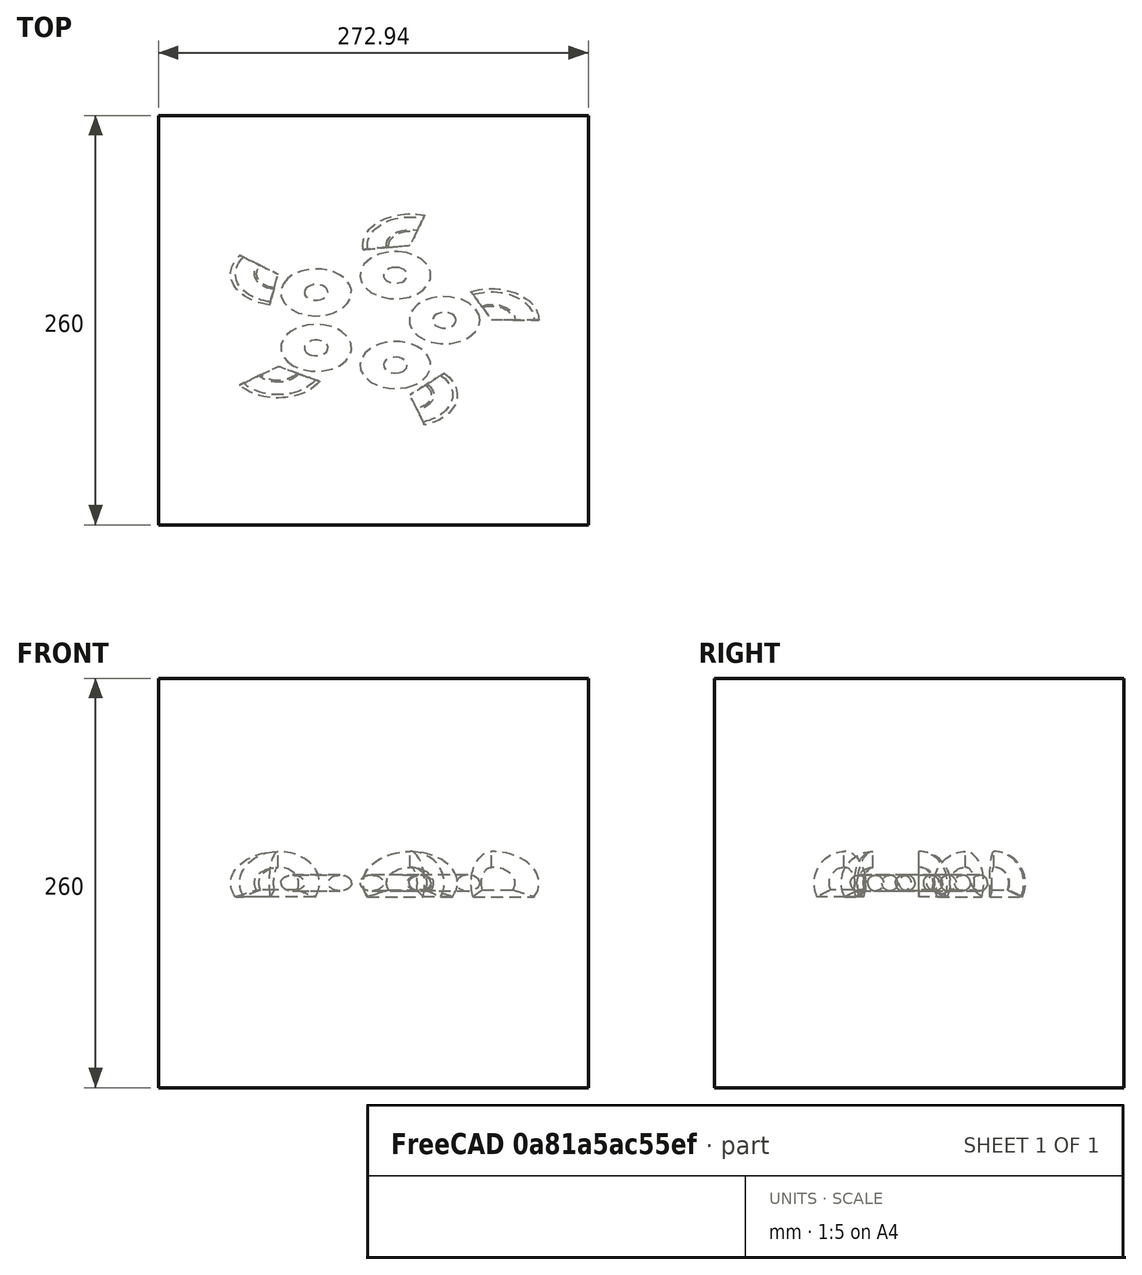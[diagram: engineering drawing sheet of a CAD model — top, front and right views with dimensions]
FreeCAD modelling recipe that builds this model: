
FCSTD DOCUMENT  (FreeCAD 1.0R39109 (Git))
Label: arrayTest-7_scaled
License: All rights reserved
LicenseURL: http://en.wikipedia.org/wiki/All_rights_reserved
objects: App::DocumentObjectGroupPython×1248, Part::FeaturePython×5, App::Part×2, Part::MultiFuse×1
note: 6 computed .brp shape members not serialized (recipe doc carries the construction recipe); baked Part::Feature solids carry a one-line shape summary decoded from their .brp

FEATURE [App::DocumentObjectGroupPython] HALFPI  # scripted group (container) (typed FeaturePython)
  name = HALFPI
  value = pi/2.
FEATURE [App::DocumentObjectGroupPython] PI  # scripted group (container) (typed FeaturePython)
  name = PI
  value = 1.*pi
FEATURE [App::DocumentObjectGroupPython] TWOPI  # scripted group (container) (typed FeaturePython)
  name = TWOPI
  value = 2.*pi
FEATURE [App::DocumentObjectGroupPython] Constants  # scripted group (container) (typed FeaturePython)
  Group = -> [HALFPI,PI,TWOPI]
FEATURE [App::DocumentObjectGroupPython] Variables  # scripted group (container) (typed FeaturePython)
FEATURE [App::DocumentObjectGroupPython] Quantities  # scripted group (container) (typed FeaturePython)
FEATURE [App::DocumentObjectGroupPython] Isotopes  # scripted group (container) (typed FeaturePython)
FEATURE [App::DocumentObjectGroupPython] Elements  # scripted group (container) (typed FeaturePython)
FEATURE [App::DocumentObjectGroupPython] G4Isotopes  # scripted group (container) (typed FeaturePython)
FEATURE [App::DocumentObjectGroupPython] H_element  # scripted group (container) (typed FeaturePython)
  Z = 1
  atom_value = 1.008
  formula = H
  name = H_element
FEATURE [App::DocumentObjectGroupPython] He_element  # scripted group (container) (typed FeaturePython)
  Z = 2
  atom_value = 4.0026
  formula = He
  name = He_element
FEATURE [App::DocumentObjectGroupPython] Li_element  # scripted group (container) (typed FeaturePython)
  Z = 3
  atom_value = 6.94
  formula = Li
  name = Li_element
FEATURE [App::DocumentObjectGroupPython] Be_element  # scripted group (container) (typed FeaturePython)
  Z = 4
  atom_value = 9.01218
  formula = Be
  name = Be_element
FEATURE [App::DocumentObjectGroupPython] B_element  # scripted group (container) (typed FeaturePython)
  Z = 5
  atom_value = 10.81
  formula = B
  name = B_element
FEATURE [App::DocumentObjectGroupPython] C_element  # scripted group (container) (typed FeaturePython)
  Z = 6
  atom_value = 12.011
  formula = C
  name = C_element
FEATURE [App::DocumentObjectGroupPython] N_element  # scripted group (container) (typed FeaturePython)
  Z = 7
  atom_value = 14.007
  formula = N
  name = N_element
FEATURE [App::DocumentObjectGroupPython] O_element  # scripted group (container) (typed FeaturePython)
  Z = 8
  atom_value = 15.999
  formula = O
  name = O_element
FEATURE [App::DocumentObjectGroupPython] F_element  # scripted group (container) (typed FeaturePython)
  Z = 9
  atom_value = 18.9984
  formula = F
  name = F_element
FEATURE [App::DocumentObjectGroupPython] Ne_element  # scripted group (container) (typed FeaturePython)
  Z = 10
  atom_value = 20.1797
  formula = Ne
  name = Ne_element
FEATURE [App::DocumentObjectGroupPython] Na_element  # scripted group (container) (typed FeaturePython)
  Z = 11
  atom_value = 22.9898
  formula = Na
  name = Na_element
FEATURE [App::DocumentObjectGroupPython] Mg_element  # scripted group (container) (typed FeaturePython)
  Z = 12
  atom_value = 24.305
  formula = Mg
  name = Mg_element
FEATURE [App::DocumentObjectGroupPython] Al_element  # scripted group (container) (typed FeaturePython)
  Z = 13
  atom_value = 26.9815
  formula = Al
  name = Al_element
FEATURE [App::DocumentObjectGroupPython] Si_element  # scripted group (container) (typed FeaturePython)
  Z = 14
  atom_value = 28.085
  formula = Si
  name = Si_element
FEATURE [App::DocumentObjectGroupPython] P_element  # scripted group (container) (typed FeaturePython)
  Z = 15
  atom_value = 30.9738
  formula = P
  name = P_element
FEATURE [App::DocumentObjectGroupPython] S_element  # scripted group (container) (typed FeaturePython)
  Z = 16
  atom_value = 32.06
  formula = S
  name = S_element
FEATURE [App::DocumentObjectGroupPython] Cl_element  # scripted group (container) (typed FeaturePython)
  Z = 17
  atom_value = 35.45
  formula = Cl
  name = Cl_element
FEATURE [App::DocumentObjectGroupPython] Ar_element  # scripted group (container) (typed FeaturePython)
  Z = 18
  atom_value = 39.95
  formula = Ar
  name = Ar_element
FEATURE [App::DocumentObjectGroupPython] K_element  # scripted group (container) (typed FeaturePython)
  Z = 19
  atom_value = 39.0983
  formula = K
  name = K_element
FEATURE [App::DocumentObjectGroupPython] Ca_element  # scripted group (container) (typed FeaturePython)
  Z = 20
  atom_value = 40.078
  formula = Ca
  name = Ca_element
FEATURE [App::DocumentObjectGroupPython] Sc_element  # scripted group (container) (typed FeaturePython)
  Z = 21
  atom_value = 44.9559
  formula = Sc
  name = Sc_element
FEATURE [App::DocumentObjectGroupPython] Ti_element  # scripted group (container) (typed FeaturePython)
  Z = 22
  atom_value = 47.867
  formula = Ti
  name = Ti_element
FEATURE [App::DocumentObjectGroupPython] V_element  # scripted group (container) (typed FeaturePython)
  Z = 23
  atom_value = 50.9415
  formula = V
  name = V_element
FEATURE [App::DocumentObjectGroupPython] Cr_element  # scripted group (container) (typed FeaturePython)
  Z = 24
  atom_value = 51.9961
  formula = Cr
  name = Cr_element
FEATURE [App::DocumentObjectGroupPython] Mn_element  # scripted group (container) (typed FeaturePython)
  Z = 25
  atom_value = 54.938
  formula = Mn
  name = Mn_element
FEATURE [App::DocumentObjectGroupPython] Fe_element  # scripted group (container) (typed FeaturePython)
  Z = 26
  atom_value = 55.845
  formula = Fe
  name = Fe_element
FEATURE [App::DocumentObjectGroupPython] Co_element  # scripted group (container) (typed FeaturePython)
  Z = 27
  atom_value = 58.9332
  formula = Co
  name = Co_element
FEATURE [App::DocumentObjectGroupPython] Ni_element  # scripted group (container) (typed FeaturePython)
  Z = 28
  atom_value = 58.6934
  formula = Ni
  name = Ni_element
FEATURE [App::DocumentObjectGroupPython] Cu_element  # scripted group (container) (typed FeaturePython)
  Z = 29
  atom_value = 63.546
  formula = Cu
  name = Cu_element
FEATURE [App::DocumentObjectGroupPython] Zn_element  # scripted group (container) (typed FeaturePython)
  Z = 30
  atom_value = 65.38
  formula = Zn
  name = Zn_element
FEATURE [App::DocumentObjectGroupPython] Ga_element  # scripted group (container) (typed FeaturePython)
  Z = 31
  atom_value = 69.723
  formula = Ga
  name = Ga_element
FEATURE [App::DocumentObjectGroupPython] Ge_element  # scripted group (container) (typed FeaturePython)
  Z = 32
  atom_value = 72.63
  formula = Ge
  name = Ge_element
FEATURE [App::DocumentObjectGroupPython] As_element  # scripted group (container) (typed FeaturePython)
  Z = 33
  atom_value = 74.9216
  formula = As
  name = As_element
FEATURE [App::DocumentObjectGroupPython] Se_element  # scripted group (container) (typed FeaturePython)
  Z = 34
  atom_value = 78.971
  formula = Se
  name = Se_element
FEATURE [App::DocumentObjectGroupPython] Br_element  # scripted group (container) (typed FeaturePython)
  Z = 35
  atom_value = 79.904
  formula = Br
  name = Br_element
FEATURE [App::DocumentObjectGroupPython] Kr_element  # scripted group (container) (typed FeaturePython)
  Z = 36
  atom_value = 83.798
  formula = Kr
  name = Kr_element
FEATURE [App::DocumentObjectGroupPython] Rb_element  # scripted group (container) (typed FeaturePython)
  Z = 37
  atom_value = 85.4678
  formula = Rb
  name = Rb_element
FEATURE [App::DocumentObjectGroupPython] Sr_element  # scripted group (container) (typed FeaturePython)
  Z = 38
  atom_value = 87.62
  formula = Sr
  name = Sr_element
FEATURE [App::DocumentObjectGroupPython] Y_element  # scripted group (container) (typed FeaturePython)
  Z = 39
  atom_value = 88.9058
  formula = Y
  name = Y_element
FEATURE [App::DocumentObjectGroupPython] Zr_element  # scripted group (container) (typed FeaturePython)
  Z = 40
  atom_value = 91.224
  formula = Zr
  name = Zr_element
FEATURE [App::DocumentObjectGroupPython] Nb_element  # scripted group (container) (typed FeaturePython)
  Z = 41
  atom_value = 92.9064
  formula = Nb
  name = Nb_element
FEATURE [App::DocumentObjectGroupPython] Mo_element  # scripted group (container) (typed FeaturePython)
  Z = 42
  atom_value = 95.95
  formula = Mo
  name = Mo_element
FEATURE [App::DocumentObjectGroupPython] Tc_element  # scripted group (container) (typed FeaturePython)
  Z = 43
  atom_value = 97
  formula = Tc
  name = Tc_element
FEATURE [App::DocumentObjectGroupPython] Ru_element  # scripted group (container) (typed FeaturePython)
  Z = 44
  atom_value = 101.07
  formula = Ru
  name = Ru_element
FEATURE [App::DocumentObjectGroupPython] Rh_element  # scripted group (container) (typed FeaturePython)
  Z = 45
  atom_value = 102.905
  formula = Rh
  name = Rh_element
FEATURE [App::DocumentObjectGroupPython] Pd_element  # scripted group (container) (typed FeaturePython)
  Z = 46
  atom_value = 106.42
  formula = Pd
  name = Pd_element
FEATURE [App::DocumentObjectGroupPython] Ag_element  # scripted group (container) (typed FeaturePython)
  Z = 47
  atom_value = 107.868
  formula = Ag
  name = Ag_element
FEATURE [App::DocumentObjectGroupPython] Cd_element  # scripted group (container) (typed FeaturePython)
  Z = 48
  atom_value = 112.414
  formula = Cd
  name = Cd_element
FEATURE [App::DocumentObjectGroupPython] In_element  # scripted group (container) (typed FeaturePython)
  Z = 49
  atom_value = 114.818
  formula = In
  name = In_element
FEATURE [App::DocumentObjectGroupPython] Sn_element  # scripted group (container) (typed FeaturePython)
  Z = 50
  atom_value = 118.71
  formula = Sn
  name = Sn_element
FEATURE [App::DocumentObjectGroupPython] Sb_element  # scripted group (container) (typed FeaturePython)
  Z = 51
  atom_value = 121.76
  formula = Sb
  name = Sb_element
FEATURE [App::DocumentObjectGroupPython] Te_element  # scripted group (container) (typed FeaturePython)
  Z = 52
  atom_value = 127.6
  formula = Te
  name = Te_element
FEATURE [App::DocumentObjectGroupPython] I_element  # scripted group (container) (typed FeaturePython)
  Z = 53
  atom_value = 126.904
  formula = I
  name = I_element
FEATURE [App::DocumentObjectGroupPython] Xe_element  # scripted group (container) (typed FeaturePython)
  Z = 54
  atom_value = 131.293
  formula = Xe
  name = Xe_element
FEATURE [App::DocumentObjectGroupPython] Cs_element  # scripted group (container) (typed FeaturePython)
  Z = 55
  atom_value = 132.905
  formula = Cs
  name = Cs_element
FEATURE [App::DocumentObjectGroupPython] Ba_element  # scripted group (container) (typed FeaturePython)
  Z = 56
  atom_value = 137.327
  formula = Ba
  name = Ba_element
FEATURE [App::DocumentObjectGroupPython] La_element  # scripted group (container) (typed FeaturePython)
  Z = 57
  atom_value = 138.905
  formula = La
  name = La_element
FEATURE [App::DocumentObjectGroupPython] Ce_element  # scripted group (container) (typed FeaturePython)
  Z = 58
  atom_value = 140.116
  formula = Ce
  name = Ce_element
FEATURE [App::DocumentObjectGroupPython] Pr_element  # scripted group (container) (typed FeaturePython)
  Z = 59
  atom_value = 140.908
  formula = Pr
  name = Pr_element
FEATURE [App::DocumentObjectGroupPython] Nd_element  # scripted group (container) (typed FeaturePython)
  Z = 60
  atom_value = 144.242
  formula = Nd
  name = Nd_element
FEATURE [App::DocumentObjectGroupPython] Pm_element  # scripted group (container) (typed FeaturePython)
  Z = 61
  atom_value = 145
  formula = Pm
  name = Pm_element
FEATURE [App::DocumentObjectGroupPython] Sm_element  # scripted group (container) (typed FeaturePython)
  Z = 62
  atom_value = 150.36
  formula = Sm
  name = Sm_element
FEATURE [App::DocumentObjectGroupPython] Eu_element  # scripted group (container) (typed FeaturePython)
  Z = 63
  atom_value = 151.964
  formula = Eu
  name = Eu_element
FEATURE [App::DocumentObjectGroupPython] Gd_element  # scripted group (container) (typed FeaturePython)
  Z = 64
  atom_value = 157.25
  formula = Gd
  name = Gd_element
FEATURE [App::DocumentObjectGroupPython] Tb_element  # scripted group (container) (typed FeaturePython)
  Z = 65
  atom_value = 158.925
  formula = Tb
  name = Tb_element
FEATURE [App::DocumentObjectGroupPython] Dy_element  # scripted group (container) (typed FeaturePython)
  Z = 66
  atom_value = 162.5
  formula = Dy
  name = Dy_element
FEATURE [App::DocumentObjectGroupPython] Ho_element  # scripted group (container) (typed FeaturePython)
  Z = 67
  atom_value = 164.93
  formula = Ho
  name = Ho_element
FEATURE [App::DocumentObjectGroupPython] Er_element  # scripted group (container) (typed FeaturePython)
  Z = 68
  atom_value = 167.259
  formula = Er
  name = Er_element
FEATURE [App::DocumentObjectGroupPython] Tm_element  # scripted group (container) (typed FeaturePython)
  Z = 69
  atom_value = 168.934
  formula = Tm
  name = Tm_element
FEATURE [App::DocumentObjectGroupPython] Yb_element  # scripted group (container) (typed FeaturePython)
  Z = 70
  atom_value = 173.045
  formula = Yb
  name = Yb_element
FEATURE [App::DocumentObjectGroupPython] Lu_element  # scripted group (container) (typed FeaturePython)
  Z = 71
  atom_value = 174.967
  formula = Lu
  name = Lu_element
FEATURE [App::DocumentObjectGroupPython] Hf_element  # scripted group (container) (typed FeaturePython)
  Z = 72
  atom_value = 178.49
  formula = Hf
  name = Hf_element
FEATURE [App::DocumentObjectGroupPython] Ta_element  # scripted group (container) (typed FeaturePython)
  Z = 73
  atom_value = 180.948
  formula = Ta
  name = Ta_element
FEATURE [App::DocumentObjectGroupPython] W_element  # scripted group (container) (typed FeaturePython)
  Z = 74
  atom_value = 183.84
  formula = W
  name = W_element
FEATURE [App::DocumentObjectGroupPython] Re_element  # scripted group (container) (typed FeaturePython)
  Z = 75
  atom_value = 186.207
  formula = Re
  name = Re_element
FEATURE [App::DocumentObjectGroupPython] Os_element  # scripted group (container) (typed FeaturePython)
  Z = 76
  atom_value = 190.23
  formula = Os
  name = Os_element
FEATURE [App::DocumentObjectGroupPython] Ir_element  # scripted group (container) (typed FeaturePython)
  Z = 77
  atom_value = 192.217
  formula = Ir
  name = Ir_element
FEATURE [App::DocumentObjectGroupPython] Pt_element  # scripted group (container) (typed FeaturePython)
  Z = 78
  atom_value = 195.084
  formula = Pt
  name = Pt_element
FEATURE [App::DocumentObjectGroupPython] Au_element  # scripted group (container) (typed FeaturePython)
  Z = 79
  atom_value = 196.967
  formula = Au
  name = Au_element
FEATURE [App::DocumentObjectGroupPython] Hg_element  # scripted group (container) (typed FeaturePython)
  Z = 80
  atom_value = 200.592
  formula = Hg
  name = Hg_element
FEATURE [App::DocumentObjectGroupPython] Tl_element  # scripted group (container) (typed FeaturePython)
  Z = 81
  atom_value = 204.38
  formula = Tl
  name = Tl_element
FEATURE [App::DocumentObjectGroupPython] Pb_element  # scripted group (container) (typed FeaturePython)
  Z = 82
  atom_value = 207.2
  formula = Pb
  name = Pb_element
FEATURE [App::DocumentObjectGroupPython] Bi_element  # scripted group (container) (typed FeaturePython)
  Z = 83
  atom_value = 208.98
  formula = Bi
  name = Bi_element
FEATURE [App::DocumentObjectGroupPython] Po_element  # scripted group (container) (typed FeaturePython)
  Z = 84
  atom_value = 209
  formula = Po
  name = Po_element
FEATURE [App::DocumentObjectGroupPython] At_element  # scripted group (container) (typed FeaturePython)
  Z = 85
  atom_value = 210
  formula = At
  name = At_element
FEATURE [App::DocumentObjectGroupPython] Rn_element  # scripted group (container) (typed FeaturePython)
  Z = 86
  atom_value = 222
  formula = Rn
  name = Rn_element
FEATURE [App::DocumentObjectGroupPython] Fr_element  # scripted group (container) (typed FeaturePython)
  Z = 87
  atom_value = 223
  formula = Fr
  name = Fr_element
FEATURE [App::DocumentObjectGroupPython] Ra_element  # scripted group (container) (typed FeaturePython)
  Z = 88
  atom_value = 226
  formula = Ra
  name = Ra_element
FEATURE [App::DocumentObjectGroupPython] Ac_element  # scripted group (container) (typed FeaturePython)
  Z = 89
  atom_value = 227
  formula = Ac
  name = Ac_element
FEATURE [App::DocumentObjectGroupPython] Th_element  # scripted group (container) (typed FeaturePython)
  Z = 90
  atom_value = 232.038
  formula = Th
  name = Th_element
FEATURE [App::DocumentObjectGroupPython] Pa_element  # scripted group (container) (typed FeaturePython)
  Z = 91
  atom_value = 231.036
  formula = Pa
  name = Pa_element
FEATURE [App::DocumentObjectGroupPython] U_element  # scripted group (container) (typed FeaturePython)
  Z = 92
  atom_value = 238.029
  formula = U
  name = U_element
FEATURE [App::DocumentObjectGroupPython] Np_element  # scripted group (container) (typed FeaturePython)
  Z = 93
  atom_value = 237
  formula = Np
  name = Np_element
FEATURE [App::DocumentObjectGroupPython] Pu_element  # scripted group (container) (typed FeaturePython)
  Z = 94
  atom_value = 244
  formula = Pu
  name = Pu_element
FEATURE [App::DocumentObjectGroupPython] Am_element  # scripted group (container) (typed FeaturePython)
  Z = 95
  atom_value = 243
  formula = Am
  name = Am_element
FEATURE [App::DocumentObjectGroupPython] Cm_element  # scripted group (container) (typed FeaturePython)
  Z = 96
  atom_value = 247
  formula = Cm
  name = Cm_element
FEATURE [App::DocumentObjectGroupPython] Bk_element  # scripted group (container) (typed FeaturePython)
  Z = 97
  atom_value = 247
  formula = Bk
  name = Bk_element
FEATURE [App::DocumentObjectGroupPython] Cf_element  # scripted group (container) (typed FeaturePython)
  Z = 98
  atom_value = 251
  formula = Cf
  name = Cf_element
FEATURE [App::DocumentObjectGroupPython] G4Elements  # scripted group (container) (typed FeaturePython)
  Group = -> [H_element,He_element,Li_element,Be_element,B_element,C_element,N_element,O_element,F_element,Ne_element,Na_element,Mg_element,Al_element,Si_element,P_element,S_element,Cl_element,Ar_element,K_element,Ca_element,Sc_element,Ti_element,V_element,Cr_element,Mn_element,Fe_element,Co_element,Ni_element,Cu_element,Zn_element,Ga_element,Ge_element,As_element,Se_element,Br_element,Kr_element,Rb_element,+61 more]
FEATURE [App::DocumentObjectGroupPython] H_element001  label="H_element : 0.101"  # scripted group (container) (typed FeaturePython)
  n = 0.101327
FEATURE [App::DocumentObjectGroupPython] C_element001  label="C_element : 0.775"  # scripted group (container) (typed FeaturePython)
  n = 0.7755
FEATURE [App::DocumentObjectGroupPython] N_element001  label="N_element : 0.035"  # scripted group (container) (typed FeaturePython)
  n = 0.035057
FEATURE [App::DocumentObjectGroupPython] O_element001  label="O_element : 0.052"  # scripted group (container) (typed FeaturePython)
  n = 0.0523159
FEATURE [App::DocumentObjectGroupPython] F_element001  label="F_element : 0.017"  # scripted group (container) (typed FeaturePython)
  n = 0.017422
FEATURE [App::DocumentObjectGroupPython] Ca_element001  label="Ca_element : 0.018"  # scripted group (container) (typed FeaturePython)
  n = 0.018378
FEATURE [App::DocumentObjectGroupPython] G4_A_150_TISSUE  label="G4_A-150_TISSUE"  # scripted group (container) (typed FeaturePython)
  Dunit = g/cm3
  Dvalue = 1.127
  Group = -> [H_element001,C_element001,N_element001,O_element001,F_element001,Ca_element001]
  conduct = 2
  density = 1
  expand = 3
  formula = G4_A-150_TISSUE
  name = G4_A-150_TISSUE
  specific = 4
FEATURE [App::DocumentObjectGroupPython] C_element002  label="C_element : 3"  # scripted group (container) (typed FeaturePython)
  n = 3
  ref = C_element
FEATURE [App::DocumentObjectGroupPython] H_element002  label="H_element : 6"  # scripted group (container) (typed FeaturePython)
  n = 6
  ref = H_element
FEATURE [App::DocumentObjectGroupPython] O_element002  label="O_element : 1"  # scripted group (container) (typed FeaturePython)
  n = 1
  ref = O_element
FEATURE [App::DocumentObjectGroupPython] G4_ACETONE  # scripted group (container) (typed FeaturePython)
  Dunit = g/cm3
  Dvalue = 0.7899
  Group = -> [C_element002,H_element002,O_element002]
  conduct = 2
  density = 1
  expand = 3
  formula = G4_ACETONE
  name = G4_ACETONE
  specific = 4
FEATURE [App::DocumentObjectGroupPython] C_element003  label="C_element : 2"  # scripted group (container) (typed FeaturePython)
  n = 2
  ref = C_element
FEATURE [App::DocumentObjectGroupPython] H_element003  label="H_element : 2"  # scripted group (container) (typed FeaturePython)
  n = 2
  ref = H_element
FEATURE [App::DocumentObjectGroupPython] G4_ACETYLENE  # scripted group (container) (typed FeaturePython)
  Dunit = g/cm3
  Dvalue = 0.0010967
  Group = -> [C_element003,H_element003]
  conduct = 2
  density = 1
  expand = 3
  formula = G4_ACETYLENE
  name = G4_ACETYLENE
  specific = 4
FEATURE [App::DocumentObjectGroupPython] C_element004  label="C_element : 5"  # scripted group (container) (typed FeaturePython)
  n = 5
  ref = C_element
FEATURE [App::DocumentObjectGroupPython] H_element004  label="H_element : 5"  # scripted group (container) (typed FeaturePython)
  n = 5
  ref = H_element
FEATURE [App::DocumentObjectGroupPython] N_element002  label="N_element : 5"  # scripted group (container) (typed FeaturePython)
  n = 5
  ref = N_element
FEATURE [App::DocumentObjectGroupPython] G4_ADENINE  # scripted group (container) (typed FeaturePython)
  Dunit = g/cm3
  Dvalue = 1.6
  Group = -> [C_element004,H_element004,N_element002]
  conduct = 2
  density = 1
  expand = 3
  formula = G4_ADENINE
  name = G4_ADENINE
  specific = 4
FEATURE [App::DocumentObjectGroupPython] H_element005  label="H_element : 0.114"  # scripted group (container) (typed FeaturePython)
  n = 0.114
FEATURE [App::DocumentObjectGroupPython] C_element005  label="C_element : 0.598"  # scripted group (container) (typed FeaturePython)
  n = 0.598
FEATURE [App::DocumentObjectGroupPython] N_element003  label="N_element : 0.007"  # scripted group (container) (typed FeaturePython)
  n = 0.007
FEATURE [App::DocumentObjectGroupPython] O_element003  label="O_element : 0.278"  # scripted group (container) (typed FeaturePython)
  n = 0.278
FEATURE [App::DocumentObjectGroupPython] Na_element001  label="Na_element : 0.001"  # scripted group (container) (typed FeaturePython)
  n = 0.001
FEATURE [App::DocumentObjectGroupPython] S_element001  label="S_element : 0.001"  # scripted group (container) (typed FeaturePython)
  n = 0.001
FEATURE [App::DocumentObjectGroupPython] Cl_element001  label="Cl_element : 0.001"  # scripted group (container) (typed FeaturePython)
  n = 0.001
FEATURE [App::DocumentObjectGroupPython] G4_ADIPOSE_TISSUE_ICRP  # scripted group (container) (typed FeaturePython)
  Dunit = g/cm3
  Dvalue = 0.95
  Group = -> [H_element005,C_element005,N_element003,O_element003,Na_element001,S_element001,Cl_element001]
  conduct = 2
  density = 1
  expand = 3
  formula = G4_ADIPOSE_TISSUE_ICRP
  name = G4_ADIPOSE_TISSUE_ICRP
  specific = 4
FEATURE [App::DocumentObjectGroupPython] C_element006  label="C_element : 0.000"  # scripted group (container) (typed FeaturePython)
  n = 0.000124
FEATURE [App::DocumentObjectGroupPython] N_element004  label="N_element : 0.755"  # scripted group (container) (typed FeaturePython)
  n = 0.755268
FEATURE [App::DocumentObjectGroupPython] O_element004  label="O_element : 0.232"  # scripted group (container) (typed FeaturePython)
  n = 0.231781
FEATURE [App::DocumentObjectGroupPython] Ar_element001  label="Ar_element : 0.013"  # scripted group (container) (typed FeaturePython)
  n = 0.012827
FEATURE [App::DocumentObjectGroupPython] G4_AIR  # scripted group (container) (typed FeaturePython)
  Dunit = g/cm3
  Dvalue = 0.00120479
  Group = -> [C_element006,N_element004,O_element004,Ar_element001]
  conduct = 2
  density = 1
  expand = 3
  formula = G4_AIR
  name = G4_AIR
  specific = 4
FEATURE [App::DocumentObjectGroupPython] C_element007  label="C_element : 006"  # scripted group (container) (typed FeaturePython)
  n = 3
  ref = C_element
FEATURE [App::DocumentObjectGroupPython] H_element006  label="H_element : 7"  # scripted group (container) (typed FeaturePython)
  n = 7
  ref = H_element
FEATURE [App::DocumentObjectGroupPython] N_element005  label="N_element : 1"  # scripted group (container) (typed FeaturePython)
  n = 1
  ref = N_element
FEATURE [App::DocumentObjectGroupPython] O_element005  label="O_element : 2"  # scripted group (container) (typed FeaturePython)
  n = 2
  ref = O_element
FEATURE [App::DocumentObjectGroupPython] G4_ALANINE  # scripted group (container) (typed FeaturePython)
  Dunit = g/cm3
  Dvalue = 1.42
  Group = -> [C_element007,H_element006,N_element005,O_element005]
  conduct = 2
  density = 1
  expand = 3
  formula = G4_ALANINE
  name = G4_ALANINE
  specific = 4
FEATURE [App::DocumentObjectGroupPython] Al_element001  label="Al_element : 2"  # scripted group (container) (typed FeaturePython)
  n = 2
  ref = Al_element
FEATURE [App::DocumentObjectGroupPython] O_element006  label="O_element : 3"  # scripted group (container) (typed FeaturePython)
  n = 3
  ref = O_element
FEATURE [App::DocumentObjectGroupPython] G4_ALUMINUM_OXIDE  # scripted group (container) (typed FeaturePython)
  Dunit = g/cm3
  Dvalue = 3.97
  Group = -> [Al_element001,O_element006]
  conduct = 2
  density = 1
  expand = 3
  formula = G4_ALUMINUM_OXIDE
  name = G4_ALUMINUM_OXIDE
  specific = 4
FEATURE [App::DocumentObjectGroupPython] H_element007  label="H_element : 0.106"  # scripted group (container) (typed FeaturePython)
  n = 0.10593
FEATURE [App::DocumentObjectGroupPython] C_element008  label="C_element : 0.789"  # scripted group (container) (typed FeaturePython)
  n = 0.788974
FEATURE [App::DocumentObjectGroupPython] O_element007  label="O_element : 0.105"  # scripted group (container) (typed FeaturePython)
  n = 0.105096
FEATURE [App::DocumentObjectGroupPython] G4_AMBER  # scripted group (container) (typed FeaturePython)
  Dunit = g/cm3
  Dvalue = 1.1
  Group = -> [H_element007,C_element008,O_element007]
  conduct = 2
  density = 1
  expand = 3
  formula = G4_AMBER
  name = G4_AMBER
  specific = 4
FEATURE [App::DocumentObjectGroupPython] N_element006  label="N_element : 006"  # scripted group (container) (typed FeaturePython)
  n = 1
  ref = N_element
FEATURE [App::DocumentObjectGroupPython] H_element008  label="H_element : 3"  # scripted group (container) (typed FeaturePython)
  n = 3
  ref = H_element
FEATURE [App::DocumentObjectGroupPython] G4_AMMONIA  # scripted group (container) (typed FeaturePython)
  Dunit = g/cm3
  Dvalue = 0.000826019
  Group = -> [N_element006,H_element008]
  conduct = 2
  density = 1
  expand = 3
  formula = G4_AMMONIA
  name = G4_AMMONIA
  specific = 4
FEATURE [App::DocumentObjectGroupPython] C_element009  label="C_element : 6"  # scripted group (container) (typed FeaturePython)
  n = 6
  ref = C_element
FEATURE [App::DocumentObjectGroupPython] H_element009  label="H_element : 008"  # scripted group (container) (typed FeaturePython)
  n = 7
  ref = H_element
FEATURE [App::DocumentObjectGroupPython] N_element007  label="N_element : 007"  # scripted group (container) (typed FeaturePython)
  n = 1
  ref = N_element
FEATURE [App::DocumentObjectGroupPython] G4_ANILINE  # scripted group (container) (typed FeaturePython)
  Dunit = g/cm3
  Dvalue = 1.0235
  Group = -> [C_element009,H_element009,N_element007]
  conduct = 2
  density = 1
  expand = 3
  formula = G4_ANILINE
  name = G4_ANILINE
  specific = 4
FEATURE [App::DocumentObjectGroupPython] C_element010  label="C_element : 14"  # scripted group (container) (typed FeaturePython)
  n = 14
  ref = C_element
FEATURE [App::DocumentObjectGroupPython] H_element010  label="H_element : 10"  # scripted group (container) (typed FeaturePython)
  n = 10
  ref = H_element
FEATURE [App::DocumentObjectGroupPython] G4_ANTHRACENE  # scripted group (container) (typed FeaturePython)
  Dunit = g/cm3
  Dvalue = 1.283
  Group = -> [C_element010,H_element010]
  conduct = 2
  density = 1
  expand = 3
  formula = G4_ANTHRACENE
  name = G4_ANTHRACENE
  specific = 4
FEATURE [App::DocumentObjectGroupPython] H_element011  label="H_element : 0.065"  # scripted group (container) (typed FeaturePython)
  n = 0.0654709
FEATURE [App::DocumentObjectGroupPython] C_element011  label="C_element : 0.537"  # scripted group (container) (typed FeaturePython)
  n = 0.536944
FEATURE [App::DocumentObjectGroupPython] N_element008  label="N_element : 0.021"  # scripted group (container) (typed FeaturePython)
  n = 0.0215
FEATURE [App::DocumentObjectGroupPython] O_element008  label="O_element : 0.032"  # scripted group (container) (typed FeaturePython)
  n = 0.032085
FEATURE [App::DocumentObjectGroupPython] F_element002  label="F_element : 0.167"  # scripted group (container) (typed FeaturePython)
  n = 0.167411
FEATURE [App::DocumentObjectGroupPython] Ca_element002  label="Ca_element : 0.177"  # scripted group (container) (typed FeaturePython)
  n = 0.176589
FEATURE [App::DocumentObjectGroupPython] G4_B_100_BONE  label="G4_B-100_BONE"  # scripted group (container) (typed FeaturePython)
  Dunit = g/cm3
  Dvalue = 1.45
  Group = -> [H_element011,C_element011,N_element008,O_element008,F_element002,Ca_element002]
  conduct = 2
  density = 1
  expand = 3
  formula = G4_B-100_BONE
  name = G4_B-100_BONE
  specific = 4
FEATURE [App::DocumentObjectGroupPython] H_element012  label="H_element : 0.057"  # scripted group (container) (typed FeaturePython)
  n = 0.057441
FEATURE [App::DocumentObjectGroupPython] C_element012  label="C_element : 0.790"  # scripted group (container) (typed FeaturePython)
  n = 0.774591
FEATURE [App::DocumentObjectGroupPython] O_element009  label="O_element : 0.168"  # scripted group (container) (typed FeaturePython)
  n = 0.167968
FEATURE [App::DocumentObjectGroupPython] G4_BAKELITE  # scripted group (container) (typed FeaturePython)
  Dunit = g/cm3
  Dvalue = 1.25
  Group = -> [H_element012,C_element012,O_element009]
  conduct = 2
  density = 1
  expand = 3
  formula = G4_BAKELITE
  name = G4_BAKELITE
  specific = 4
FEATURE [App::DocumentObjectGroupPython] Ba_element001  label="Ba_element : 1"  # scripted group (container) (typed FeaturePython)
  n = 1
  ref = Ba_element
FEATURE [App::DocumentObjectGroupPython] F_element003  label="F_element : 2"  # scripted group (container) (typed FeaturePython)
  n = 2
  ref = F_element
FEATURE [App::DocumentObjectGroupPython] G4_BARIUM_FLUORIDE  # scripted group (container) (typed FeaturePython)
  Dunit = g/cm3
  Dvalue = 4.89
  Group = -> [Ba_element001,F_element003]
  conduct = 2
  density = 1
  expand = 3
  formula = G4_BARIUM_FLUORIDE
  name = G4_BARIUM_FLUORIDE
  specific = 4
FEATURE [App::DocumentObjectGroupPython] Ba_element002  label="Ba_element : 002"  # scripted group (container) (typed FeaturePython)
  n = 1
  ref = Ba_element
FEATURE [App::DocumentObjectGroupPython] S_element002  label="S_element : 1"  # scripted group (container) (typed FeaturePython)
  n = 1
  ref = S_element
FEATURE [App::DocumentObjectGroupPython] O_element010  label="O_element : 4"  # scripted group (container) (typed FeaturePython)
  n = 4
  ref = O_element
FEATURE [App::DocumentObjectGroupPython] G4_BARIUM_SULFATE  # scripted group (container) (typed FeaturePython)
  Dunit = g/cm3
  Dvalue = 4.5
  Group = -> [Ba_element002,S_element002,O_element010]
  conduct = 2
  density = 1
  expand = 3
  formula = G4_BARIUM_SULFATE
  name = G4_BARIUM_SULFATE
  specific = 4
FEATURE [App::DocumentObjectGroupPython] C_element013  label="C_element : 007"  # scripted group (container) (typed FeaturePython)
  n = 6
  ref = C_element
FEATURE [App::DocumentObjectGroupPython] H_element013  label="H_element : 009"  # scripted group (container) (typed FeaturePython)
  n = 6
  ref = H_element
FEATURE [App::DocumentObjectGroupPython] G4_BENZENE  # scripted group (container) (typed FeaturePython)
  Dunit = g/cm3
  Dvalue = 0.87865
  Group = -> [C_element013,H_element013]
  conduct = 2
  density = 1
  expand = 3
  formula = G4_BENZENE
  name = G4_BENZENE
  specific = 4
FEATURE [App::DocumentObjectGroupPython] Be_element001  label="Be_element : 1"  # scripted group (container) (typed FeaturePython)
  n = 1
  ref = Be_element
FEATURE [App::DocumentObjectGroupPython] O_element011  label="O_element : 005"  # scripted group (container) (typed FeaturePython)
  n = 1
  ref = O_element
FEATURE [App::DocumentObjectGroupPython] G4_BERYLLIUM_OXIDE  # scripted group (container) (typed FeaturePython)
  Dunit = g/cm3
  Dvalue = 3.01
  Group = -> [Be_element001,O_element011]
  conduct = 2
  density = 1
  expand = 3
  formula = G4_BERYLLIUM_OXIDE
  name = G4_BERYLLIUM_OXIDE
  specific = 4
FEATURE [App::DocumentObjectGroupPython] Bi_element001  label="Bi_element : 4"  # scripted group (container) (typed FeaturePython)
  n = 4
  ref = Bi_element
FEATURE [App::DocumentObjectGroupPython] Ge_element001  label="Ge_element : 3"  # scripted group (container) (typed FeaturePython)
  n = 3
  ref = Ge_element
FEATURE [App::DocumentObjectGroupPython] O_element012  label="O_element : 12"  # scripted group (container) (typed FeaturePython)
  n = 12
  ref = O_element
FEATURE [App::DocumentObjectGroupPython] G4_BGO  # scripted group (container) (typed FeaturePython)
  Dunit = g/cm3
  Dvalue = 7.13
  Group = -> [Bi_element001,Ge_element001,O_element012]
  conduct = 2
  density = 1
  expand = 3
  formula = G4_BGO
  name = G4_BGO
  specific = 4
FEATURE [App::DocumentObjectGroupPython] H_element014  label="H_element : 0.102"  # scripted group (container) (typed FeaturePython)
  n = 0.102
FEATURE [App::DocumentObjectGroupPython] C_element014  label="C_element : 0.110"  # scripted group (container) (typed FeaturePython)
  n = 0.11
FEATURE [App::DocumentObjectGroupPython] N_element009  label="N_element : 0.033"  # scripted group (container) (typed FeaturePython)
  n = 0.033
FEATURE [App::DocumentObjectGroupPython] O_element013  label="O_element : 0.745"  # scripted group (container) (typed FeaturePython)
  n = 0.745
FEATURE [App::DocumentObjectGroupPython] Na_element002  label="Na_element : 0.002"  # scripted group (container) (typed FeaturePython)
  n = 0.001
FEATURE [App::DocumentObjectGroupPython] P_element001  label="P_element : 0.001"  # scripted group (container) (typed FeaturePython)
  n = 0.001
FEATURE [App::DocumentObjectGroupPython] S_element003  label="S_element : 0.002"  # scripted group (container) (typed FeaturePython)
  n = 0.002
FEATURE [App::DocumentObjectGroupPython] Cl_element002  label="Cl_element : 0.003"  # scripted group (container) (typed FeaturePython)
  n = 0.003
FEATURE [App::DocumentObjectGroupPython] K_element001  label="K_element : 0.002"  # scripted group (container) (typed FeaturePython)
  n = 0.002
FEATURE [App::DocumentObjectGroupPython] Fe_element001  label="Fe_element : 0.001"  # scripted group (container) (typed FeaturePython)
  n = 0.001
FEATURE [App::DocumentObjectGroupPython] G4_BLOOD_ICRP  # scripted group (container) (typed FeaturePython)
  Dunit = g/cm3
  Dvalue = 1.06
  Group = -> [H_element014,C_element014,N_element009,O_element013,Na_element002,P_element001,S_element003,Cl_element002,K_element001,Fe_element001]
  conduct = 2
  density = 1
  expand = 3
  formula = G4_BLOOD_ICRP
  name = G4_BLOOD_ICRP
  specific = 4
FEATURE [App::DocumentObjectGroupPython] H_element015  label="H_element : 0.064"  # scripted group (container) (typed FeaturePython)
  n = 0.064
FEATURE [App::DocumentObjectGroupPython] C_element015  label="C_element : 0.278"  # scripted group (container) (typed FeaturePython)
  n = 0.278
FEATURE [App::DocumentObjectGroupPython] N_element010  label="N_element : 0.027"  # scripted group (container) (typed FeaturePython)
  n = 0.027
FEATURE [App::DocumentObjectGroupPython] O_element014  label="O_element : 0.410"  # scripted group (container) (typed FeaturePython)
  n = 0.41
FEATURE [App::DocumentObjectGroupPython] Mg_element001  label="Mg_element : 0.002"  # scripted group (container) (typed FeaturePython)
  n = 0.002
FEATURE [App::DocumentObjectGroupPython] P_element002  label="P_element : 0.070"  # scripted group (container) (typed FeaturePython)
  n = 0.07
FEATURE [App::DocumentObjectGroupPython] S_element004  label="S_element : 0.003"  # scripted group (container) (typed FeaturePython)
  n = 0.002
FEATURE [App::DocumentObjectGroupPython] Ca_element003  label="Ca_element : 0.147"  # scripted group (container) (typed FeaturePython)
  n = 0.147
FEATURE [App::DocumentObjectGroupPython] G4_BONE_COMPACT_ICRU  # scripted group (container) (typed FeaturePython)
  Dunit = g/cm3
  Dvalue = 1.85
  Group = -> [H_element015,C_element015,N_element010,O_element014,Mg_element001,P_element002,S_element004,Ca_element003]
  conduct = 2
  density = 1
  expand = 3
  formula = G4_BONE_COMPACT_ICRU
  name = G4_BONE_COMPACT_ICRU
  specific = 4
FEATURE [App::DocumentObjectGroupPython] H_element016  label="H_element : 0.034"  # scripted group (container) (typed FeaturePython)
  n = 0.034
FEATURE [App::DocumentObjectGroupPython] C_element016  label="C_element : 0.155"  # scripted group (container) (typed FeaturePython)
  n = 0.155
FEATURE [App::DocumentObjectGroupPython] N_element011  label="N_element : 0.042"  # scripted group (container) (typed FeaturePython)
  n = 0.042
FEATURE [App::DocumentObjectGroupPython] O_element015  label="O_element : 0.435"  # scripted group (container) (typed FeaturePython)
  n = 0.435
FEATURE [App::DocumentObjectGroupPython] Na_element003  label="Na_element : 0.003"  # scripted group (container) (typed FeaturePython)
  n = 0.001
FEATURE [App::DocumentObjectGroupPython] Mg_element002  label="Mg_element : 0.003"  # scripted group (container) (typed FeaturePython)
  n = 0.002
FEATURE [App::DocumentObjectGroupPython] P_element003  label="P_element : 0.103"  # scripted group (container) (typed FeaturePython)
  n = 0.103
FEATURE [App::DocumentObjectGroupPython] S_element005  label="S_element : 0.004"  # scripted group (container) (typed FeaturePython)
  n = 0.003
FEATURE [App::DocumentObjectGroupPython] Ca_element004  label="Ca_element : 0.225"  # scripted group (container) (typed FeaturePython)
  n = 0.225
FEATURE [App::DocumentObjectGroupPython] G4_BONE_CORTICAL_ICRP  # scripted group (container) (typed FeaturePython)
  Dunit = g/cm3
  Dvalue = 1.92
  Group = -> [H_element016,C_element016,N_element011,O_element015,Na_element003,Mg_element002,P_element003,S_element005,Ca_element004]
  conduct = 2
  density = 1
  expand = 3
  formula = G4_BONE_CORTICAL_ICRP
  name = G4_BONE_CORTICAL_ICRP
  specific = 4
FEATURE [App::DocumentObjectGroupPython] B_element001  label="B_element : 4"  # scripted group (container) (typed FeaturePython)
  n = 4
  ref = B_element
FEATURE [App::DocumentObjectGroupPython] C_element017  label="C_element : 1"  # scripted group (container) (typed FeaturePython)
  n = 1
  ref = C_element
FEATURE [App::DocumentObjectGroupPython] G4_BORON_CARBIDE  # scripted group (container) (typed FeaturePython)
  Dunit = g/cm3
  Dvalue = 2.52
  Group = -> [B_element001,C_element017]
  conduct = 2
  density = 1
  expand = 3
  formula = G4_BORON_CARBIDE
  name = G4_BORON_CARBIDE
  specific = 4
FEATURE [App::DocumentObjectGroupPython] B_element002  label="B_element : 2"  # scripted group (container) (typed FeaturePython)
  n = 2
  ref = B_element
FEATURE [App::DocumentObjectGroupPython] O_element016  label="O_element : 006"  # scripted group (container) (typed FeaturePython)
  n = 3
  ref = O_element
FEATURE [App::DocumentObjectGroupPython] G4_BORON_OXIDE  # scripted group (container) (typed FeaturePython)
  Dunit = g/cm3
  Dvalue = 1.812
  Group = -> [B_element002,O_element016]
  conduct = 2
  density = 1
  expand = 3
  formula = G4_BORON_OXIDE
  name = G4_BORON_OXIDE
  specific = 4
FEATURE [App::DocumentObjectGroupPython] H_element017  label="H_element : 0.107"  # scripted group (container) (typed FeaturePython)
  n = 0.107
FEATURE [App::DocumentObjectGroupPython] C_element018  label="C_element : 0.145"  # scripted group (container) (typed FeaturePython)
  n = 0.145
FEATURE [App::DocumentObjectGroupPython] N_element012  label="N_element : 0.022"  # scripted group (container) (typed FeaturePython)
  n = 0.022
FEATURE [App::DocumentObjectGroupPython] O_element017  label="O_element : 0.712"  # scripted group (container) (typed FeaturePython)
  n = 0.712
FEATURE [App::DocumentObjectGroupPython] Na_element004  label="Na_element : 0.004"  # scripted group (container) (typed FeaturePython)
  n = 0.002
FEATURE [App::DocumentObjectGroupPython] P_element004  label="P_element : 0.004"  # scripted group (container) (typed FeaturePython)
  n = 0.004
FEATURE [App::DocumentObjectGroupPython] S_element006  label="S_element : 0.005"  # scripted group (container) (typed FeaturePython)
  n = 0.002
FEATURE [App::DocumentObjectGroupPython] Cl_element003  label="Cl_element : 0.004"  # scripted group (container) (typed FeaturePython)
  n = 0.003
FEATURE [App::DocumentObjectGroupPython] K_element002  label="K_element : 0.003"  # scripted group (container) (typed FeaturePython)
  n = 0.003
FEATURE [App::DocumentObjectGroupPython] G4_BRAIN_ICRP  # scripted group (container) (typed FeaturePython)
  Dunit = g/cm3
  Dvalue = 1.04
  Group = -> [H_element017,C_element018,N_element012,O_element017,Na_element004,P_element004,S_element006,Cl_element003,K_element002]
  conduct = 2
  density = 1
  expand = 3
  formula = G4_BRAIN_ICRP
  name = G4_BRAIN_ICRP
  specific = 4
FEATURE [App::DocumentObjectGroupPython] C_element019  label="C_element : 4"  # scripted group (container) (typed FeaturePython)
  n = 4
  ref = C_element
FEATURE [App::DocumentObjectGroupPython] H_element018  label="H_element : 010"  # scripted group (container) (typed FeaturePython)
  n = 10
  ref = H_element
FEATURE [App::DocumentObjectGroupPython] G4_BUTANE  # scripted group (container) (typed FeaturePython)
  Dunit = g/cm3
  Dvalue = 0.00249343
  Group = -> [C_element019,H_element018]
  conduct = 2
  density = 1
  expand = 3
  formula = G4_BUTANE
  name = G4_BUTANE
  specific = 4
FEATURE [App::DocumentObjectGroupPython] C_element020  label="C_element : 008"  # scripted group (container) (typed FeaturePython)
  n = 4
  ref = C_element
FEATURE [App::DocumentObjectGroupPython] H_element019  label="H_element : 011"  # scripted group (container) (typed FeaturePython)
  n = 10
  ref = H_element
FEATURE [App::DocumentObjectGroupPython] O_element018  label="O_element : 007"  # scripted group (container) (typed FeaturePython)
  n = 1
  ref = O_element
FEATURE [App::DocumentObjectGroupPython] G4_N_BUTYL_ALCOHOL  label="G4_N-BUTYL_ALCOHOL"  # scripted group (container) (typed FeaturePython)
  Dunit = g/cm3
  Dvalue = 0.8098
  Group = -> [C_element020,H_element019,O_element018]
  conduct = 2
  density = 1
  expand = 3
  formula = G4_N-BUTYL_ALCOHOL
  name = G4_N-BUTYL_ALCOHOL
  specific = 4
FEATURE [App::DocumentObjectGroupPython] H_element020  label="H_element : 0.025"  # scripted group (container) (typed FeaturePython)
  n = 0.02468
FEATURE [App::DocumentObjectGroupPython] C_element021  label="C_element : 0.502"  # scripted group (container) (typed FeaturePython)
  n = 0.501611
FEATURE [App::DocumentObjectGroupPython] O_element019  label="O_element : 0.005"  # scripted group (container) (typed FeaturePython)
  n = 0.004527
FEATURE [App::DocumentObjectGroupPython] F_element004  label="F_element : 0.465"  # scripted group (container) (typed FeaturePython)
  n = 0.465209
FEATURE [App::DocumentObjectGroupPython] Si_element001  label="Si_element : 0.004"  # scripted group (container) (typed FeaturePython)
  n = 0.003973
FEATURE [App::DocumentObjectGroupPython] G4_C_552  label="G4_C-552"  # scripted group (container) (typed FeaturePython)
  Dunit = g/cm3
  Dvalue = 1.76
  Group = -> [H_element020,C_element021,O_element019,F_element004,Si_element001]
  conduct = 2
  density = 1
  expand = 3
  formula = G4_C-552
  name = G4_C-552
  specific = 4
FEATURE [App::DocumentObjectGroupPython] Cd_element001  label="Cd_element : 1"  # scripted group (container) (typed FeaturePython)
  n = 1
  ref = Cd_element
FEATURE [App::DocumentObjectGroupPython] Te_element001  label="Te_element : 1"  # scripted group (container) (typed FeaturePython)
  n = 1
  ref = Te_element
FEATURE [App::DocumentObjectGroupPython] G4_CADMIUM_TELLURIDE  # scripted group (container) (typed FeaturePython)
  Dunit = g/cm3
  Dvalue = 6.2
  Group = -> [Cd_element001,Te_element001]
  conduct = 2
  density = 1
  expand = 3
  formula = G4_CADMIUM_TELLURIDE
  name = G4_CADMIUM_TELLURIDE
  specific = 4
FEATURE [App::DocumentObjectGroupPython] Cd_element002  label="Cd_element : 002"  # scripted group (container) (typed FeaturePython)
  n = 1
  ref = Cd_element
FEATURE [App::DocumentObjectGroupPython] W_element001  label="W_element : 1"  # scripted group (container) (typed FeaturePython)
  n = 1
  ref = W_element
FEATURE [App::DocumentObjectGroupPython] O_element020  label="O_element : 008"  # scripted group (container) (typed FeaturePython)
  n = 4
  ref = O_element
FEATURE [App::DocumentObjectGroupPython] G4_CADMIUM_TUNGSTATE  # scripted group (container) (typed FeaturePython)
  Dunit = g/cm3
  Dvalue = 7.9
  Group = -> [Cd_element002,W_element001,O_element020]
  conduct = 2
  density = 1
  expand = 3
  formula = G4_CADMIUM_TUNGSTATE
  name = G4_CADMIUM_TUNGSTATE
  specific = 4
FEATURE [App::DocumentObjectGroupPython] Ca_element005  label="Ca_element : 1"  # scripted group (container) (typed FeaturePython)
  n = 1
  ref = Ca_element
FEATURE [App::DocumentObjectGroupPython] C_element022  label="C_element : 009"  # scripted group (container) (typed FeaturePython)
  n = 1
  ref = C_element
FEATURE [App::DocumentObjectGroupPython] O_element021  label="O_element : 009"  # scripted group (container) (typed FeaturePython)
  n = 3
  ref = O_element
FEATURE [App::DocumentObjectGroupPython] G4_CALCIUM_CARBONATE  # scripted group (container) (typed FeaturePython)
  Dunit = g/cm3
  Dvalue = 2.8
  Group = -> [Ca_element005,C_element022,O_element021]
  conduct = 2
  density = 1
  expand = 3
  formula = G4_CALCIUM_CARBONATE
  name = G4_CALCIUM_CARBONATE
  specific = 4
FEATURE [App::DocumentObjectGroupPython] Ca_element006  label="Ca_element : 002"  # scripted group (container) (typed FeaturePython)
  n = 1
  ref = Ca_element
FEATURE [App::DocumentObjectGroupPython] F_element005  label="F_element : 003"  # scripted group (container) (typed FeaturePython)
  n = 2
  ref = F_element
FEATURE [App::DocumentObjectGroupPython] G4_CALCIUM_FLUORIDE  # scripted group (container) (typed FeaturePython)
  Dunit = g/cm3
  Dvalue = 3.18
  Group = -> [Ca_element006,F_element005]
  conduct = 2
  density = 1
  expand = 3
  formula = G4_CALCIUM_FLUORIDE
  name = G4_CALCIUM_FLUORIDE
  specific = 4
FEATURE [App::DocumentObjectGroupPython] Ca_element007  label="Ca_element : 003"  # scripted group (container) (typed FeaturePython)
  n = 1
  ref = Ca_element
FEATURE [App::DocumentObjectGroupPython] O_element022  label="O_element : 010"  # scripted group (container) (typed FeaturePython)
  n = 1
  ref = O_element
FEATURE [App::DocumentObjectGroupPython] G4_CALCIUM_OXIDE  # scripted group (container) (typed FeaturePython)
  Dunit = g/cm3
  Dvalue = 3.3
  Group = -> [Ca_element007,O_element022]
  conduct = 2
  density = 1
  expand = 3
  formula = G4_CALCIUM_OXIDE
  name = G4_CALCIUM_OXIDE
  specific = 4
FEATURE [App::DocumentObjectGroupPython] Ca_element008  label="Ca_element : 004"  # scripted group (container) (typed FeaturePython)
  n = 1
  ref = Ca_element
FEATURE [App::DocumentObjectGroupPython] S_element007  label="S_element : 002"  # scripted group (container) (typed FeaturePython)
  n = 1
  ref = S_element
FEATURE [App::DocumentObjectGroupPython] O_element023  label="O_element : 011"  # scripted group (container) (typed FeaturePython)
  n = 4
  ref = O_element
FEATURE [App::DocumentObjectGroupPython] G4_CALCIUM_SULFATE  # scripted group (container) (typed FeaturePython)
  Dunit = g/cm3
  Dvalue = 2.96
  Group = -> [Ca_element008,S_element007,O_element023]
  conduct = 2
  density = 1
  expand = 3
  formula = G4_CALCIUM_SULFATE
  name = G4_CALCIUM_SULFATE
  specific = 4
FEATURE [App::DocumentObjectGroupPython] Ca_element009  label="Ca_element : 005"  # scripted group (container) (typed FeaturePython)
  n = 1
  ref = Ca_element
FEATURE [App::DocumentObjectGroupPython] W_element002  label="W_element : 002"  # scripted group (container) (typed FeaturePython)
  n = 1
  ref = W_element
FEATURE [App::DocumentObjectGroupPython] O_element024  label="O_element : 012"  # scripted group (container) (typed FeaturePython)
  n = 4
  ref = O_element
FEATURE [App::DocumentObjectGroupPython] G4_CALCIUM_TUNGSTATE  # scripted group (container) (typed FeaturePython)
  Dunit = g/cm3
  Dvalue = 6.062
  Group = -> [Ca_element009,W_element002,O_element024]
  conduct = 2
  density = 1
  expand = 3
  formula = G4_CALCIUM_TUNGSTATE
  name = G4_CALCIUM_TUNGSTATE
  specific = 4
FEATURE [App::DocumentObjectGroupPython] C_element023  label="C_element : 010"  # scripted group (container) (typed FeaturePython)
  n = 1
  ref = C_element
FEATURE [App::DocumentObjectGroupPython] O_element025  label="O_element : 013"  # scripted group (container) (typed FeaturePython)
  n = 2
  ref = O_element
FEATURE [App::DocumentObjectGroupPython] G4_CARBON_DIOXIDE  # scripted group (container) (typed FeaturePython)
  Dunit = g/cm3
  Dvalue = 0.00184212
  Group = -> [C_element023,O_element025]
  conduct = 2
  density = 1
  expand = 3
  formula = G4_CARBON_DIOXIDE
  name = G4_CARBON_DIOXIDE
  specific = 4
FEATURE [App::DocumentObjectGroupPython] C_element024  label="C_element : 011"  # scripted group (container) (typed FeaturePython)
  n = 1
  ref = C_element
FEATURE [App::DocumentObjectGroupPython] Cl_element004  label="Cl_element : 4"  # scripted group (container) (typed FeaturePython)
  n = 4
  ref = Cl_element
FEATURE [App::DocumentObjectGroupPython] G4_CARBON_TETRACHLORIDE  # scripted group (container) (typed FeaturePython)
  Dunit = g/cm3
  Dvalue = 1.594
  Group = -> [C_element024,Cl_element004]
  conduct = 2
  density = 1
  expand = 3
  formula = G4_CARBON_TETRACHLORIDE
  name = G4_CARBON_TETRACHLORIDE
  specific = 4
FEATURE [App::DocumentObjectGroupPython] C_element025  label="C_element : 012"  # scripted group (container) (typed FeaturePython)
  n = 6
  ref = C_element
FEATURE [App::DocumentObjectGroupPython] H_element021  label="H_element : 012"  # scripted group (container) (typed FeaturePython)
  n = 10
  ref = H_element
FEATURE [App::DocumentObjectGroupPython] O_element026  label="O_element : 5"  # scripted group (container) (typed FeaturePython)
  n = 5
  ref = O_element
FEATURE [App::DocumentObjectGroupPython] G4_CELLULOSE_CELLOPHANE  # scripted group (container) (typed FeaturePython)
  Dunit = g/cm3
  Dvalue = 1.42
  Group = -> [C_element025,H_element021,O_element026]
  conduct = 2
  density = 1
  expand = 3
  formula = G4_CELLULOSE_CELLOPHANE
  name = G4_CELLULOSE_CELLOPHANE
  specific = 4
FEATURE [App::DocumentObjectGroupPython] H_element022  label="H_element : 0.067"  # scripted group (container) (typed FeaturePython)
  n = 0.067125
FEATURE [App::DocumentObjectGroupPython] C_element026  label="C_element : 0.545"  # scripted group (container) (typed FeaturePython)
  n = 0.545403
FEATURE [App::DocumentObjectGroupPython] O_element027  label="O_element : 0.387"  # scripted group (container) (typed FeaturePython)
  n = 0.387472
FEATURE [App::DocumentObjectGroupPython] G4_CELLULOSE_BUTYRATE  # scripted group (container) (typed FeaturePython)
  Dunit = g/cm3
  Dvalue = 1.2
  Group = -> [H_element022,C_element026,O_element027]
  conduct = 2
  density = 1
  expand = 3
  formula = G4_CELLULOSE_BUTYRATE
  name = G4_CELLULOSE_BUTYRATE
  specific = 4
FEATURE [App::DocumentObjectGroupPython] H_element023  label="H_element : 0.029"  # scripted group (container) (typed FeaturePython)
  n = 0.029216
FEATURE [App::DocumentObjectGroupPython] C_element027  label="C_element : 0.271"  # scripted group (container) (typed FeaturePython)
  n = 0.271296
FEATURE [App::DocumentObjectGroupPython] N_element013  label="N_element : 0.121"  # scripted group (container) (typed FeaturePython)
  n = 0.121276
FEATURE [App::DocumentObjectGroupPython] O_element028  label="O_element : 0.578"  # scripted group (container) (typed FeaturePython)
  n = 0.578212
FEATURE [App::DocumentObjectGroupPython] G4_CELLULOSE_NITRATE  # scripted group (container) (typed FeaturePython)
  Dunit = g/cm3
  Dvalue = 1.49
  Group = -> [H_element023,C_element027,N_element013,O_element028]
  conduct = 2
  density = 1
  expand = 3
  formula = G4_CELLULOSE_NITRATE
  name = G4_CELLULOSE_NITRATE
  specific = 4
FEATURE [App::DocumentObjectGroupPython] H_element024  label="H_element : 0.108"  # scripted group (container) (typed FeaturePython)
  n = 0.107596
FEATURE [App::DocumentObjectGroupPython] N_element014  label="N_element : 0.001"  # scripted group (container) (typed FeaturePython)
  n = 0.0008
FEATURE [App::DocumentObjectGroupPython] O_element029  label="O_element : 0.875"  # scripted group (container) (typed FeaturePython)
  n = 0.874976
FEATURE [App::DocumentObjectGroupPython] S_element008  label="S_element : 0.015"  # scripted group (container) (typed FeaturePython)
  n = 0.014627
FEATURE [App::DocumentObjectGroupPython] Ce_element001  label="Ce_element : 0.002"  # scripted group (container) (typed FeaturePython)
  n = 0.002001
FEATURE [App::DocumentObjectGroupPython] G4_CERIC_SULFATE  # scripted group (container) (typed FeaturePython)
  Dunit = g/cm3
  Dvalue = 1.03
  Group = -> [H_element024,N_element014,O_element029,S_element008,Ce_element001]
  conduct = 2
  density = 1
  expand = 3
  formula = G4_CERIC_SULFATE
  name = G4_CERIC_SULFATE
  specific = 4
FEATURE [App::DocumentObjectGroupPython] Cs_element001  label="Cs_element : 1"  # scripted group (container) (typed FeaturePython)
  n = 1
  ref = Cs_element
FEATURE [App::DocumentObjectGroupPython] F_element006  label="F_element : 1"  # scripted group (container) (typed FeaturePython)
  n = 1
  ref = F_element
FEATURE [App::DocumentObjectGroupPython] G4_CESIUM_FLUORIDE  # scripted group (container) (typed FeaturePython)
  Dunit = g/cm3
  Dvalue = 4.115
  Group = -> [Cs_element001,F_element006]
  conduct = 2
  density = 1
  expand = 3
  formula = G4_CESIUM_FLUORIDE
  name = G4_CESIUM_FLUORIDE
  specific = 4
FEATURE [App::DocumentObjectGroupPython] Cs_element002  label="Cs_element : 002"  # scripted group (container) (typed FeaturePython)
  n = 1
  ref = Cs_element
FEATURE [App::DocumentObjectGroupPython] I_element001  label="I_element : 1"  # scripted group (container) (typed FeaturePython)
  n = 1
  ref = I_element
FEATURE [App::DocumentObjectGroupPython] G4_CESIUM_IODIDE  # scripted group (container) (typed FeaturePython)
  Dunit = g/cm3
  Dvalue = 4.51
  Group = -> [Cs_element002,I_element001]
  conduct = 2
  density = 1
  expand = 3
  formula = G4_CESIUM_IODIDE
  name = G4_CESIUM_IODIDE
  specific = 4
FEATURE [App::DocumentObjectGroupPython] C_element028  label="C_element : 013"  # scripted group (container) (typed FeaturePython)
  n = 6
  ref = C_element
FEATURE [App::DocumentObjectGroupPython] H_element025  label="H_element : 013"  # scripted group (container) (typed FeaturePython)
  n = 5
  ref = H_element
FEATURE [App::DocumentObjectGroupPython] Cl_element005  label="Cl_element : 1"  # scripted group (container) (typed FeaturePython)
  n = 1
  ref = Cl_element
FEATURE [App::DocumentObjectGroupPython] G4_CHLOROBENZENE  # scripted group (container) (typed FeaturePython)
  Dunit = g/cm3
  Dvalue = 1.1058
  Group = -> [C_element028,H_element025,Cl_element005]
  conduct = 2
  density = 1
  expand = 3
  formula = G4_CHLOROBENZENE
  name = G4_CHLOROBENZENE
  specific = 4
FEATURE [App::DocumentObjectGroupPython] C_element029  label="C_element : 014"  # scripted group (container) (typed FeaturePython)
  n = 1
  ref = C_element
FEATURE [App::DocumentObjectGroupPython] H_element026  label="H_element : 1"  # scripted group (container) (typed FeaturePython)
  n = 1
  ref = H_element
FEATURE [App::DocumentObjectGroupPython] Cl_element006  label="Cl_element : 3"  # scripted group (container) (typed FeaturePython)
  n = 3
  ref = Cl_element
FEATURE [App::DocumentObjectGroupPython] G4_CHLOROFORM  # scripted group (container) (typed FeaturePython)
  Dunit = g/cm3
  Dvalue = 1.4832
  Group = -> [C_element029,H_element026,Cl_element006]
  conduct = 2
  density = 1
  expand = 3
  formula = G4_CHLOROFORM
  name = G4_CHLOROFORM
  specific = 4
FEATURE [App::DocumentObjectGroupPython] H_element027  label="H_element : 0.010"  # scripted group (container) (typed FeaturePython)
  n = 0.01
FEATURE [App::DocumentObjectGroupPython] C_element030  label="C_element : 0.001"  # scripted group (container) (typed FeaturePython)
  n = 0.001
FEATURE [App::DocumentObjectGroupPython] O_element030  label="O_element : 0.529"  # scripted group (container) (typed FeaturePython)
  n = 0.529107
FEATURE [App::DocumentObjectGroupPython] Na_element005  label="Na_element : 0.016"  # scripted group (container) (typed FeaturePython)
  n = 0.016
FEATURE [App::DocumentObjectGroupPython] Mg_element003  label="Mg_element : 0.004"  # scripted group (container) (typed FeaturePython)
  n = 0.002
FEATURE [App::DocumentObjectGroupPython] Al_element002  label="Al_element : 0.034"  # scripted group (container) (typed FeaturePython)
  n = 0.033872
FEATURE [App::DocumentObjectGroupPython] Si_element002  label="Si_element : 0.337"  # scripted group (container) (typed FeaturePython)
  n = 0.337021
FEATURE [App::DocumentObjectGroupPython] K_element003  label="K_element : 0.013"  # scripted group (container) (typed FeaturePython)
  n = 0.013
FEATURE [App::DocumentObjectGroupPython] Ca_element010  label="Ca_element : 0.044"  # scripted group (container) (typed FeaturePython)
  n = 0.044
FEATURE [App::DocumentObjectGroupPython] Fe_element002  label="Fe_element : 0.014"  # scripted group (container) (typed FeaturePython)
  n = 0.014
FEATURE [App::DocumentObjectGroupPython] G4_CONCRETE  # scripted group (container) (typed FeaturePython)
  Dunit = g/cm3
  Dvalue = 2.3
  Group = -> [H_element027,C_element030,O_element030,Na_element005,Mg_element003,Al_element002,Si_element002,K_element003,Ca_element010,Fe_element002]
  conduct = 2
  density = 1
  expand = 3
  formula = G4_CONCRETE
  name = G4_CONCRETE
  specific = 4
FEATURE [App::DocumentObjectGroupPython] C_element031  label="C_element : 015"  # scripted group (container) (typed FeaturePython)
  n = 6
  ref = C_element
FEATURE [App::DocumentObjectGroupPython] H_element028  label="H_element : 12"  # scripted group (container) (typed FeaturePython)
  n = 12
  ref = H_element
FEATURE [App::DocumentObjectGroupPython] G4_CYCLOHEXANE  # scripted group (container) (typed FeaturePython)
  Dunit = g/cm3
  Dvalue = 0.779
  Group = -> [C_element031,H_element028]
  conduct = 2
  density = 1
  expand = 3
  formula = G4_CYCLOHEXANE
  name = G4_CYCLOHEXANE
  specific = 4
FEATURE [App::DocumentObjectGroupPython] C_element032  label="C_element : 016"  # scripted group (container) (typed FeaturePython)
  n = 6
  ref = C_element
FEATURE [App::DocumentObjectGroupPython] H_element029  label="H_element : 4"  # scripted group (container) (typed FeaturePython)
  n = 4
  ref = H_element
FEATURE [App::DocumentObjectGroupPython] Cl_element007  label="Cl_element : 2"  # scripted group (container) (typed FeaturePython)
  n = 2
  ref = Cl_element
FEATURE [App::DocumentObjectGroupPython] G4_1_2_DICHLOROBENZENE  label="G4_1.2-DICHLOROBENZENE"  # scripted group (container) (typed FeaturePython)
  Dunit = g/cm3
  Dvalue = 1.3048
  Group = -> [C_element032,H_element029,Cl_element007]
  conduct = 2
  density = 1
  expand = 3
  formula = G4_1.2-DICHLOROBENZENE
  name = G4_1.2-DICHLOROBENZENE
  specific = 4
FEATURE [App::DocumentObjectGroupPython] C_element033  label="C_element : 017"  # scripted group (container) (typed FeaturePython)
  n = 4
  ref = C_element
FEATURE [App::DocumentObjectGroupPython] H_element030  label="H_element : 8"  # scripted group (container) (typed FeaturePython)
  n = 8
  ref = H_element
FEATURE [App::DocumentObjectGroupPython] O_element031  label="O_element : 014"  # scripted group (container) (typed FeaturePython)
  n = 1
  ref = O_element
FEATURE [App::DocumentObjectGroupPython] Cl_element008  label="Cl_element : 005"  # scripted group (container) (typed FeaturePython)
  n = 2
  ref = Cl_element
FEATURE [App::DocumentObjectGroupPython] G4_DICHLORODIETHYL_ETHER  # scripted group (container) (typed FeaturePython)
  Dunit = g/cm3
  Dvalue = 1.2199
  Group = -> [C_element033,H_element030,O_element031,Cl_element008]
  conduct = 2
  density = 1
  expand = 3
  formula = G4_DICHLORODIETHYL_ETHER
  name = G4_DICHLORODIETHYL_ETHER
  specific = 4
FEATURE [App::DocumentObjectGroupPython] C_element034  label="C_element : 018"  # scripted group (container) (typed FeaturePython)
  n = 2
  ref = C_element
FEATURE [App::DocumentObjectGroupPython] H_element031  label="H_element : 014"  # scripted group (container) (typed FeaturePython)
  n = 4
  ref = H_element
FEATURE [App::DocumentObjectGroupPython] Cl_element009  label="Cl_element : 006"  # scripted group (container) (typed FeaturePython)
  n = 2
  ref = Cl_element
FEATURE [App::DocumentObjectGroupPython] G4_1_2_DICHLOROETHANE  label="G4_1.2-DICHLOROETHANE"  # scripted group (container) (typed FeaturePython)
  Dunit = g/cm3
  Dvalue = 1.2351
  Group = -> [C_element034,H_element031,Cl_element009]
  conduct = 2
  density = 1
  expand = 3
  formula = G4_1.2-DICHLOROETHANE
  name = G4_1.2-DICHLOROETHANE
  specific = 4
FEATURE [App::DocumentObjectGroupPython] C_element035  label="C_element : 019"  # scripted group (container) (typed FeaturePython)
  n = 4
  ref = C_element
FEATURE [App::DocumentObjectGroupPython] H_element032  label="H_element : 015"  # scripted group (container) (typed FeaturePython)
  n = 10
  ref = H_element
FEATURE [App::DocumentObjectGroupPython] O_element032  label="O_element : 015"  # scripted group (container) (typed FeaturePython)
  n = 1
  ref = O_element
FEATURE [App::DocumentObjectGroupPython] G4_DIETHYL_ETHER  # scripted group (container) (typed FeaturePython)
  Dunit = g/cm3
  Dvalue = 0.71378
  Group = -> [C_element035,H_element032,O_element032]
  conduct = 2
  density = 1
  expand = 3
  formula = G4_DIETHYL_ETHER
  name = G4_DIETHYL_ETHER
  specific = 4
FEATURE [App::DocumentObjectGroupPython] C_element036  label="C_element : 020"  # scripted group (container) (typed FeaturePython)
  n = 3
  ref = C_element
FEATURE [App::DocumentObjectGroupPython] H_element033  label="H_element : 016"  # scripted group (container) (typed FeaturePython)
  n = 7
  ref = H_element
FEATURE [App::DocumentObjectGroupPython] N_element015  label="N_element : 008"  # scripted group (container) (typed FeaturePython)
  n = 1
  ref = N_element
FEATURE [App::DocumentObjectGroupPython] O_element033  label="O_element : 016"  # scripted group (container) (typed FeaturePython)
  n = 1
  ref = O_element
FEATURE [App::DocumentObjectGroupPython] G4_N_N_DIMETHYL_FORMAMIDE  label="G4_N.N-DIMETHYL_FORMAMIDE"  # scripted group (container) (typed FeaturePython)
  Dunit = g/cm3
  Dvalue = 0.9487
  Group = -> [C_element036,H_element033,N_element015,O_element033]
  conduct = 2
  density = 1
  expand = 3
  formula = G4_N.N-DIMETHYL_FORMAMIDE
  name = G4_N.N-DIMETHYL_FORMAMIDE
  specific = 4
FEATURE [App::DocumentObjectGroupPython] C_element037  label="C_element : 021"  # scripted group (container) (typed FeaturePython)
  n = 2
  ref = C_element
FEATURE [App::DocumentObjectGroupPython] H_element034  label="H_element : 017"  # scripted group (container) (typed FeaturePython)
  n = 6
  ref = H_element
FEATURE [App::DocumentObjectGroupPython] O_element034  label="O_element : 017"  # scripted group (container) (typed FeaturePython)
  n = 1
  ref = O_element
FEATURE [App::DocumentObjectGroupPython] S_element009  label="S_element : 003"  # scripted group (container) (typed FeaturePython)
  n = 1
  ref = S_element
FEATURE [App::DocumentObjectGroupPython] G4_DIMETHYL_SULFOXIDE  # scripted group (container) (typed FeaturePython)
  Dunit = g/cm3
  Dvalue = 1.1014
  Group = -> [C_element037,H_element034,O_element034,S_element009]
  conduct = 2
  density = 1
  expand = 3
  formula = G4_DIMETHYL_SULFOXIDE
  name = G4_DIMETHYL_SULFOXIDE
  specific = 4
FEATURE [App::DocumentObjectGroupPython] C_element038  label="C_element : 022"  # scripted group (container) (typed FeaturePython)
  n = 2
  ref = C_element
FEATURE [App::DocumentObjectGroupPython] H_element035  label="H_element : 018"  # scripted group (container) (typed FeaturePython)
  n = 6
  ref = H_element
FEATURE [App::DocumentObjectGroupPython] G4_ETHANE  # scripted group (container) (typed FeaturePython)
  Dunit = g/cm3
  Dvalue = 0.00125324
  Group = -> [C_element038,H_element035]
  conduct = 2
  density = 1
  expand = 3
  formula = G4_ETHANE
  name = G4_ETHANE
  specific = 4
FEATURE [App::DocumentObjectGroupPython] C_element039  label="C_element : 023"  # scripted group (container) (typed FeaturePython)
  n = 2
  ref = C_element
FEATURE [App::DocumentObjectGroupPython] H_element036  label="H_element : 019"  # scripted group (container) (typed FeaturePython)
  n = 6
  ref = H_element
FEATURE [App::DocumentObjectGroupPython] O_element035  label="O_element : 018"  # scripted group (container) (typed FeaturePython)
  n = 1
  ref = O_element
FEATURE [App::DocumentObjectGroupPython] G4_ETHYL_ALCOHOL  # scripted group (container) (typed FeaturePython)
  Dunit = g/cm3
  Dvalue = 0.7893
  Group = -> [C_element039,H_element036,O_element035]
  conduct = 2
  density = 1
  expand = 3
  formula = G4_ETHYL_ALCOHOL
  name = G4_ETHYL_ALCOHOL
  specific = 4
FEATURE [App::DocumentObjectGroupPython] H_element037  label="H_element : 0.090"  # scripted group (container) (typed FeaturePython)
  n = 0.090027
FEATURE [App::DocumentObjectGroupPython] C_element040  label="C_element : 0.585"  # scripted group (container) (typed FeaturePython)
  n = 0.585182
FEATURE [App::DocumentObjectGroupPython] O_element036  label="O_element : 0.325"  # scripted group (container) (typed FeaturePython)
  n = 0.324791
FEATURE [App::DocumentObjectGroupPython] G4_ETHYL_CELLULOSE  # scripted group (container) (typed FeaturePython)
  Dunit = g/cm3
  Dvalue = 1.13
  Group = -> [H_element037,C_element040,O_element036]
  conduct = 2
  density = 1
  expand = 3
  formula = G4_ETHYL_CELLULOSE
  name = G4_ETHYL_CELLULOSE
  specific = 4
FEATURE [App::DocumentObjectGroupPython] C_element041  label="C_element : 024"  # scripted group (container) (typed FeaturePython)
  n = 2
  ref = C_element
FEATURE [App::DocumentObjectGroupPython] H_element038  label="H_element : 020"  # scripted group (container) (typed FeaturePython)
  n = 4
  ref = H_element
FEATURE [App::DocumentObjectGroupPython] G4_ETHYLENE  # scripted group (container) (typed FeaturePython)
  Dunit = g/cm3
  Dvalue = 0.00117497
  Group = -> [C_element041,H_element038]
  conduct = 2
  density = 1
  expand = 3
  formula = G4_ETHYLENE
  name = G4_ETHYLENE
  specific = 4
FEATURE [App::DocumentObjectGroupPython] H_element039  label="H_element : 0.096"  # scripted group (container) (typed FeaturePython)
  n = 0.096
FEATURE [App::DocumentObjectGroupPython] C_element042  label="C_element : 0.195"  # scripted group (container) (typed FeaturePython)
  n = 0.195
FEATURE [App::DocumentObjectGroupPython] N_element016  label="N_element : 0.057"  # scripted group (container) (typed FeaturePython)
  n = 0.057
FEATURE [App::DocumentObjectGroupPython] O_element037  label="O_element : 0.646"  # scripted group (container) (typed FeaturePython)
  n = 0.646
FEATURE [App::DocumentObjectGroupPython] Na_element006  label="Na_element : 0.017"  # scripted group (container) (typed FeaturePython)
  n = 0.001
FEATURE [App::DocumentObjectGroupPython] P_element005  label="P_element : 0.104"  # scripted group (container) (typed FeaturePython)
  n = 0.001
FEATURE [App::DocumentObjectGroupPython] S_element010  label="S_element : 0.016"  # scripted group (container) (typed FeaturePython)
  n = 0.003
FEATURE [App::DocumentObjectGroupPython] Cl_element010  label="Cl_element : 0.005"  # scripted group (container) (typed FeaturePython)
  n = 0.001
FEATURE [App::DocumentObjectGroupPython] G4_EYE_LENS_ICRP  # scripted group (container) (typed FeaturePython)
  Dunit = g/cm3
  Dvalue = 1.07
  Group = -> [H_element039,C_element042,N_element016,O_element037,Na_element006,P_element005,S_element010,Cl_element010]
  conduct = 2
  density = 1
  expand = 3
  formula = G4_EYE_LENS_ICRP
  name = G4_EYE_LENS_ICRP
  specific = 4
FEATURE [App::DocumentObjectGroupPython] Fe_element003  label="Fe_element : 2"  # scripted group (container) (typed FeaturePython)
  n = 2
  ref = Fe_element
FEATURE [App::DocumentObjectGroupPython] O_element038  label="O_element : 019"  # scripted group (container) (typed FeaturePython)
  n = 3
  ref = O_element
FEATURE [App::DocumentObjectGroupPython] G4_FERRIC_OXIDE  # scripted group (container) (typed FeaturePython)
  Dunit = g/cm3
  Dvalue = 5.2
  Group = -> [Fe_element003,O_element038]
  conduct = 2
  density = 1
  expand = 3
  formula = G4_FERRIC_OXIDE
  name = G4_FERRIC_OXIDE
  specific = 4
FEATURE [App::DocumentObjectGroupPython] Fe_element004  label="Fe_element : 1"  # scripted group (container) (typed FeaturePython)
  n = 1
  ref = Fe_element
FEATURE [App::DocumentObjectGroupPython] B_element003  label="B_element : 1"  # scripted group (container) (typed FeaturePython)
  n = 1
  ref = B_element
FEATURE [App::DocumentObjectGroupPython] G4_FERROBORIDE  # scripted group (container) (typed FeaturePython)
  Dunit = g/cm3
  Dvalue = 7.15
  Group = -> [Fe_element004,B_element003]
  conduct = 2
  density = 1
  expand = 3
  formula = G4_FERROBORIDE
  name = G4_FERROBORIDE
  specific = 4
FEATURE [App::DocumentObjectGroupPython] Fe_element005  label="Fe_element : 003"  # scripted group (container) (typed FeaturePython)
  n = 1
  ref = Fe_element
FEATURE [App::DocumentObjectGroupPython] O_element039  label="O_element : 020"  # scripted group (container) (typed FeaturePython)
  n = 1
  ref = O_element
FEATURE [App::DocumentObjectGroupPython] G4_FERROUS_OXIDE  # scripted group (container) (typed FeaturePython)
  Dunit = g/cm3
  Dvalue = 5.7
  Group = -> [Fe_element005,O_element039]
  conduct = 2
  density = 1
  expand = 3
  formula = G4_FERROUS_OXIDE
  name = G4_FERROUS_OXIDE
  specific = 4
FEATURE [App::DocumentObjectGroupPython] H_element040  label="H_element : 0.115"  # scripted group (container) (typed FeaturePython)
  n = 0.108259
FEATURE [App::DocumentObjectGroupPython] N_element017  label="N_element : 0.000"  # scripted group (container) (typed FeaturePython)
  n = 2.7e-05
FEATURE [App::DocumentObjectGroupPython] O_element040  label="O_element : 0.879"  # scripted group (container) (typed FeaturePython)
  n = 0.878636
FEATURE [App::DocumentObjectGroupPython] Na_element007  label="Na_element : 0.000"  # scripted group (container) (typed FeaturePython)
  n = 2.2e-05
FEATURE [App::DocumentObjectGroupPython] S_element011  label="S_element : 0.013"  # scripted group (container) (typed FeaturePython)
  n = 0.012968
FEATURE [App::DocumentObjectGroupPython] Cl_element011  label="Cl_element : 0.000"  # scripted group (container) (typed FeaturePython)
  n = 3.4e-05
FEATURE [App::DocumentObjectGroupPython] Fe_element006  label="Fe_element : 0.000"  # scripted group (container) (typed FeaturePython)
  n = 5.4e-05
FEATURE [App::DocumentObjectGroupPython] G4_FERROUS_SULFATE  # scripted group (container) (typed FeaturePython)
  Dunit = g/cm3
  Dvalue = 1.024
  Group = -> [H_element040,N_element017,O_element040,Na_element007,S_element011,Cl_element011,Fe_element006]
  conduct = 2
  density = 1
  expand = 3
  formula = G4_FERROUS_SULFATE
  name = G4_FERROUS_SULFATE
  specific = 4
FEATURE [App::DocumentObjectGroupPython] C_element043  label="C_element : 0.099"  # scripted group (container) (typed FeaturePython)
  n = 0.099335
FEATURE [App::DocumentObjectGroupPython] F_element007  label="F_element : 0.314"  # scripted group (container) (typed FeaturePython)
  n = 0.314247
FEATURE [App::DocumentObjectGroupPython] Cl_element012  label="Cl_element : 0.586"  # scripted group (container) (typed FeaturePython)
  n = 0.586418
FEATURE [App::DocumentObjectGroupPython] G4_FREON_12  label="G4_FREON-12"  # scripted group (container) (typed FeaturePython)
  Dunit = g/cm3
  Dvalue = 1.12
  Group = -> [C_element043,F_element007,Cl_element012]
  conduct = 2
  density = 1
  expand = 3
  formula = G4_FREON-12
  name = G4_FREON-12
  specific = 4
FEATURE [App::DocumentObjectGroupPython] C_element044  label="C_element : 0.057"  # scripted group (container) (typed FeaturePython)
  n = 0.057245
FEATURE [App::DocumentObjectGroupPython] F_element008  label="F_element : 0.181"  # scripted group (container) (typed FeaturePython)
  n = 0.181096
FEATURE [App::DocumentObjectGroupPython] Br_element001  label="Br_element : 0.762"  # scripted group (container) (typed FeaturePython)
  n = 0.761659
FEATURE [App::DocumentObjectGroupPython] G4_FREON_12B2  label="G4_FREON-12B2"  # scripted group (container) (typed FeaturePython)
  Dunit = g/cm3
  Dvalue = 1.8
  Group = -> [C_element044,F_element008,Br_element001]
  conduct = 2
  density = 1
  expand = 3
  formula = G4_FREON-12B2
  name = G4_FREON-12B2
  specific = 4
FEATURE [App::DocumentObjectGroupPython] C_element045  label="C_element : 0.115"  # scripted group (container) (typed FeaturePython)
  n = 0.114983
FEATURE [App::DocumentObjectGroupPython] F_element009  label="F_element : 0.546"  # scripted group (container) (typed FeaturePython)
  n = 0.545621
FEATURE [App::DocumentObjectGroupPython] Cl_element013  label="Cl_element : 0.339"  # scripted group (container) (typed FeaturePython)
  n = 0.339396
FEATURE [App::DocumentObjectGroupPython] G4_FREON_13  label="G4_FREON-13"  # scripted group (container) (typed FeaturePython)
  Dunit = g/cm3
  Dvalue = 0.95
  Group = -> [C_element045,F_element009,Cl_element013]
  conduct = 2
  density = 1
  expand = 3
  formula = G4_FREON-13
  name = G4_FREON-13
  specific = 4
FEATURE [App::DocumentObjectGroupPython] C_element046  label="C_element : 025"  # scripted group (container) (typed FeaturePython)
  n = 1
  ref = C_element
FEATURE [App::DocumentObjectGroupPython] F_element010  label="F_element : 3"  # scripted group (container) (typed FeaturePython)
  n = 3
  ref = F_element
FEATURE [App::DocumentObjectGroupPython] Br_element002  label="Br_element : 1"  # scripted group (container) (typed FeaturePython)
  n = 1
  ref = Br_element
FEATURE [App::DocumentObjectGroupPython] G4_FREON_13B1  label="G4_FREON-13B1"  # scripted group (container) (typed FeaturePython)
  Dunit = g/cm3
  Dvalue = 1.5
  Group = -> [C_element046,F_element010,Br_element002]
  conduct = 2
  density = 1
  expand = 3
  formula = G4_FREON-13B1
  name = G4_FREON-13B1
  specific = 4
FEATURE [App::DocumentObjectGroupPython] C_element047  label="C_element : 0.061"  # scripted group (container) (typed FeaturePython)
  n = 0.061309
FEATURE [App::DocumentObjectGroupPython] F_element011  label="F_element : 0.291"  # scripted group (container) (typed FeaturePython)
  n = 0.290924
FEATURE [App::DocumentObjectGroupPython] I_element002  label="I_element : 0.648"  # scripted group (container) (typed FeaturePython)
  n = 0.647767
FEATURE [App::DocumentObjectGroupPython] G4_FREON_13I1  label="G4_FREON-13I1"  # scripted group (container) (typed FeaturePython)
  Dunit = g/cm3
  Dvalue = 1.8
  Group = -> [C_element047,F_element011,I_element002]
  conduct = 2
  density = 1
  expand = 3
  formula = G4_FREON-13I1
  name = G4_FREON-13I1
  specific = 4
FEATURE [App::DocumentObjectGroupPython] Gd_element001  label="Gd_element : 2"  # scripted group (container) (typed FeaturePython)
  n = 2
  ref = Gd_element
FEATURE [App::DocumentObjectGroupPython] O_element041  label="O_element : 021"  # scripted group (container) (typed FeaturePython)
  n = 2
  ref = O_element
FEATURE [App::DocumentObjectGroupPython] S_element012  label="S_element : 004"  # scripted group (container) (typed FeaturePython)
  n = 1
  ref = S_element
FEATURE [App::DocumentObjectGroupPython] G4_GADOLINIUM_OXYSULFIDE  # scripted group (container) (typed FeaturePython)
  Dunit = g/cm3
  Dvalue = 7.44
  Group = -> [Gd_element001,O_element041,S_element012]
  conduct = 2
  density = 1
  expand = 3
  formula = G4_GADOLINIUM_OXYSULFIDE
  name = G4_GADOLINIUM_OXYSULFIDE
  specific = 4
FEATURE [App::DocumentObjectGroupPython] Ga_element001  label="Ga_element : 1"  # scripted group (container) (typed FeaturePython)
  n = 1
  ref = Ga_element
FEATURE [App::DocumentObjectGroupPython] As_element001  label="As_element : 1"  # scripted group (container) (typed FeaturePython)
  n = 1
  ref = As_element
FEATURE [App::DocumentObjectGroupPython] G4_GALLIUM_ARSENIDE  # scripted group (container) (typed FeaturePython)
  Dunit = g/cm3
  Dvalue = 5.31
  Group = -> [Ga_element001,As_element001]
  conduct = 2
  density = 1
  expand = 3
  formula = G4_GALLIUM_ARSENIDE
  name = G4_GALLIUM_ARSENIDE
  specific = 4
FEATURE [App::DocumentObjectGroupPython] H_element041  label="H_element : 0.081"  # scripted group (container) (typed FeaturePython)
  n = 0.08118
FEATURE [App::DocumentObjectGroupPython] C_element048  label="C_element : 0.416"  # scripted group (container) (typed FeaturePython)
  n = 0.41606
FEATURE [App::DocumentObjectGroupPython] N_element018  label="N_element : 0.111"  # scripted group (container) (typed FeaturePython)
  n = 0.11124
FEATURE [App::DocumentObjectGroupPython] O_element042  label="O_element : 0.381"  # scripted group (container) (typed FeaturePython)
  n = 0.38064
FEATURE [App::DocumentObjectGroupPython] S_element013  label="S_element : 0.011"  # scripted group (container) (typed FeaturePython)
  n = 0.01088
FEATURE [App::DocumentObjectGroupPython] G4_GEL_PHOTO_EMULSION  # scripted group (container) (typed FeaturePython)
  Dunit = g/cm3
  Dvalue = 1.2914
  Group = -> [H_element041,C_element048,N_element018,O_element042,S_element013]
  conduct = 2
  density = 1
  expand = 3
  formula = G4_GEL_PHOTO_EMULSION
  name = G4_GEL_PHOTO_EMULSION
  specific = 4
FEATURE [App::DocumentObjectGroupPython] B_element004  label="B_element : 0.040"  # scripted group (container) (typed FeaturePython)
  n = 0.0400639
FEATURE [App::DocumentObjectGroupPython] O_element043  label="O_element : 0.540"  # scripted group (container) (typed FeaturePython)
  n = 0.539561
FEATURE [App::DocumentObjectGroupPython] Na_element008  label="Na_element : 0.028"  # scripted group (container) (typed FeaturePython)
  n = 0.0281909
FEATURE [App::DocumentObjectGroupPython] Al_element003  label="Al_element : 0.012"  # scripted group (container) (typed FeaturePython)
  n = 0.011644
FEATURE [App::DocumentObjectGroupPython] Si_element003  label="Si_element : 0.377"  # scripted group (container) (typed FeaturePython)
  n = 0.377219
FEATURE [App::DocumentObjectGroupPython] K_element004  label="K_element : 0.014"  # scripted group (container) (typed FeaturePython)
  n = 0.00332099
FEATURE [App::DocumentObjectGroupPython] G4_Pyrex_Glass  # scripted group (container) (typed FeaturePython)
  Dunit = g/cm3
  Dvalue = 2.23
  Group = -> [B_element004,O_element043,Na_element008,Al_element003,Si_element003,K_element004]
  conduct = 2
  density = 1
  expand = 3
  formula = G4_Pyrex_Glass
  name = G4_Pyrex_Glass
  specific = 4
FEATURE [App::DocumentObjectGroupPython] O_element044  label="O_element : 0.156"  # scripted group (container) (typed FeaturePython)
  n = 0.156453
FEATURE [App::DocumentObjectGroupPython] Si_element004  label="Si_element : 0.081"  # scripted group (container) (typed FeaturePython)
  n = 0.080866
FEATURE [App::DocumentObjectGroupPython] Ti_element001  label="Ti_element : 0.008"  # scripted group (container) (typed FeaturePython)
  n = 0.008092
FEATURE [App::DocumentObjectGroupPython] As_element002  label="As_element : 0.003"  # scripted group (container) (typed FeaturePython)
  n = 0.002651
FEATURE [App::DocumentObjectGroupPython] Pb_element001  label="Pb_element : 0.752"  # scripted group (container) (typed FeaturePython)
  n = 0.751938
FEATURE [App::DocumentObjectGroupPython] G4_GLASS_LEAD  # scripted group (container) (typed FeaturePython)
  Dunit = g/cm3
  Dvalue = 6.22
  Group = -> [O_element044,Si_element004,Ti_element001,As_element002,Pb_element001]
  conduct = 2
  density = 1
  expand = 3
  formula = G4_GLASS_LEAD
  name = G4_GLASS_LEAD
  specific = 4
FEATURE [App::DocumentObjectGroupPython] O_element045  label="O_element : 0.460"  # scripted group (container) (typed FeaturePython)
  n = 0.4598
FEATURE [App::DocumentObjectGroupPython] Na_element009  label="Na_element : 0.096"  # scripted group (container) (typed FeaturePython)
  n = 0.0964411
FEATURE [App::DocumentObjectGroupPython] Si_element005  label="Si_element : 0.378"  # scripted group (container) (typed FeaturePython)
  n = 0.336553
FEATURE [App::DocumentObjectGroupPython] Ca_element011  label="Ca_element : 0.107"  # scripted group (container) (typed FeaturePython)
  n = 0.107205
FEATURE [App::DocumentObjectGroupPython] G4_GLASS_PLATE  # scripted group (container) (typed FeaturePython)
  Dunit = g/cm3
  Dvalue = 2.4
  Group = -> [O_element045,Na_element009,Si_element005,Ca_element011]
  conduct = 2
  density = 1
  expand = 3
  formula = G4_GLASS_PLATE
  name = G4_GLASS_PLATE
  specific = 4
FEATURE [App::DocumentObjectGroupPython] C_element049  label="C_element : 026"  # scripted group (container) (typed FeaturePython)
  n = 5
  ref = C_element
FEATURE [App::DocumentObjectGroupPython] H_element042  label="H_element : 021"  # scripted group (container) (typed FeaturePython)
  n = 10
  ref = H_element
FEATURE [App::DocumentObjectGroupPython] N_element019  label="N_element : 2"  # scripted group (container) (typed FeaturePython)
  n = 2
  ref = N_element
FEATURE [App::DocumentObjectGroupPython] O_element046  label="O_element : 022"  # scripted group (container) (typed FeaturePython)
  n = 3
  ref = O_element
FEATURE [App::DocumentObjectGroupPython] G4_GLUTAMINE  # scripted group (container) (typed FeaturePython)
  Dunit = g/cm3
  Dvalue = 1.46
  Group = -> [C_element049,H_element042,N_element019,O_element046]
  conduct = 2
  density = 1
  expand = 3
  formula = G4_GLUTAMINE
  name = G4_GLUTAMINE
  specific = 4
FEATURE [App::DocumentObjectGroupPython] C_element050  label="C_element : 027"  # scripted group (container) (typed FeaturePython)
  n = 3
  ref = C_element
FEATURE [App::DocumentObjectGroupPython] H_element043  label="H_element : 022"  # scripted group (container) (typed FeaturePython)
  n = 8
  ref = H_element
FEATURE [App::DocumentObjectGroupPython] O_element047  label="O_element : 023"  # scripted group (container) (typed FeaturePython)
  n = 3
  ref = O_element
FEATURE [App::DocumentObjectGroupPython] G4_GLYCEROL  # scripted group (container) (typed FeaturePython)
  Dunit = g/cm3
  Dvalue = 1.2613
  Group = -> [C_element050,H_element043,O_element047]
  conduct = 2
  density = 1
  expand = 3
  formula = G4_GLYCEROL
  name = G4_GLYCEROL
  specific = 4
FEATURE [App::DocumentObjectGroupPython] C_element051  label="C_element : 028"  # scripted group (container) (typed FeaturePython)
  n = 5
  ref = C_element
FEATURE [App::DocumentObjectGroupPython] H_element044  label="H_element : 023"  # scripted group (container) (typed FeaturePython)
  n = 5
  ref = H_element
FEATURE [App::DocumentObjectGroupPython] N_element020  label="N_element : 009"  # scripted group (container) (typed FeaturePython)
  n = 5
  ref = N_element
FEATURE [App::DocumentObjectGroupPython] O_element048  label="O_element : 024"  # scripted group (container) (typed FeaturePython)
  n = 1
  ref = O_element
FEATURE [App::DocumentObjectGroupPython] G4_GUANINE  # scripted group (container) (typed FeaturePython)
  Dunit = g/cm3
  Dvalue = 2.2
  Group = -> [C_element051,H_element044,N_element020,O_element048]
  conduct = 2
  density = 1
  expand = 3
  formula = G4_GUANINE
  name = G4_GUANINE
  specific = 4
FEATURE [App::DocumentObjectGroupPython] Ca_element012  label="Ca_element : 006"  # scripted group (container) (typed FeaturePython)
  n = 1
  ref = Ca_element
FEATURE [App::DocumentObjectGroupPython] S_element014  label="S_element : 005"  # scripted group (container) (typed FeaturePython)
  n = 1
  ref = S_element
FEATURE [App::DocumentObjectGroupPython] O_element049  label="O_element : 6"  # scripted group (container) (typed FeaturePython)
  n = 6
  ref = O_element
FEATURE [App::DocumentObjectGroupPython] H_element045  label="H_element : 024"  # scripted group (container) (typed FeaturePython)
  n = 4
  ref = H_element
FEATURE [App::DocumentObjectGroupPython] G4_GYPSUM  # scripted group (container) (typed FeaturePython)
  Dunit = g/cm3
  Dvalue = 2.32
  Group = -> [Ca_element012,S_element014,O_element049,H_element045]
  conduct = 2
  density = 1
  expand = 3
  formula = G4_GYPSUM
  name = G4_GYPSUM
  specific = 4
FEATURE [App::DocumentObjectGroupPython] C_element052  label="C_element : 7"  # scripted group (container) (typed FeaturePython)
  n = 7
  ref = C_element
FEATURE [App::DocumentObjectGroupPython] H_element046  label="H_element : 16"  # scripted group (container) (typed FeaturePython)
  n = 16
  ref = H_element
FEATURE [App::DocumentObjectGroupPython] G4_N_HEPTANE  label="G4_N-HEPTANE"  # scripted group (container) (typed FeaturePython)
  Dunit = g/cm3
  Dvalue = 0.68376
  Group = -> [C_element052,H_element046]
  conduct = 2
  density = 1
  expand = 3
  formula = G4_N-HEPTANE
  name = G4_N-HEPTANE
  specific = 4
FEATURE [App::DocumentObjectGroupPython] C_element053  label="C_element : 029"  # scripted group (container) (typed FeaturePython)
  n = 6
  ref = C_element
FEATURE [App::DocumentObjectGroupPython] H_element047  label="H_element : 14"  # scripted group (container) (typed FeaturePython)
  n = 14
  ref = H_element
FEATURE [App::DocumentObjectGroupPython] G4_N_HEXANE  label="G4_N-HEXANE"  # scripted group (container) (typed FeaturePython)
  Dunit = g/cm3
  Dvalue = 0.6603
  Group = -> [C_element053,H_element047]
  conduct = 2
  density = 1
  expand = 3
  formula = G4_N-HEXANE
  name = G4_N-HEXANE
  specific = 4
FEATURE [App::DocumentObjectGroupPython] C_element054  label="C_element : 22"  # scripted group (container) (typed FeaturePython)
  n = 22
  ref = C_element
FEATURE [App::DocumentObjectGroupPython] H_element048  label="H_element : 025"  # scripted group (container) (typed FeaturePython)
  n = 10
  ref = H_element
FEATURE [App::DocumentObjectGroupPython] N_element021  label="N_element : 010"  # scripted group (container) (typed FeaturePython)
  n = 2
  ref = N_element
FEATURE [App::DocumentObjectGroupPython] O_element050  label="O_element : 025"  # scripted group (container) (typed FeaturePython)
  n = 5
  ref = O_element
FEATURE [App::DocumentObjectGroupPython] G4_KAPTON  # scripted group (container) (typed FeaturePython)
  Dunit = g/cm3
  Dvalue = 1.42
  Group = -> [C_element054,H_element048,N_element021,O_element050]
  conduct = 2
  density = 1
  expand = 3
  formula = G4_KAPTON
  name = G4_KAPTON
  specific = 4
FEATURE [App::DocumentObjectGroupPython] La_element001  label="La_element : 1"  # scripted group (container) (typed FeaturePython)
  n = 1
  ref = La_element
FEATURE [App::DocumentObjectGroupPython] Br_element003  label="Br_element : 002"  # scripted group (container) (typed FeaturePython)
  n = 1
  ref = Br_element
FEATURE [App::DocumentObjectGroupPython] O_element051  label="O_element : 026"  # scripted group (container) (typed FeaturePython)
  n = 1
  ref = O_element
FEATURE [App::DocumentObjectGroupPython] G4_LANTHANUM_OXYBROMIDE  # scripted group (container) (typed FeaturePython)
  Dunit = g/cm3
  Dvalue = 6.28
  Group = -> [La_element001,Br_element003,O_element051]
  conduct = 2
  density = 1
  expand = 3
  formula = G4_LANTHANUM_OXYBROMIDE
  name = G4_LANTHANUM_OXYBROMIDE
  specific = 4
FEATURE [App::DocumentObjectGroupPython] La_element002  label="La_element : 2"  # scripted group (container) (typed FeaturePython)
  n = 2
  ref = La_element
FEATURE [App::DocumentObjectGroupPython] O_element052  label="O_element : 027"  # scripted group (container) (typed FeaturePython)
  n = 2
  ref = O_element
FEATURE [App::DocumentObjectGroupPython] S_element015  label="S_element : 006"  # scripted group (container) (typed FeaturePython)
  n = 1
  ref = S_element
FEATURE [App::DocumentObjectGroupPython] G4_LANTHANUM_OXYSULFIDE  # scripted group (container) (typed FeaturePython)
  Dunit = g/cm3
  Dvalue = 5.86
  Group = -> [La_element002,O_element052,S_element015]
  conduct = 2
  density = 1
  expand = 3
  formula = G4_LANTHANUM_OXYSULFIDE
  name = G4_LANTHANUM_OXYSULFIDE
  specific = 4
FEATURE [App::DocumentObjectGroupPython] O_element053  label="O_element : 0.072"  # scripted group (container) (typed FeaturePython)
  n = 0.071682
FEATURE [App::DocumentObjectGroupPython] Pb_element002  label="Pb_element : 0.928"  # scripted group (container) (typed FeaturePython)
  n = 0.928318
FEATURE [App::DocumentObjectGroupPython] G4_LEAD_OXIDE  # scripted group (container) (typed FeaturePython)
  Dunit = g/cm3
  Dvalue = 9.53
  Group = -> [O_element053,Pb_element002]
  conduct = 2
  density = 1
  expand = 3
  formula = G4_LEAD_OXIDE
  name = G4_LEAD_OXIDE
  specific = 4
FEATURE [App::DocumentObjectGroupPython] Li_element001  label="Li_element : 1"  # scripted group (container) (typed FeaturePython)
  n = 1
  ref = Li_element
FEATURE [App::DocumentObjectGroupPython] N_element022  label="N_element : 011"  # scripted group (container) (typed FeaturePython)
  n = 1
  ref = N_element
FEATURE [App::DocumentObjectGroupPython] H_element049  label="H_element : 026"  # scripted group (container) (typed FeaturePython)
  n = 2
  ref = H_element
FEATURE [App::DocumentObjectGroupPython] G4_LITHIUM_AMIDE  # scripted group (container) (typed FeaturePython)
  Dunit = g/cm3
  Dvalue = 1.178
  Group = -> [Li_element001,N_element022,H_element049]
  conduct = 2
  density = 1
  expand = 3
  formula = G4_LITHIUM_AMIDE
  name = G4_LITHIUM_AMIDE
  specific = 4
FEATURE [App::DocumentObjectGroupPython] Li_element002  label="Li_element : 2"  # scripted group (container) (typed FeaturePython)
  n = 2
  ref = Li_element
FEATURE [App::DocumentObjectGroupPython] C_element055  label="C_element : 030"  # scripted group (container) (typed FeaturePython)
  n = 1
  ref = C_element
FEATURE [App::DocumentObjectGroupPython] O_element054  label="O_element : 028"  # scripted group (container) (typed FeaturePython)
  n = 3
  ref = O_element
FEATURE [App::DocumentObjectGroupPython] G4_LITHIUM_CARBONATE  # scripted group (container) (typed FeaturePython)
  Dunit = g/cm3
  Dvalue = 2.11
  Group = -> [Li_element002,C_element055,O_element054]
  conduct = 2
  density = 1
  expand = 3
  formula = G4_LITHIUM_CARBONATE
  name = G4_LITHIUM_CARBONATE
  specific = 4
FEATURE [App::DocumentObjectGroupPython] Li_element003  label="Li_element : 003"  # scripted group (container) (typed FeaturePython)
  n = 1
  ref = Li_element
FEATURE [App::DocumentObjectGroupPython] F_element012  label="F_element : 004"  # scripted group (container) (typed FeaturePython)
  n = 1
  ref = F_element
FEATURE [App::DocumentObjectGroupPython] G4_LITHIUM_FLUORIDE  # scripted group (container) (typed FeaturePython)
  Dunit = g/cm3
  Dvalue = 2.635
  Group = -> [Li_element003,F_element012]
  conduct = 2
  density = 1
  expand = 3
  formula = G4_LITHIUM_FLUORIDE
  name = G4_LITHIUM_FLUORIDE
  specific = 4
FEATURE [App::DocumentObjectGroupPython] Li_element004  label="Li_element : 004"  # scripted group (container) (typed FeaturePython)
  n = 1
  ref = Li_element
FEATURE [App::DocumentObjectGroupPython] H_element050  label="H_element : 027"  # scripted group (container) (typed FeaturePython)
  n = 1
  ref = H_element
FEATURE [App::DocumentObjectGroupPython] G4_LITHIUM_HYDRIDE  # scripted group (container) (typed FeaturePython)
  Dunit = g/cm3
  Dvalue = 0.82
  Group = -> [Li_element004,H_element050]
  conduct = 2
  density = 1
  expand = 3
  formula = G4_LITHIUM_HYDRIDE
  name = G4_LITHIUM_HYDRIDE
  specific = 4
FEATURE [App::DocumentObjectGroupPython] Li_element005  label="Li_element : 005"  # scripted group (container) (typed FeaturePython)
  n = 1
  ref = Li_element
FEATURE [App::DocumentObjectGroupPython] I_element003  label="I_element : 002"  # scripted group (container) (typed FeaturePython)
  n = 1
  ref = I_element
FEATURE [App::DocumentObjectGroupPython] G4_LITHIUM_IODIDE  # scripted group (container) (typed FeaturePython)
  Dunit = g/cm3
  Dvalue = 3.494
  Group = -> [Li_element005,I_element003]
  conduct = 2
  density = 1
  expand = 3
  formula = G4_LITHIUM_IODIDE
  name = G4_LITHIUM_IODIDE
  specific = 4
FEATURE [App::DocumentObjectGroupPython] Li_element006  label="Li_element : 006"  # scripted group (container) (typed FeaturePython)
  n = 2
  ref = Li_element
FEATURE [App::DocumentObjectGroupPython] O_element055  label="O_element : 029"  # scripted group (container) (typed FeaturePython)
  n = 1
  ref = O_element
FEATURE [App::DocumentObjectGroupPython] G4_LITHIUM_OXIDE  # scripted group (container) (typed FeaturePython)
  Dunit = g/cm3
  Dvalue = 2.013
  Group = -> [Li_element006,O_element055]
  conduct = 2
  density = 1
  expand = 3
  formula = G4_LITHIUM_OXIDE
  name = G4_LITHIUM_OXIDE
  specific = 4
FEATURE [App::DocumentObjectGroupPython] Li_element007  label="Li_element : 007"  # scripted group (container) (typed FeaturePython)
  n = 2
  ref = Li_element
FEATURE [App::DocumentObjectGroupPython] B_element005  label="B_element : 005"  # scripted group (container) (typed FeaturePython)
  n = 4
  ref = B_element
FEATURE [App::DocumentObjectGroupPython] O_element056  label="O_element : 7"  # scripted group (container) (typed FeaturePython)
  n = 7
  ref = O_element
FEATURE [App::DocumentObjectGroupPython] G4_LITHIUM_TETRABORATE  # scripted group (container) (typed FeaturePython)
  Dunit = g/cm3
  Dvalue = 2.44
  Group = -> [Li_element007,B_element005,O_element056]
  conduct = 2
  density = 1
  expand = 3
  formula = G4_LITHIUM_TETRABORATE
  name = G4_LITHIUM_TETRABORATE
  specific = 4
FEATURE [App::DocumentObjectGroupPython] H_element051  label="H_element : 0.105"  # scripted group (container) (typed FeaturePython)
  n = 0.105
FEATURE [App::DocumentObjectGroupPython] C_element056  label="C_element : 0.083"  # scripted group (container) (typed FeaturePython)
  n = 0.083
FEATURE [App::DocumentObjectGroupPython] N_element023  label="N_element : 0.023"  # scripted group (container) (typed FeaturePython)
  n = 0.023
FEATURE [App::DocumentObjectGroupPython] O_element057  label="O_element : 0.779"  # scripted group (container) (typed FeaturePython)
  n = 0.779
FEATURE [App::DocumentObjectGroupPython] Na_element010  label="Na_element : 0.097"  # scripted group (container) (typed FeaturePython)
  n = 0.002
FEATURE [App::DocumentObjectGroupPython] P_element006  label="P_element : 0.105"  # scripted group (container) (typed FeaturePython)
  n = 0.001
FEATURE [App::DocumentObjectGroupPython] S_element016  label="S_element : 0.017"  # scripted group (container) (typed FeaturePython)
  n = 0.002
FEATURE [App::DocumentObjectGroupPython] Cl_element014  label="Cl_element : 0.587"  # scripted group (container) (typed FeaturePython)
  n = 0.003
FEATURE [App::DocumentObjectGroupPython] K_element005  label="K_element : 0.015"  # scripted group (container) (typed FeaturePython)
  n = 0.002
FEATURE [App::DocumentObjectGroupPython] G4_LUNG_ICRP  # scripted group (container) (typed FeaturePython)
  Dunit = g/cm3
  Dvalue = 1.04
  Group = -> [H_element051,C_element056,N_element023,O_element057,Na_element010,P_element006,S_element016,Cl_element014,K_element005]
  conduct = 2
  density = 1
  expand = 3
  formula = G4_LUNG_ICRP
  name = G4_LUNG_ICRP
  specific = 4
FEATURE [App::DocumentObjectGroupPython] H_element052  label="H_element : 0.116"  # scripted group (container) (typed FeaturePython)
  n = 0.114318
FEATURE [App::DocumentObjectGroupPython] C_element057  label="C_element : 0.656"  # scripted group (container) (typed FeaturePython)
  n = 0.655824
FEATURE [App::DocumentObjectGroupPython] O_element058  label="O_element : 0.092"  # scripted group (container) (typed FeaturePython)
  n = 0.0921831
FEATURE [App::DocumentObjectGroupPython] Mg_element004  label="Mg_element : 0.135"  # scripted group (container) (typed FeaturePython)
  n = 0.134792
FEATURE [App::DocumentObjectGroupPython] Ca_element013  label="Ca_element : 0.003"  # scripted group (container) (typed FeaturePython)
  n = 0.002883
FEATURE [App::DocumentObjectGroupPython] G4_M3_WAX  # scripted group (container) (typed FeaturePython)
  Dunit = g/cm3
  Dvalue = 1.05
  Group = -> [H_element052,C_element057,O_element058,Mg_element004,Ca_element013]
  conduct = 2
  density = 1
  expand = 3
  formula = G4_M3_WAX
  name = G4_M3_WAX
  specific = 4
FEATURE [App::DocumentObjectGroupPython] Mg_element005  label="Mg_element : 1"  # scripted group (container) (typed FeaturePython)
  n = 1
  ref = Mg_element
FEATURE [App::DocumentObjectGroupPython] C_element058  label="C_element : 031"  # scripted group (container) (typed FeaturePython)
  n = 1
  ref = C_element
FEATURE [App::DocumentObjectGroupPython] O_element059  label="O_element : 030"  # scripted group (container) (typed FeaturePython)
  n = 3
  ref = O_element
FEATURE [App::DocumentObjectGroupPython] G4_MAGNESIUM_CARBONATE  # scripted group (container) (typed FeaturePython)
  Dunit = g/cm3
  Dvalue = 2.958
  Group = -> [Mg_element005,C_element058,O_element059]
  conduct = 2
  density = 1
  expand = 3
  formula = G4_MAGNESIUM_CARBONATE
  name = G4_MAGNESIUM_CARBONATE
  specific = 4
FEATURE [App::DocumentObjectGroupPython] Mg_element006  label="Mg_element : 002"  # scripted group (container) (typed FeaturePython)
  n = 1
  ref = Mg_element
FEATURE [App::DocumentObjectGroupPython] F_element013  label="F_element : 005"  # scripted group (container) (typed FeaturePython)
  n = 2
  ref = F_element
FEATURE [App::DocumentObjectGroupPython] G4_MAGNESIUM_FLUORIDE  # scripted group (container) (typed FeaturePython)
  Dunit = g/cm3
  Dvalue = 3
  Group = -> [Mg_element006,F_element013]
  conduct = 2
  density = 1
  expand = 3
  formula = G4_MAGNESIUM_FLUORIDE
  name = G4_MAGNESIUM_FLUORIDE
  specific = 4
FEATURE [App::DocumentObjectGroupPython] Mg_element007  label="Mg_element : 003"  # scripted group (container) (typed FeaturePython)
  n = 1
  ref = Mg_element
FEATURE [App::DocumentObjectGroupPython] O_element060  label="O_element : 031"  # scripted group (container) (typed FeaturePython)
  n = 1
  ref = O_element
FEATURE [App::DocumentObjectGroupPython] G4_MAGNESIUM_OXIDE  # scripted group (container) (typed FeaturePython)
  Dunit = g/cm3
  Dvalue = 3.58
  Group = -> [Mg_element007,O_element060]
  conduct = 2
  density = 1
  expand = 3
  formula = G4_MAGNESIUM_OXIDE
  name = G4_MAGNESIUM_OXIDE
  specific = 4
FEATURE [App::DocumentObjectGroupPython] Mg_element008  label="Mg_element : 004"  # scripted group (container) (typed FeaturePython)
  n = 1
  ref = Mg_element
FEATURE [App::DocumentObjectGroupPython] B_element006  label="B_element : 006"  # scripted group (container) (typed FeaturePython)
  n = 4
  ref = B_element
FEATURE [App::DocumentObjectGroupPython] O_element061  label="O_element : 032"  # scripted group (container) (typed FeaturePython)
  n = 7
  ref = O_element
FEATURE [App::DocumentObjectGroupPython] G4_MAGNESIUM_TETRABORATE  # scripted group (container) (typed FeaturePython)
  Dunit = g/cm3
  Dvalue = 2.53
  Group = -> [Mg_element008,B_element006,O_element061]
  conduct = 2
  density = 1
  expand = 3
  formula = G4_MAGNESIUM_TETRABORATE
  name = G4_MAGNESIUM_TETRABORATE
  specific = 4
FEATURE [App::DocumentObjectGroupPython] Hg_element001  label="Hg_element : 1"  # scripted group (container) (typed FeaturePython)
  n = 1
  ref = Hg_element
FEATURE [App::DocumentObjectGroupPython] I_element004  label="I_element : 2"  # scripted group (container) (typed FeaturePython)
  n = 2
  ref = I_element
FEATURE [App::DocumentObjectGroupPython] G4_MERCURIC_IODIDE  # scripted group (container) (typed FeaturePython)
  Dunit = g/cm3
  Dvalue = 6.36
  Group = -> [Hg_element001,I_element004]
  conduct = 2
  density = 1
  expand = 3
  formula = G4_MERCURIC_IODIDE
  name = G4_MERCURIC_IODIDE
  specific = 4
FEATURE [App::DocumentObjectGroupPython] C_element059  label="C_element : 032"  # scripted group (container) (typed FeaturePython)
  n = 1
  ref = C_element
FEATURE [App::DocumentObjectGroupPython] H_element053  label="H_element : 028"  # scripted group (container) (typed FeaturePython)
  n = 4
  ref = H_element
FEATURE [App::DocumentObjectGroupPython] G4_METHANE  # scripted group (container) (typed FeaturePython)
  Dunit = g/cm3
  Dvalue = 0.000667151
  Group = -> [C_element059,H_element053]
  conduct = 2
  density = 1
  expand = 3
  formula = G4_METHANE
  name = G4_METHANE
  specific = 4
FEATURE [App::DocumentObjectGroupPython] C_element060  label="C_element : 033"  # scripted group (container) (typed FeaturePython)
  n = 1
  ref = C_element
FEATURE [App::DocumentObjectGroupPython] H_element054  label="H_element : 029"  # scripted group (container) (typed FeaturePython)
  n = 4
  ref = H_element
FEATURE [App::DocumentObjectGroupPython] O_element062  label="O_element : 033"  # scripted group (container) (typed FeaturePython)
  n = 1
  ref = O_element
FEATURE [App::DocumentObjectGroupPython] G4_METHANOL  # scripted group (container) (typed FeaturePython)
  Dunit = g/cm3
  Dvalue = 0.7914
  Group = -> [C_element060,H_element054,O_element062]
  conduct = 2
  density = 1
  expand = 3
  formula = G4_METHANOL
  name = G4_METHANOL
  specific = 4
FEATURE [App::DocumentObjectGroupPython] H_element055  label="H_element : 0.134"  # scripted group (container) (typed FeaturePython)
  n = 0.13404
FEATURE [App::DocumentObjectGroupPython] C_element061  label="C_element : 0.778"  # scripted group (container) (typed FeaturePython)
  n = 0.77796
FEATURE [App::DocumentObjectGroupPython] O_element063  label="O_element : 0.035"  # scripted group (container) (typed FeaturePython)
  n = 0.03502
FEATURE [App::DocumentObjectGroupPython] Mg_element009  label="Mg_element : 0.039"  # scripted group (container) (typed FeaturePython)
  n = 0.038594
FEATURE [App::DocumentObjectGroupPython] Ti_element002  label="Ti_element : 0.014"  # scripted group (container) (typed FeaturePython)
  n = 0.014386
FEATURE [App::DocumentObjectGroupPython] G4_MIX_D_WAX  # scripted group (container) (typed FeaturePython)
  Dunit = g/cm3
  Dvalue = 0.99
  Group = -> [H_element055,C_element061,O_element063,Mg_element009,Ti_element002]
  conduct = 2
  density = 1
  expand = 3
  formula = G4_MIX_D_WAX
  name = G4_MIX_D_WAX
  specific = 4
FEATURE [App::DocumentObjectGroupPython] H_element056  label="H_element : 0.135"  # scripted group (container) (typed FeaturePython)
  n = 0.081192
FEATURE [App::DocumentObjectGroupPython] C_element062  label="C_element : 0.583"  # scripted group (container) (typed FeaturePython)
  n = 0.583442
FEATURE [App::DocumentObjectGroupPython] N_element024  label="N_element : 0.018"  # scripted group (container) (typed FeaturePython)
  n = 0.017798
FEATURE [App::DocumentObjectGroupPython] O_element064  label="O_element : 0.186"  # scripted group (container) (typed FeaturePython)
  n = 0.186381
FEATURE [App::DocumentObjectGroupPython] Mg_element010  label="Mg_element : 0.130"  # scripted group (container) (typed FeaturePython)
  n = 0.130287
FEATURE [App::DocumentObjectGroupPython] Cl_element015  label="Cl_element : 0.588"  # scripted group (container) (typed FeaturePython)
  n = 0.0009
FEATURE [App::DocumentObjectGroupPython] G4_MS20_TISSUE  # scripted group (container) (typed FeaturePython)
  Dunit = g/cm3
  Dvalue = 1
  Group = -> [H_element056,C_element062,N_element024,O_element064,Mg_element010,Cl_element015]
  conduct = 2
  density = 1
  expand = 3
  formula = G4_MS20_TISSUE
  name = G4_MS20_TISSUE
  specific = 4
FEATURE [App::DocumentObjectGroupPython] H_element057  label="H_element : 0.136"  # scripted group (container) (typed FeaturePython)
  n = 0.102
FEATURE [App::DocumentObjectGroupPython] C_element063  label="C_element : 0.143"  # scripted group (container) (typed FeaturePython)
  n = 0.143
FEATURE [App::DocumentObjectGroupPython] N_element025  label="N_element : 0.034"  # scripted group (container) (typed FeaturePython)
  n = 0.034
FEATURE [App::DocumentObjectGroupPython] O_element065  label="O_element : 0.710"  # scripted group (container) (typed FeaturePython)
  n = 0.71
FEATURE [App::DocumentObjectGroupPython] Na_element011  label="Na_element : 0.098"  # scripted group (container) (typed FeaturePython)
  n = 0.001
FEATURE [App::DocumentObjectGroupPython] P_element007  label="P_element : 0.002"  # scripted group (container) (typed FeaturePython)
  n = 0.002
FEATURE [App::DocumentObjectGroupPython] S_element017  label="S_element : 0.018"  # scripted group (container) (typed FeaturePython)
  n = 0.003
FEATURE [App::DocumentObjectGroupPython] Cl_element016  label="Cl_element : 0.589"  # scripted group (container) (typed FeaturePython)
  n = 0.001
FEATURE [App::DocumentObjectGroupPython] K_element006  label="K_element : 0.004"  # scripted group (container) (typed FeaturePython)
  n = 0.004
FEATURE [App::DocumentObjectGroupPython] G4_MUSCLE_SKELETAL_ICRP  # scripted group (container) (typed FeaturePython)
  Dunit = g/cm3
  Dvalue = 1.05
  Group = -> [H_element057,C_element063,N_element025,O_element065,Na_element011,P_element007,S_element017,Cl_element016,K_element006]
  conduct = 2
  density = 1
  expand = 3
  formula = G4_MUSCLE_SKELETAL_ICRP
  name = G4_MUSCLE_SKELETAL_ICRP
  specific = 4
FEATURE [App::DocumentObjectGroupPython] H_element058  label="H_element : 0.137"  # scripted group (container) (typed FeaturePython)
  n = 0.102102
FEATURE [App::DocumentObjectGroupPython] C_element064  label="C_element : 0.123"  # scripted group (container) (typed FeaturePython)
  n = 0.123123
FEATURE [App::DocumentObjectGroupPython] N_element026  label="N_element : 0.756"  # scripted group (container) (typed FeaturePython)
  n = 0.035035
FEATURE [App::DocumentObjectGroupPython] O_element066  label="O_element : 0.730"  # scripted group (container) (typed FeaturePython)
  n = 0.72973
FEATURE [App::DocumentObjectGroupPython] Na_element012  label="Na_element : 0.099"  # scripted group (container) (typed FeaturePython)
  n = 0.001001
FEATURE [App::DocumentObjectGroupPython] P_element008  label="P_element : 0.106"  # scripted group (container) (typed FeaturePython)
  n = 0.002002
FEATURE [App::DocumentObjectGroupPython] S_element018  label="S_element : 0.019"  # scripted group (container) (typed FeaturePython)
  n = 0.004004
FEATURE [App::DocumentObjectGroupPython] K_element007  label="K_element : 0.016"  # scripted group (container) (typed FeaturePython)
  n = 0.003003
FEATURE [App::DocumentObjectGroupPython] G4_MUSCLE_STRIATED_ICRU  # scripted group (container) (typed FeaturePython)
  Dunit = g/cm3
  Dvalue = 1.04
  Group = -> [H_element058,C_element064,N_element026,O_element066,Na_element012,P_element008,S_element018,K_element007]
  conduct = 2
  density = 1
  expand = 3
  formula = G4_MUSCLE_STRIATED_ICRU
  name = G4_MUSCLE_STRIATED_ICRU
  specific = 4
FEATURE [App::DocumentObjectGroupPython] H_element059  label="H_element : 0.098"  # scripted group (container) (typed FeaturePython)
  n = 0.0982341
FEATURE [App::DocumentObjectGroupPython] C_element065  label="C_element : 0.156"  # scripted group (container) (typed FeaturePython)
  n = 0.156214
FEATURE [App::DocumentObjectGroupPython] N_element027  label="N_element : 0.757"  # scripted group (container) (typed FeaturePython)
  n = 0.035451
FEATURE [App::DocumentObjectGroupPython] O_element067  label="O_element : 0.880"  # scripted group (container) (typed FeaturePython)
  n = 0.710101
FEATURE [App::DocumentObjectGroupPython] G4_MUSCLE_WITH_SUCROSE  # scripted group (container) (typed FeaturePython)
  Dunit = g/cm3
  Dvalue = 1.11
  Group = -> [H_element059,C_element065,N_element027,O_element067]
  conduct = 2
  density = 1
  expand = 3
  formula = G4_MUSCLE_WITH_SUCROSE
  name = G4_MUSCLE_WITH_SUCROSE
  specific = 4
FEATURE [App::DocumentObjectGroupPython] H_element060  label="H_element : 0.138"  # scripted group (container) (typed FeaturePython)
  n = 0.101969
FEATURE [App::DocumentObjectGroupPython] C_element066  label="C_element : 0.120"  # scripted group (container) (typed FeaturePython)
  n = 0.120058
FEATURE [App::DocumentObjectGroupPython] N_element028  label="N_element : 0.758"  # scripted group (container) (typed FeaturePython)
  n = 0.035451
FEATURE [App::DocumentObjectGroupPython] O_element068  label="O_element : 0.743"  # scripted group (container) (typed FeaturePython)
  n = 0.742522
FEATURE [App::DocumentObjectGroupPython] G4_MUSCLE_WITHOUT_SUCROSE  # scripted group (container) (typed FeaturePython)
  Dunit = g/cm3
  Dvalue = 1.07
  Group = -> [H_element060,C_element066,N_element028,O_element068]
  conduct = 2
  density = 1
  expand = 3
  formula = G4_MUSCLE_WITHOUT_SUCROSE
  name = G4_MUSCLE_WITHOUT_SUCROSE
  specific = 4
FEATURE [App::DocumentObjectGroupPython] C_element067  label="C_element : 10"  # scripted group (container) (typed FeaturePython)
  n = 10
  ref = C_element
FEATURE [App::DocumentObjectGroupPython] H_element061  label="H_element : 030"  # scripted group (container) (typed FeaturePython)
  n = 8
  ref = H_element
FEATURE [App::DocumentObjectGroupPython] G4_NAPHTHALENE  # scripted group (container) (typed FeaturePython)
  Dunit = g/cm3
  Dvalue = 1.145
  Group = -> [C_element067,H_element061]
  conduct = 2
  density = 1
  expand = 3
  formula = G4_NAPHTHALENE
  name = G4_NAPHTHALENE
  specific = 4
FEATURE [App::DocumentObjectGroupPython] C_element068  label="C_element : 034"  # scripted group (container) (typed FeaturePython)
  n = 6
  ref = C_element
FEATURE [App::DocumentObjectGroupPython] H_element062  label="H_element : 031"  # scripted group (container) (typed FeaturePython)
  n = 5
  ref = H_element
FEATURE [App::DocumentObjectGroupPython] N_element029  label="N_element : 012"  # scripted group (container) (typed FeaturePython)
  n = 1
  ref = N_element
FEATURE [App::DocumentObjectGroupPython] O_element069  label="O_element : 034"  # scripted group (container) (typed FeaturePython)
  n = 2
  ref = O_element
FEATURE [App::DocumentObjectGroupPython] G4_NITROBENZENE  # scripted group (container) (typed FeaturePython)
  Dunit = g/cm3
  Dvalue = 1.19867
  Group = -> [C_element068,H_element062,N_element029,O_element069]
  conduct = 2
  density = 1
  expand = 3
  formula = G4_NITROBENZENE
  name = G4_NITROBENZENE
  specific = 4
FEATURE [App::DocumentObjectGroupPython] N_element030  label="N_element : 013"  # scripted group (container) (typed FeaturePython)
  n = 2
  ref = N_element
FEATURE [App::DocumentObjectGroupPython] O_element070  label="O_element : 035"  # scripted group (container) (typed FeaturePython)
  n = 1
  ref = O_element
FEATURE [App::DocumentObjectGroupPython] G4_NITROUS_OXIDE  # scripted group (container) (typed FeaturePython)
  Dunit = g/cm3
  Dvalue = 0.00183094
  Group = -> [N_element030,O_element070]
  conduct = 2
  density = 1
  expand = 3
  formula = G4_NITROUS_OXIDE
  name = G4_NITROUS_OXIDE
  specific = 4
FEATURE [App::DocumentObjectGroupPython] H_element063  label="H_element : 0.104"  # scripted group (container) (typed FeaturePython)
  n = 0.103509
FEATURE [App::DocumentObjectGroupPython] C_element069  label="C_element : 0.648"  # scripted group (container) (typed FeaturePython)
  n = 0.648416
FEATURE [App::DocumentObjectGroupPython] N_element031  label="N_element : 0.100"  # scripted group (container) (typed FeaturePython)
  n = 0.0995361
FEATURE [App::DocumentObjectGroupPython] O_element071  label="O_element : 0.149"  # scripted group (container) (typed FeaturePython)
  n = 0.148539
FEATURE [App::DocumentObjectGroupPython] G4_NYLON_8062  label="G4_NYLON-8062"  # scripted group (container) (typed FeaturePython)
  Dunit = g/cm3
  Dvalue = 1.08
  Group = -> [H_element063,C_element069,N_element031,O_element071]
  conduct = 2
  density = 1
  expand = 3
  formula = G4_NYLON-8062
  name = G4_NYLON-8062
  specific = 4
FEATURE [App::DocumentObjectGroupPython] C_element070  label="C_element : 035"  # scripted group (container) (typed FeaturePython)
  n = 6
  ref = C_element
FEATURE [App::DocumentObjectGroupPython] H_element064  label="H_element : 11"  # scripted group (container) (typed FeaturePython)
  n = 11
  ref = H_element
FEATURE [App::DocumentObjectGroupPython] N_element032  label="N_element : 014"  # scripted group (container) (typed FeaturePython)
  n = 1
  ref = N_element
FEATURE [App::DocumentObjectGroupPython] O_element072  label="O_element : 036"  # scripted group (container) (typed FeaturePython)
  n = 1
  ref = O_element
FEATURE [App::DocumentObjectGroupPython] G4_NYLON_6_6  label="G4_NYLON-6-6"  # scripted group (container) (typed FeaturePython)
  Dunit = g/cm3
  Dvalue = 1.14
  Group = -> [C_element070,H_element064,N_element032,O_element072]
  conduct = 2
  density = 1
  expand = 3
  formula = G4_NYLON-6-6
  name = G4_NYLON-6-6
  specific = 4
FEATURE [App::DocumentObjectGroupPython] H_element065  label="H_element : 0.139"  # scripted group (container) (typed FeaturePython)
  n = 0.107062
FEATURE [App::DocumentObjectGroupPython] C_element071  label="C_element : 0.680"  # scripted group (container) (typed FeaturePython)
  n = 0.680449
FEATURE [App::DocumentObjectGroupPython] N_element033  label="N_element : 0.099"  # scripted group (container) (typed FeaturePython)
  n = 0.099189
FEATURE [App::DocumentObjectGroupPython] O_element073  label="O_element : 0.113"  # scripted group (container) (typed FeaturePython)
  n = 0.1133
FEATURE [App::DocumentObjectGroupPython] G4_NYLON_6_10  label="G4_NYLON-6-10"  # scripted group (container) (typed FeaturePython)
  Dunit = g/cm3
  Dvalue = 1.14
  Group = -> [H_element065,C_element071,N_element033,O_element073]
  conduct = 2
  density = 1
  expand = 3
  formula = G4_NYLON-6-10
  name = G4_NYLON-6-10
  specific = 4
FEATURE [App::DocumentObjectGroupPython] H_element066  label="H_element : 0.140"  # scripted group (container) (typed FeaturePython)
  n = 0.115476
FEATURE [App::DocumentObjectGroupPython] C_element072  label="C_element : 0.721"  # scripted group (container) (typed FeaturePython)
  n = 0.720818
FEATURE [App::DocumentObjectGroupPython] N_element034  label="N_element : 0.076"  # scripted group (container) (typed FeaturePython)
  n = 0.0764169
FEATURE [App::DocumentObjectGroupPython] O_element074  label="O_element : 0.087"  # scripted group (container) (typed FeaturePython)
  n = 0.0872889
FEATURE [App::DocumentObjectGroupPython] G4_NYLON_11_RILSAN  label="G4_NYLON-11_RILSAN"  # scripted group (container) (typed FeaturePython)
  Dunit = g/cm3
  Dvalue = 1.425
  Group = -> [H_element066,C_element072,N_element034,O_element074]
  conduct = 2
  density = 1
  expand = 3
  formula = G4_NYLON-11_RILSAN
  name = G4_NYLON-11_RILSAN
  specific = 4
FEATURE [App::DocumentObjectGroupPython] C_element073  label="C_element : 8"  # scripted group (container) (typed FeaturePython)
  n = 8
  ref = C_element
FEATURE [App::DocumentObjectGroupPython] H_element067  label="H_element : 18"  # scripted group (container) (typed FeaturePython)
  n = 18
  ref = H_element
FEATURE [App::DocumentObjectGroupPython] G4_OCTANE  # scripted group (container) (typed FeaturePython)
  Dunit = g/cm3
  Dvalue = 0.7026
  Group = -> [C_element073,H_element067]
  conduct = 2
  density = 1
  expand = 3
  formula = G4_OCTANE
  name = G4_OCTANE
  specific = 4
FEATURE [App::DocumentObjectGroupPython] C_element074  label="C_element : 25"  # scripted group (container) (typed FeaturePython)
  n = 25
  ref = C_element
FEATURE [App::DocumentObjectGroupPython] H_element068  label="H_element : 52"  # scripted group (container) (typed FeaturePython)
  n = 52
  ref = H_element
FEATURE [App::DocumentObjectGroupPython] G4_PARAFFIN  # scripted group (container) (typed FeaturePython)
  Dunit = g/cm3
  Dvalue = 0.93
  Group = -> [C_element074,H_element068]
  conduct = 2
  density = 1
  expand = 3
  formula = G4_PARAFFIN
  name = G4_PARAFFIN
  specific = 4
FEATURE [App::DocumentObjectGroupPython] C_element075  label="C_element : 036"  # scripted group (container) (typed FeaturePython)
  n = 5
  ref = C_element
FEATURE [App::DocumentObjectGroupPython] H_element069  label="H_element : 032"  # scripted group (container) (typed FeaturePython)
  n = 12
  ref = H_element
FEATURE [App::DocumentObjectGroupPython] G4_N_PENTANE  label="G4_N-PENTANE"  # scripted group (container) (typed FeaturePython)
  Dunit = g/cm3
  Dvalue = 0.6262
  Group = -> [C_element075,H_element069]
  conduct = 2
  density = 1
  expand = 3
  formula = G4_N-PENTANE
  name = G4_N-PENTANE
  specific = 4
FEATURE [App::DocumentObjectGroupPython] H_element070  label="H_element : 0.014"  # scripted group (container) (typed FeaturePython)
  n = 0.0141
FEATURE [App::DocumentObjectGroupPython] C_element076  label="C_element : 0.072"  # scripted group (container) (typed FeaturePython)
  n = 0.072261
FEATURE [App::DocumentObjectGroupPython] N_element035  label="N_element : 0.019"  # scripted group (container) (typed FeaturePython)
  n = 0.01932
FEATURE [App::DocumentObjectGroupPython] O_element075  label="O_element : 0.066"  # scripted group (container) (typed FeaturePython)
  n = 0.066101
FEATURE [App::DocumentObjectGroupPython] S_element019  label="S_element : 0.020"  # scripted group (container) (typed FeaturePython)
  n = 0.00189
FEATURE [App::DocumentObjectGroupPython] Br_element004  label="Br_element : 0.349"  # scripted group (container) (typed FeaturePython)
  n = 0.349103
FEATURE [App::DocumentObjectGroupPython] Ag_element001  label="Ag_element : 0.474"  # scripted group (container) (typed FeaturePython)
  n = 0.474105
FEATURE [App::DocumentObjectGroupPython] I_element005  label="I_element : 0.003"  # scripted group (container) (typed FeaturePython)
  n = 0.00312
FEATURE [App::DocumentObjectGroupPython] G4_PHOTO_EMULSION  # scripted group (container) (typed FeaturePython)
  Dunit = g/cm3
  Dvalue = 3.815
  Group = -> [H_element070,C_element076,N_element035,O_element075,S_element019,Br_element004,Ag_element001,I_element005]
  conduct = 2
  density = 1
  expand = 3
  formula = G4_PHOTO_EMULSION
  name = G4_PHOTO_EMULSION
  specific = 4
FEATURE [App::DocumentObjectGroupPython] C_element077  label="C_element : 9"  # scripted group (container) (typed FeaturePython)
  n = 9
  ref = C_element
FEATURE [App::DocumentObjectGroupPython] H_element071  label="H_element : 033"  # scripted group (container) (typed FeaturePython)
  n = 10
  ref = H_element
FEATURE [App::DocumentObjectGroupPython] G4_PLASTIC_SC_VINYLTOLUENE  # scripted group (container) (typed FeaturePython)
  Dunit = g/cm3
  Dvalue = 1.032
  Group = -> [C_element077,H_element071]
  conduct = 2
  density = 1
  expand = 3
  formula = G4_PLASTIC_SC_VINYLTOLUENE
  name = G4_PLASTIC_SC_VINYLTOLUENE
  specific = 4
FEATURE [App::DocumentObjectGroupPython] Pu_element001  label="Pu_element : 1"  # scripted group (container) (typed FeaturePython)
  n = 1
  ref = Pu_element
FEATURE [App::DocumentObjectGroupPython] O_element076  label="O_element : 037"  # scripted group (container) (typed FeaturePython)
  n = 2
  ref = O_element
FEATURE [App::DocumentObjectGroupPython] G4_PLUTONIUM_DIOXIDE  # scripted group (container) (typed FeaturePython)
  Dunit = g/cm3
  Dvalue = 11.46
  Group = -> [Pu_element001,O_element076]
  conduct = 2
  density = 1
  expand = 3
  formula = G4_PLUTONIUM_DIOXIDE
  name = G4_PLUTONIUM_DIOXIDE
  specific = 4
FEATURE [App::DocumentObjectGroupPython] C_element078  label="C_element : 037"  # scripted group (container) (typed FeaturePython)
  n = 3
  ref = C_element
FEATURE [App::DocumentObjectGroupPython] H_element072  label="H_element : 034"  # scripted group (container) (typed FeaturePython)
  n = 3
  ref = H_element
FEATURE [App::DocumentObjectGroupPython] N_element036  label="N_element : 015"  # scripted group (container) (typed FeaturePython)
  n = 1
  ref = N_element
FEATURE [App::DocumentObjectGroupPython] G4_POLYACRYLONITRILE  # scripted group (container) (typed FeaturePython)
  Dunit = g/cm3
  Dvalue = 1.17
  Group = -> [C_element078,H_element072,N_element036]
  conduct = 2
  density = 1
  expand = 3
  formula = G4_POLYACRYLONITRILE
  name = G4_POLYACRYLONITRILE
  specific = 4
FEATURE [App::DocumentObjectGroupPython] C_element079  label="C_element : 16"  # scripted group (container) (typed FeaturePython)
  n = 16
  ref = C_element
FEATURE [App::DocumentObjectGroupPython] H_element073  label="H_element : 035"  # scripted group (container) (typed FeaturePython)
  n = 14
  ref = H_element
FEATURE [App::DocumentObjectGroupPython] O_element077  label="O_element : 038"  # scripted group (container) (typed FeaturePython)
  n = 3
  ref = O_element
FEATURE [App::DocumentObjectGroupPython] G4_POLYCARBONATE  # scripted group (container) (typed FeaturePython)
  Dunit = g/cm3
  Dvalue = 1.2
  Group = -> [C_element079,H_element073,O_element077]
  conduct = 2
  density = 1
  expand = 3
  formula = G4_POLYCARBONATE
  name = G4_POLYCARBONATE
  specific = 4
FEATURE [App::DocumentObjectGroupPython] C_element080  label="C_element : 038"  # scripted group (container) (typed FeaturePython)
  n = 8
  ref = C_element
FEATURE [App::DocumentObjectGroupPython] H_element074  label="H_element : 036"  # scripted group (container) (typed FeaturePython)
  n = 7
  ref = H_element
FEATURE [App::DocumentObjectGroupPython] Cl_element017  label="Cl_element : 007"  # scripted group (container) (typed FeaturePython)
  n = 1
  ref = Cl_element
FEATURE [App::DocumentObjectGroupPython] G4_POLYCHLOROSTYRENE  # scripted group (container) (typed FeaturePython)
  Dunit = g/cm3
  Dvalue = 1.3
  Group = -> [C_element080,H_element074,Cl_element017]
  conduct = 2
  density = 1
  expand = 3
  formula = G4_POLYCHLOROSTYRENE
  name = G4_POLYCHLOROSTYRENE
  specific = 4
FEATURE [App::DocumentObjectGroupPython] C_element081  label="C_element : 039"  # scripted group (container) (typed FeaturePython)
  n = 1
  ref = C_element
FEATURE [App::DocumentObjectGroupPython] H_element075  label="H_element : 037"  # scripted group (container) (typed FeaturePython)
  n = 2
  ref = H_element
FEATURE [App::DocumentObjectGroupPython] G4_POLYETHYLENE  # scripted group (container) (typed FeaturePython)
  Dunit = g/cm3
  Dvalue = 0.94
  Group = -> [C_element081,H_element075]
  conduct = 2
  density = 1
  expand = 3
  formula = G4_POLYETHYLENE
  name = G4_POLYETHYLENE
  specific = 4
FEATURE [App::DocumentObjectGroupPython] C_element082  label="C_element : 040"  # scripted group (container) (typed FeaturePython)
  n = 10
  ref = C_element
FEATURE [App::DocumentObjectGroupPython] H_element076  label="H_element : 038"  # scripted group (container) (typed FeaturePython)
  n = 8
  ref = H_element
FEATURE [App::DocumentObjectGroupPython] O_element078  label="O_element : 039"  # scripted group (container) (typed FeaturePython)
  n = 4
  ref = O_element
FEATURE [App::DocumentObjectGroupPython] G4_MYLAR  # scripted group (container) (typed FeaturePython)
  Dunit = g/cm3
  Dvalue = 1.4
  Group = -> [C_element082,H_element076,O_element078]
  conduct = 2
  density = 1
  expand = 3
  formula = G4_MYLAR
  name = G4_MYLAR
  specific = 4
FEATURE [App::DocumentObjectGroupPython] C_element083  label="C_element : 041"  # scripted group (container) (typed FeaturePython)
  n = 5
  ref = C_element
FEATURE [App::DocumentObjectGroupPython] H_element077  label="H_element : 039"  # scripted group (container) (typed FeaturePython)
  n = 8
  ref = H_element
FEATURE [App::DocumentObjectGroupPython] O_element079  label="O_element : 040"  # scripted group (container) (typed FeaturePython)
  n = 2
  ref = O_element
FEATURE [App::DocumentObjectGroupPython] G4_PLEXIGLASS  # scripted group (container) (typed FeaturePython)
  Dunit = g/cm3
  Dvalue = 1.19
  Group = -> [C_element083,H_element077,O_element079]
  conduct = 2
  density = 1
  expand = 3
  formula = G4_PLEXIGLASS
  name = G4_PLEXIGLASS
  specific = 4
FEATURE [App::DocumentObjectGroupPython] C_element084  label="C_element : 042"  # scripted group (container) (typed FeaturePython)
  n = 1
  ref = C_element
FEATURE [App::DocumentObjectGroupPython] H_element078  label="H_element : 040"  # scripted group (container) (typed FeaturePython)
  n = 2
  ref = H_element
FEATURE [App::DocumentObjectGroupPython] O_element080  label="O_element : 041"  # scripted group (container) (typed FeaturePython)
  n = 1
  ref = O_element
FEATURE [App::DocumentObjectGroupPython] G4_POLYOXYMETHYLENE  # scripted group (container) (typed FeaturePython)
  Dunit = g/cm3
  Dvalue = 1.425
  Group = -> [C_element084,H_element078,O_element080]
  conduct = 2
  density = 1
  expand = 3
  formula = G4_POLYOXYMETHYLENE
  name = G4_POLYOXYMETHYLENE
  specific = 4
FEATURE [App::DocumentObjectGroupPython] C_element085  label="C_element : 043"  # scripted group (container) (typed FeaturePython)
  n = 2
  ref = C_element
FEATURE [App::DocumentObjectGroupPython] H_element079  label="H_element : 041"  # scripted group (container) (typed FeaturePython)
  n = 4
  ref = H_element
FEATURE [App::DocumentObjectGroupPython] G4_POLYPROPYLENE  # scripted group (container) (typed FeaturePython)
  Dunit = g/cm3
  Dvalue = 0.9
  Group = -> [C_element085,H_element079]
  conduct = 2
  density = 1
  expand = 3
  formula = G4_POLYPROPYLENE
  name = G4_POLYPROPYLENE
  specific = 4
FEATURE [App::DocumentObjectGroupPython] C_element086  label="C_element : 044"  # scripted group (container) (typed FeaturePython)
  n = 8
  ref = C_element
FEATURE [App::DocumentObjectGroupPython] H_element080  label="H_element : 042"  # scripted group (container) (typed FeaturePython)
  n = 8
  ref = H_element
FEATURE [App::DocumentObjectGroupPython] G4_POLYSTYRENE  # scripted group (container) (typed FeaturePython)
  Dunit = g/cm3
  Dvalue = 1.06
  Group = -> [C_element086,H_element080]
  conduct = 2
  density = 1
  expand = 3
  formula = G4_POLYSTYRENE
  name = G4_POLYSTYRENE
  specific = 4
FEATURE [App::DocumentObjectGroupPython] C_element087  label="C_element : 045"  # scripted group (container) (typed FeaturePython)
  n = 2
  ref = C_element
FEATURE [App::DocumentObjectGroupPython] F_element014  label="F_element : 4"  # scripted group (container) (typed FeaturePython)
  n = 4
  ref = F_element
FEATURE [App::DocumentObjectGroupPython] G4_TEFLON  # scripted group (container) (typed FeaturePython)
  Dunit = g/cm3
  Dvalue = 2.2
  Group = -> [C_element087,F_element014]
  conduct = 2
  density = 1
  expand = 3
  formula = G4_TEFLON
  name = G4_TEFLON
  specific = 4
FEATURE [App::DocumentObjectGroupPython] C_element088  label="C_element : 046"  # scripted group (container) (typed FeaturePython)
  n = 2
  ref = C_element
FEATURE [App::DocumentObjectGroupPython] F_element015  label="F_element : 006"  # scripted group (container) (typed FeaturePython)
  n = 3
  ref = F_element
FEATURE [App::DocumentObjectGroupPython] Cl_element018  label="Cl_element : 008"  # scripted group (container) (typed FeaturePython)
  n = 1
  ref = Cl_element
FEATURE [App::DocumentObjectGroupPython] G4_POLYTRIFLUOROCHLOROETHYLENE  # scripted group (container) (typed FeaturePython)
  Dunit = g/cm3
  Dvalue = 2.1
  Group = -> [C_element088,F_element015,Cl_element018]
  conduct = 2
  density = 1
  expand = 3
  formula = G4_POLYTRIFLUOROCHLOROETHYLENE
  name = G4_POLYTRIFLUOROCHLOROETHYLENE
  specific = 4
FEATURE [App::DocumentObjectGroupPython] C_element089  label="C_element : 047"  # scripted group (container) (typed FeaturePython)
  n = 4
  ref = C_element
FEATURE [App::DocumentObjectGroupPython] H_element081  label="H_element : 043"  # scripted group (container) (typed FeaturePython)
  n = 6
  ref = H_element
FEATURE [App::DocumentObjectGroupPython] O_element081  label="O_element : 042"  # scripted group (container) (typed FeaturePython)
  n = 2
  ref = O_element
FEATURE [App::DocumentObjectGroupPython] G4_POLYVINYL_ACETATE  # scripted group (container) (typed FeaturePython)
  Dunit = g/cm3
  Dvalue = 1.19
  Group = -> [C_element089,H_element081,O_element081]
  conduct = 2
  density = 1
  expand = 3
  formula = G4_POLYVINYL_ACETATE
  name = G4_POLYVINYL_ACETATE
  specific = 4
FEATURE [App::DocumentObjectGroupPython] C_element090  label="C_element : 048"  # scripted group (container) (typed FeaturePython)
  n = 2
  ref = C_element
FEATURE [App::DocumentObjectGroupPython] H_element082  label="H_element : 044"  # scripted group (container) (typed FeaturePython)
  n = 4
  ref = H_element
FEATURE [App::DocumentObjectGroupPython] O_element082  label="O_element : 043"  # scripted group (container) (typed FeaturePython)
  n = 1
  ref = O_element
FEATURE [App::DocumentObjectGroupPython] G4_POLYVINYL_ALCOHOL  # scripted group (container) (typed FeaturePython)
  Dunit = g/cm3
  Dvalue = 1.3
  Group = -> [C_element090,H_element082,O_element082]
  conduct = 2
  density = 1
  expand = 3
  formula = G4_POLYVINYL_ALCOHOL
  name = G4_POLYVINYL_ALCOHOL
  specific = 4
FEATURE [App::DocumentObjectGroupPython] C_element091  label="C_element : 049"  # scripted group (container) (typed FeaturePython)
  n = 8
  ref = C_element
FEATURE [App::DocumentObjectGroupPython] H_element083  label="H_element : 045"  # scripted group (container) (typed FeaturePython)
  n = 14
  ref = H_element
FEATURE [App::DocumentObjectGroupPython] O_element083  label="O_element : 044"  # scripted group (container) (typed FeaturePython)
  n = 2
  ref = O_element
FEATURE [App::DocumentObjectGroupPython] G4_POLYVINYL_BUTYRAL  # scripted group (container) (typed FeaturePython)
  Dunit = g/cm3
  Dvalue = 1.12
  Group = -> [C_element091,H_element083,O_element083]
  conduct = 2
  density = 1
  expand = 3
  formula = G4_POLYVINYL_BUTYRAL
  name = G4_POLYVINYL_BUTYRAL
  specific = 4
FEATURE [App::DocumentObjectGroupPython] C_element092  label="C_element : 050"  # scripted group (container) (typed FeaturePython)
  n = 2
  ref = C_element
FEATURE [App::DocumentObjectGroupPython] H_element084  label="H_element : 046"  # scripted group (container) (typed FeaturePython)
  n = 3
  ref = H_element
FEATURE [App::DocumentObjectGroupPython] Cl_element019  label="Cl_element : 009"  # scripted group (container) (typed FeaturePython)
  n = 1
  ref = Cl_element
FEATURE [App::DocumentObjectGroupPython] G4_POLYVINYL_CHLORIDE  # scripted group (container) (typed FeaturePython)
  Dunit = g/cm3
  Dvalue = 1.3
  Group = -> [C_element092,H_element084,Cl_element019]
  conduct = 2
  density = 1
  expand = 3
  formula = G4_POLYVINYL_CHLORIDE
  name = G4_POLYVINYL_CHLORIDE
  specific = 4
FEATURE [App::DocumentObjectGroupPython] C_element093  label="C_element : 051"  # scripted group (container) (typed FeaturePython)
  n = 2
  ref = C_element
FEATURE [App::DocumentObjectGroupPython] H_element085  label="H_element : 047"  # scripted group (container) (typed FeaturePython)
  n = 2
  ref = H_element
FEATURE [App::DocumentObjectGroupPython] Cl_element020  label="Cl_element : 010"  # scripted group (container) (typed FeaturePython)
  n = 2
  ref = Cl_element
FEATURE [App::DocumentObjectGroupPython] G4_POLYVINYLIDENE_CHLORIDE  # scripted group (container) (typed FeaturePython)
  Dunit = g/cm3
  Dvalue = 1.7
  Group = -> [C_element093,H_element085,Cl_element020]
  conduct = 2
  density = 1
  expand = 3
  formula = G4_POLYVINYLIDENE_CHLORIDE
  name = G4_POLYVINYLIDENE_CHLORIDE
  specific = 4
FEATURE [App::DocumentObjectGroupPython] C_element094  label="C_element : 052"  # scripted group (container) (typed FeaturePython)
  n = 2
  ref = C_element
FEATURE [App::DocumentObjectGroupPython] H_element086  label="H_element : 048"  # scripted group (container) (typed FeaturePython)
  n = 2
  ref = H_element
FEATURE [App::DocumentObjectGroupPython] F_element016  label="F_element : 007"  # scripted group (container) (typed FeaturePython)
  n = 2
  ref = F_element
FEATURE [App::DocumentObjectGroupPython] G4_POLYVINYLIDENE_FLUORIDE  # scripted group (container) (typed FeaturePython)
  Dunit = g/cm3
  Dvalue = 1.76
  Group = -> [C_element094,H_element086,F_element016]
  conduct = 2
  density = 1
  expand = 3
  formula = G4_POLYVINYLIDENE_FLUORIDE
  name = G4_POLYVINYLIDENE_FLUORIDE
  specific = 4
FEATURE [App::DocumentObjectGroupPython] C_element095  label="C_element : 053"  # scripted group (container) (typed FeaturePython)
  n = 6
  ref = C_element
FEATURE [App::DocumentObjectGroupPython] H_element087  label="H_element : 9"  # scripted group (container) (typed FeaturePython)
  n = 9
  ref = H_element
FEATURE [App::DocumentObjectGroupPython] N_element037  label="N_element : 016"  # scripted group (container) (typed FeaturePython)
  n = 1
  ref = N_element
FEATURE [App::DocumentObjectGroupPython] O_element084  label="O_element : 045"  # scripted group (container) (typed FeaturePython)
  n = 1
  ref = O_element
FEATURE [App::DocumentObjectGroupPython] G4_POLYVINYL_PYRROLIDONE  # scripted group (container) (typed FeaturePython)
  Dunit = g/cm3
  Dvalue = 1.25
  Group = -> [C_element095,H_element087,N_element037,O_element084]
  conduct = 2
  density = 1
  expand = 3
  formula = G4_POLYVINYL_PYRROLIDONE
  name = G4_POLYVINYL_PYRROLIDONE
  specific = 4
FEATURE [App::DocumentObjectGroupPython] K_element008  label="K_element : 1"  # scripted group (container) (typed FeaturePython)
  n = 1
  ref = K_element
FEATURE [App::DocumentObjectGroupPython] I_element006  label="I_element : 003"  # scripted group (container) (typed FeaturePython)
  n = 1
  ref = I_element
FEATURE [App::DocumentObjectGroupPython] G4_POTASSIUM_IODIDE  # scripted group (container) (typed FeaturePython)
  Dunit = g/cm3
  Dvalue = 3.13
  Group = -> [K_element008,I_element006]
  conduct = 2
  density = 1
  expand = 3
  formula = G4_POTASSIUM_IODIDE
  name = G4_POTASSIUM_IODIDE
  specific = 4
FEATURE [App::DocumentObjectGroupPython] K_element009  label="K_element : 2"  # scripted group (container) (typed FeaturePython)
  n = 2
  ref = K_element
FEATURE [App::DocumentObjectGroupPython] O_element085  label="O_element : 046"  # scripted group (container) (typed FeaturePython)
  n = 1
  ref = O_element
FEATURE [App::DocumentObjectGroupPython] G4_POTASSIUM_OXIDE  # scripted group (container) (typed FeaturePython)
  Dunit = g/cm3
  Dvalue = 2.32
  Group = -> [K_element009,O_element085]
  conduct = 2
  density = 1
  expand = 3
  formula = G4_POTASSIUM_OXIDE
  name = G4_POTASSIUM_OXIDE
  specific = 4
FEATURE [App::DocumentObjectGroupPython] C_element096  label="C_element : 054"  # scripted group (container) (typed FeaturePython)
  n = 3
  ref = C_element
FEATURE [App::DocumentObjectGroupPython] H_element088  label="H_element : 049"  # scripted group (container) (typed FeaturePython)
  n = 8
  ref = H_element
FEATURE [App::DocumentObjectGroupPython] G4_PROPANE  # scripted group (container) (typed FeaturePython)
  Dunit = g/cm3
  Dvalue = 0.00187939
  Group = -> [C_element096,H_element088]
  conduct = 2
  density = 1
  expand = 3
  formula = G4_PROPANE
  name = G4_PROPANE
  specific = 4
FEATURE [App::DocumentObjectGroupPython] C_element097  label="C_element : 055"  # scripted group (container) (typed FeaturePython)
  n = 3
  ref = C_element
FEATURE [App::DocumentObjectGroupPython] H_element089  label="H_element : 050"  # scripted group (container) (typed FeaturePython)
  n = 8
  ref = H_element
FEATURE [App::DocumentObjectGroupPython] G4_lPROPANE  # scripted group (container) (typed FeaturePython)
  Dunit = g/cm3
  Dvalue = 0.43
  Group = -> [C_element097,H_element089]
  conduct = 2
  density = 1
  expand = 3
  formula = G4_lPROPANE
  name = G4_lPROPANE
  specific = 4
FEATURE [App::DocumentObjectGroupPython] C_element098  label="C_element : 056"  # scripted group (container) (typed FeaturePython)
  n = 3
  ref = C_element
FEATURE [App::DocumentObjectGroupPython] H_element090  label="H_element : 051"  # scripted group (container) (typed FeaturePython)
  n = 8
  ref = H_element
FEATURE [App::DocumentObjectGroupPython] O_element086  label="O_element : 047"  # scripted group (container) (typed FeaturePython)
  n = 1
  ref = O_element
FEATURE [App::DocumentObjectGroupPython] G4_N_PROPYL_ALCOHOL  label="G4_N-PROPYL_ALCOHOL"  # scripted group (container) (typed FeaturePython)
  Dunit = g/cm3
  Dvalue = 0.8035
  Group = -> [C_element098,H_element090,O_element086]
  conduct = 2
  density = 1
  expand = 3
  formula = G4_N-PROPYL_ALCOHOL
  name = G4_N-PROPYL_ALCOHOL
  specific = 4
FEATURE [App::DocumentObjectGroupPython] C_element099  label="C_element : 057"  # scripted group (container) (typed FeaturePython)
  n = 5
  ref = C_element
FEATURE [App::DocumentObjectGroupPython] H_element091  label="H_element : 052"  # scripted group (container) (typed FeaturePython)
  n = 5
  ref = H_element
FEATURE [App::DocumentObjectGroupPython] N_element038  label="N_element : 017"  # scripted group (container) (typed FeaturePython)
  n = 1
  ref = N_element
FEATURE [App::DocumentObjectGroupPython] G4_PYRIDINE  # scripted group (container) (typed FeaturePython)
  Dunit = g/cm3
  Dvalue = 0.9819
  Group = -> [C_element099,H_element091,N_element038]
  conduct = 2
  density = 1
  expand = 3
  formula = G4_PYRIDINE
  name = G4_PYRIDINE
  specific = 4
FEATURE [App::DocumentObjectGroupPython] H_element092  label="H_element : 0.144"  # scripted group (container) (typed FeaturePython)
  n = 0.143711
FEATURE [App::DocumentObjectGroupPython] C_element100  label="C_element : 0.856"  # scripted group (container) (typed FeaturePython)
  n = 0.856289
FEATURE [App::DocumentObjectGroupPython] G4_RUBBER_BUTYL  # scripted group (container) (typed FeaturePython)
  Dunit = g/cm3
  Dvalue = 0.92
  Group = -> [H_element092,C_element100]
  conduct = 2
  density = 1
  expand = 3
  formula = G4_RUBBER_BUTYL
  name = G4_RUBBER_BUTYL
  specific = 4
FEATURE [App::DocumentObjectGroupPython] H_element093  label="H_element : 0.118"  # scripted group (container) (typed FeaturePython)
  n = 0.118371
FEATURE [App::DocumentObjectGroupPython] C_element101  label="C_element : 0.882"  # scripted group (container) (typed FeaturePython)
  n = 0.881629
FEATURE [App::DocumentObjectGroupPython] G4_RUBBER_NATURAL  # scripted group (container) (typed FeaturePython)
  Dunit = g/cm3
  Dvalue = 0.92
  Group = -> [H_element093,C_element101]
  conduct = 2
  density = 1
  expand = 3
  formula = G4_RUBBER_NATURAL
  name = G4_RUBBER_NATURAL
  specific = 4
FEATURE [App::DocumentObjectGroupPython] H_element094  label="H_element : 0.145"  # scripted group (container) (typed FeaturePython)
  n = 0.05692
FEATURE [App::DocumentObjectGroupPython] C_element102  label="C_element : 0.543"  # scripted group (container) (typed FeaturePython)
  n = 0.542646
FEATURE [App::DocumentObjectGroupPython] Cl_element021  label="Cl_element : 0.400"  # scripted group (container) (typed FeaturePython)
  n = 0.400434
FEATURE [App::DocumentObjectGroupPython] G4_RUBBER_NEOPRENE  # scripted group (container) (typed FeaturePython)
  Dunit = g/cm3
  Dvalue = 1.23
  Group = -> [H_element094,C_element102,Cl_element021]
  conduct = 2
  density = 1
  expand = 3
  formula = G4_RUBBER_NEOPRENE
  name = G4_RUBBER_NEOPRENE
  specific = 4
FEATURE [App::DocumentObjectGroupPython] Si_element006  label="Si_element : 1"  # scripted group (container) (typed FeaturePython)
  n = 1
  ref = Si_element
FEATURE [App::DocumentObjectGroupPython] O_element087  label="O_element : 048"  # scripted group (container) (typed FeaturePython)
  n = 2
  ref = O_element
FEATURE [App::DocumentObjectGroupPython] G4_SILICON_DIOXIDE  # scripted group (container) (typed FeaturePython)
  Dunit = g/cm3
  Dvalue = 2.32
  Group = -> [Si_element006,O_element087]
  conduct = 2
  density = 1
  expand = 3
  formula = G4_SILICON_DIOXIDE
  name = G4_SILICON_DIOXIDE
  specific = 4
FEATURE [App::DocumentObjectGroupPython] Ag_element002  label="Ag_element : 1"  # scripted group (container) (typed FeaturePython)
  n = 1
  ref = Ag_element
FEATURE [App::DocumentObjectGroupPython] Br_element005  label="Br_element : 003"  # scripted group (container) (typed FeaturePython)
  n = 1
  ref = Br_element
FEATURE [App::DocumentObjectGroupPython] G4_SILVER_BROMIDE  # scripted group (container) (typed FeaturePython)
  Dunit = g/cm3
  Dvalue = 6.473
  Group = -> [Ag_element002,Br_element005]
  conduct = 2
  density = 1
  expand = 3
  formula = G4_SILVER_BROMIDE
  name = G4_SILVER_BROMIDE
  specific = 4
FEATURE [App::DocumentObjectGroupPython] Ag_element003  label="Ag_element : 002"  # scripted group (container) (typed FeaturePython)
  n = 1
  ref = Ag_element
FEATURE [App::DocumentObjectGroupPython] Cl_element022  label="Cl_element : 011"  # scripted group (container) (typed FeaturePython)
  n = 1
  ref = Cl_element
FEATURE [App::DocumentObjectGroupPython] G4_SILVER_CHLORIDE  # scripted group (container) (typed FeaturePython)
  Dunit = g/cm3
  Dvalue = 5.56
  Group = -> [Ag_element003,Cl_element022]
  conduct = 2
  density = 1
  expand = 3
  formula = G4_SILVER_CHLORIDE
  name = G4_SILVER_CHLORIDE
  specific = 4
FEATURE [App::DocumentObjectGroupPython] Br_element006  label="Br_element : 0.423"  # scripted group (container) (typed FeaturePython)
  n = 0.422895
FEATURE [App::DocumentObjectGroupPython] Ag_element004  label="Ag_element : 0.574"  # scripted group (container) (typed FeaturePython)
  n = 0.573748
FEATURE [App::DocumentObjectGroupPython] I_element007  label="I_element : 0.649"  # scripted group (container) (typed FeaturePython)
  n = 0.003357
FEATURE [App::DocumentObjectGroupPython] G4_SILVER_HALIDES  # scripted group (container) (typed FeaturePython)
  Dunit = g/cm3
  Dvalue = 6.47
  Group = -> [Br_element006,Ag_element004,I_element007]
  conduct = 2
  density = 1
  expand = 3
  formula = G4_SILVER_HALIDES
  name = G4_SILVER_HALIDES
  specific = 4
FEATURE [App::DocumentObjectGroupPython] Ag_element005  label="Ag_element : 003"  # scripted group (container) (typed FeaturePython)
  n = 1
  ref = Ag_element
FEATURE [App::DocumentObjectGroupPython] I_element008  label="I_element : 004"  # scripted group (container) (typed FeaturePython)
  n = 1
  ref = I_element
FEATURE [App::DocumentObjectGroupPython] G4_SILVER_IODIDE  # scripted group (container) (typed FeaturePython)
  Dunit = g/cm3
  Dvalue = 6.01
  Group = -> [Ag_element005,I_element008]
  conduct = 2
  density = 1
  expand = 3
  formula = G4_SILVER_IODIDE
  name = G4_SILVER_IODIDE
  specific = 4
FEATURE [App::DocumentObjectGroupPython] H_element095  label="H_element : 0.100"  # scripted group (container) (typed FeaturePython)
  n = 0.1
FEATURE [App::DocumentObjectGroupPython] C_element103  label="C_element : 0.204"  # scripted group (container) (typed FeaturePython)
  n = 0.204
FEATURE [App::DocumentObjectGroupPython] N_element039  label="N_element : 0.759"  # scripted group (container) (typed FeaturePython)
  n = 0.042
FEATURE [App::DocumentObjectGroupPython] O_element088  label="O_element : 0.645"  # scripted group (container) (typed FeaturePython)
  n = 0.645
FEATURE [App::DocumentObjectGroupPython] Na_element013  label="Na_element : 0.100"  # scripted group (container) (typed FeaturePython)
  n = 0.002
FEATURE [App::DocumentObjectGroupPython] P_element009  label="P_element : 0.107"  # scripted group (container) (typed FeaturePython)
  n = 0.001
FEATURE [App::DocumentObjectGroupPython] S_element020  label="S_element : 0.021"  # scripted group (container) (typed FeaturePython)
  n = 0.002
FEATURE [App::DocumentObjectGroupPython] Cl_element023  label="Cl_element : 0.590"  # scripted group (container) (typed FeaturePython)
  n = 0.003
FEATURE [App::DocumentObjectGroupPython] K_element010  label="K_element : 0.001"  # scripted group (container) (typed FeaturePython)
  n = 0.001
FEATURE [App::DocumentObjectGroupPython] G4_SKIN_ICRP  # scripted group (container) (typed FeaturePython)
  Dunit = g/cm3
  Dvalue = 1.09
  Group = -> [H_element095,C_element103,N_element039,O_element088,Na_element013,P_element009,S_element020,Cl_element023,K_element010]
  conduct = 2
  density = 1
  expand = 3
  formula = G4_SKIN_ICRP
  name = G4_SKIN_ICRP
  specific = 4
FEATURE [App::DocumentObjectGroupPython] Na_element014  label="Na_element : 2"  # scripted group (container) (typed FeaturePython)
  n = 2
  ref = Na_element
FEATURE [App::DocumentObjectGroupPython] C_element104  label="C_element : 058"  # scripted group (container) (typed FeaturePython)
  n = 1
  ref = C_element
FEATURE [App::DocumentObjectGroupPython] O_element089  label="O_element : 049"  # scripted group (container) (typed FeaturePython)
  n = 3
  ref = O_element
FEATURE [App::DocumentObjectGroupPython] G4_SODIUM_CARBONATE  # scripted group (container) (typed FeaturePython)
  Dunit = g/cm3
  Dvalue = 2.532
  Group = -> [Na_element014,C_element104,O_element089]
  conduct = 2
  density = 1
  expand = 3
  formula = G4_SODIUM_CARBONATE
  name = G4_SODIUM_CARBONATE
  specific = 4
FEATURE [App::DocumentObjectGroupPython] Na_element015  label="Na_element : 1"  # scripted group (container) (typed FeaturePython)
  n = 1
  ref = Na_element
FEATURE [App::DocumentObjectGroupPython] I_element009  label="I_element : 005"  # scripted group (container) (typed FeaturePython)
  n = 1
  ref = I_element
FEATURE [App::DocumentObjectGroupPython] G4_SODIUM_IODIDE  # scripted group (container) (typed FeaturePython)
  Dunit = g/cm3
  Dvalue = 3.667
  Group = -> [Na_element015,I_element009]
  conduct = 2
  density = 1
  expand = 3
  formula = G4_SODIUM_IODIDE
  name = G4_SODIUM_IODIDE
  specific = 4
FEATURE [App::DocumentObjectGroupPython] Na_element016  label="Na_element : 003"  # scripted group (container) (typed FeaturePython)
  n = 2
  ref = Na_element
FEATURE [App::DocumentObjectGroupPython] O_element090  label="O_element : 050"  # scripted group (container) (typed FeaturePython)
  n = 1
  ref = O_element
FEATURE [App::DocumentObjectGroupPython] G4_SODIUM_MONOXIDE  # scripted group (container) (typed FeaturePython)
  Dunit = g/cm3
  Dvalue = 2.27
  Group = -> [Na_element016,O_element090]
  conduct = 2
  density = 1
  expand = 3
  formula = G4_SODIUM_MONOXIDE
  name = G4_SODIUM_MONOXIDE
  specific = 4
FEATURE [App::DocumentObjectGroupPython] Na_element017  label="Na_element : 004"  # scripted group (container) (typed FeaturePython)
  n = 1
  ref = Na_element
FEATURE [App::DocumentObjectGroupPython] N_element040  label="N_element : 018"  # scripted group (container) (typed FeaturePython)
  n = 1
  ref = N_element
FEATURE [App::DocumentObjectGroupPython] O_element091  label="O_element : 051"  # scripted group (container) (typed FeaturePython)
  n = 3
  ref = O_element
FEATURE [App::DocumentObjectGroupPython] G4_SODIUM_NITRATE  # scripted group (container) (typed FeaturePython)
  Dunit = g/cm3
  Dvalue = 2.261
  Group = -> [Na_element017,N_element040,O_element091]
  conduct = 2
  density = 1
  expand = 3
  formula = G4_SODIUM_NITRATE
  name = G4_SODIUM_NITRATE
  specific = 4
FEATURE [App::DocumentObjectGroupPython] C_element105  label="C_element : 059"  # scripted group (container) (typed FeaturePython)
  n = 14
  ref = C_element
FEATURE [App::DocumentObjectGroupPython] H_element096  label="H_element : 053"  # scripted group (container) (typed FeaturePython)
  n = 12
  ref = H_element
FEATURE [App::DocumentObjectGroupPython] G4_STILBENE  # scripted group (container) (typed FeaturePython)
  Dunit = g/cm3
  Dvalue = 0.9707
  Group = -> [C_element105,H_element096]
  conduct = 2
  density = 1
  expand = 3
  formula = G4_STILBENE
  name = G4_STILBENE
  specific = 4
FEATURE [App::DocumentObjectGroupPython] C_element106  label="C_element : 12"  # scripted group (container) (typed FeaturePython)
  n = 12
  ref = C_element
FEATURE [App::DocumentObjectGroupPython] H_element097  label="H_element : 22"  # scripted group (container) (typed FeaturePython)
  n = 22
  ref = H_element
FEATURE [App::DocumentObjectGroupPython] O_element092  label="O_element : 11"  # scripted group (container) (typed FeaturePython)
  n = 11
  ref = O_element
FEATURE [App::DocumentObjectGroupPython] G4_SUCROSE  # scripted group (container) (typed FeaturePython)
  Dunit = g/cm3
  Dvalue = 1.5805
  Group = -> [C_element106,H_element097,O_element092]
  conduct = 2
  density = 1
  expand = 3
  formula = G4_SUCROSE
  name = G4_SUCROSE
  specific = 4
FEATURE [App::DocumentObjectGroupPython] C_element107  label="C_element : 18"  # scripted group (container) (typed FeaturePython)
  n = 18
  ref = C_element
FEATURE [App::DocumentObjectGroupPython] H_element098  label="H_element : 054"  # scripted group (container) (typed FeaturePython)
  n = 14
  ref = H_element
FEATURE [App::DocumentObjectGroupPython] G4_TERPHENYL  # scripted group (container) (typed FeaturePython)
  Dunit = g/cm3
  Dvalue = 1.24
  Group = -> [C_element107,H_element098]
  conduct = 2
  density = 1
  expand = 3
  formula = G4_TERPHENYL
  name = G4_TERPHENYL
  specific = 4
FEATURE [App::DocumentObjectGroupPython] H_element099  label="H_element : 0.146"  # scripted group (container) (typed FeaturePython)
  n = 0.106
FEATURE [App::DocumentObjectGroupPython] C_element108  label="C_element : 0.883"  # scripted group (container) (typed FeaturePython)
  n = 0.099
FEATURE [App::DocumentObjectGroupPython] N_element041  label="N_element : 0.020"  # scripted group (container) (typed FeaturePython)
  n = 0.02
FEATURE [App::DocumentObjectGroupPython] O_element093  label="O_element : 0.766"  # scripted group (container) (typed FeaturePython)
  n = 0.766
FEATURE [App::DocumentObjectGroupPython] Na_element018  label="Na_element : 0.101"  # scripted group (container) (typed FeaturePython)
  n = 0.002
FEATURE [App::DocumentObjectGroupPython] P_element010  label="P_element : 0.108"  # scripted group (container) (typed FeaturePython)
  n = 0.001
FEATURE [App::DocumentObjectGroupPython] S_element021  label="S_element : 0.022"  # scripted group (container) (typed FeaturePython)
  n = 0.002
FEATURE [App::DocumentObjectGroupPython] Cl_element024  label="Cl_element : 0.002"  # scripted group (container) (typed FeaturePython)
  n = 0.002
FEATURE [App::DocumentObjectGroupPython] K_element011  label="K_element : 0.017"  # scripted group (container) (typed FeaturePython)
  n = 0.002
FEATURE [App::DocumentObjectGroupPython] G4_TESTIS_ICRP  # scripted group (container) (typed FeaturePython)
  Dunit = g/cm3
  Dvalue = 1.04
  Group = -> [H_element099,C_element108,N_element041,O_element093,Na_element018,P_element010,S_element021,Cl_element024,K_element011]
  conduct = 2
  density = 1
  expand = 3
  formula = G4_TESTIS_ICRP
  name = G4_TESTIS_ICRP
  specific = 4
FEATURE [App::DocumentObjectGroupPython] C_element109  label="C_element : 060"  # scripted group (container) (typed FeaturePython)
  n = 2
  ref = C_element
FEATURE [App::DocumentObjectGroupPython] Cl_element025  label="Cl_element : 012"  # scripted group (container) (typed FeaturePython)
  n = 4
  ref = Cl_element
FEATURE [App::DocumentObjectGroupPython] G4_TETRACHLOROETHYLENE  # scripted group (container) (typed FeaturePython)
  Dunit = g/cm3
  Dvalue = 1.625
  Group = -> [C_element109,Cl_element025]
  conduct = 2
  density = 1
  expand = 3
  formula = G4_TETRACHLOROETHYLENE
  name = G4_TETRACHLOROETHYLENE
  specific = 4
FEATURE [App::DocumentObjectGroupPython] Tl_element001  label="Tl_element : 1"  # scripted group (container) (typed FeaturePython)
  n = 1
  ref = Tl_element
FEATURE [App::DocumentObjectGroupPython] Cl_element026  label="Cl_element : 013"  # scripted group (container) (typed FeaturePython)
  n = 1
  ref = Cl_element
FEATURE [App::DocumentObjectGroupPython] G4_THALLIUM_CHLORIDE  # scripted group (container) (typed FeaturePython)
  Dunit = g/cm3
  Dvalue = 7.004
  Group = -> [Tl_element001,Cl_element026]
  conduct = 2
  density = 1
  expand = 3
  formula = G4_THALLIUM_CHLORIDE
  name = G4_THALLIUM_CHLORIDE
  specific = 4
FEATURE [App::DocumentObjectGroupPython] H_element100  label="H_element : 0.147"  # scripted group (container) (typed FeaturePython)
  n = 0.105
FEATURE [App::DocumentObjectGroupPython] C_element110  label="C_element : 0.256"  # scripted group (container) (typed FeaturePython)
  n = 0.256
FEATURE [App::DocumentObjectGroupPython] N_element042  label="N_element : 0.760"  # scripted group (container) (typed FeaturePython)
  n = 0.027
FEATURE [App::DocumentObjectGroupPython] O_element094  label="O_element : 0.602"  # scripted group (container) (typed FeaturePython)
  n = 0.602
FEATURE [App::DocumentObjectGroupPython] Na_element019  label="Na_element : 0.102"  # scripted group (container) (typed FeaturePython)
  n = 0.001
FEATURE [App::DocumentObjectGroupPython] P_element011  label="P_element : 0.109"  # scripted group (container) (typed FeaturePython)
  n = 0.002
FEATURE [App::DocumentObjectGroupPython] S_element022  label="S_element : 0.023"  # scripted group (container) (typed FeaturePython)
  n = 0.003
FEATURE [App::DocumentObjectGroupPython] Cl_element027  label="Cl_element : 0.591"  # scripted group (container) (typed FeaturePython)
  n = 0.002
FEATURE [App::DocumentObjectGroupPython] K_element012  label="K_element : 0.018"  # scripted group (container) (typed FeaturePython)
  n = 0.002
FEATURE [App::DocumentObjectGroupPython] G4_TISSUE_SOFT_ICRP  # scripted group (container) (typed FeaturePython)
  Dunit = g/cm3
  Dvalue = 1.03
  Group = -> [H_element100,C_element110,N_element042,O_element094,Na_element019,P_element011,S_element022,Cl_element027,K_element012]
  conduct = 2
  density = 1
  expand = 3
  formula = G4_TISSUE_SOFT_ICRP
  name = G4_TISSUE_SOFT_ICRP
  specific = 4
FEATURE [App::DocumentObjectGroupPython] H_element101  label="H_element : 0.148"  # scripted group (container) (typed FeaturePython)
  n = 0.101
FEATURE [App::DocumentObjectGroupPython] C_element111  label="C_element : 0.111"  # scripted group (container) (typed FeaturePython)
  n = 0.111
FEATURE [App::DocumentObjectGroupPython] N_element043  label="N_element : 0.026"  # scripted group (container) (typed FeaturePython)
  n = 0.026
FEATURE [App::DocumentObjectGroupPython] O_element095  label="O_element : 0.762"  # scripted group (container) (typed FeaturePython)
  n = 0.762
FEATURE [App::DocumentObjectGroupPython] G4_TISSUE_SOFT_ICRU_4  label="G4_TISSUE_SOFT_ICRU-4"  # scripted group (container) (typed FeaturePython)
  Dunit = g/cm3
  Dvalue = 1
  Group = -> [H_element101,C_element111,N_element043,O_element095]
  conduct = 2
  density = 1
  expand = 3
  formula = G4_TISSUE_SOFT_ICRU-4
  name = G4_TISSUE_SOFT_ICRU-4
  specific = 4
FEATURE [App::DocumentObjectGroupPython] H_element102  label="H_element : 0.149"  # scripted group (container) (typed FeaturePython)
  n = 0.101869
FEATURE [App::DocumentObjectGroupPython] C_element112  label="C_element : 0.456"  # scripted group (container) (typed FeaturePython)
  n = 0.456179
FEATURE [App::DocumentObjectGroupPython] N_element044  label="N_element : 0.761"  # scripted group (container) (typed FeaturePython)
  n = 0.035172
FEATURE [App::DocumentObjectGroupPython] O_element096  label="O_element : 0.407"  # scripted group (container) (typed FeaturePython)
  n = 0.40678
FEATURE [App::DocumentObjectGroupPython] G4_TISSUE_METHANE  label="G4_TISSUE-METHANE"  # scripted group (container) (typed FeaturePython)
  Dunit = g/cm3
  Dvalue = 0.00106409
  Group = -> [H_element102,C_element112,N_element044,O_element096]
  conduct = 2
  density = 1
  expand = 3
  formula = G4_TISSUE-METHANE
  name = G4_TISSUE-METHANE
  specific = 4
FEATURE [App::DocumentObjectGroupPython] H_element103  label="H_element : 0.103"  # scripted group (container) (typed FeaturePython)
  n = 0.102672
FEATURE [App::DocumentObjectGroupPython] C_element113  label="C_element : 0.569"  # scripted group (container) (typed FeaturePython)
  n = 0.56894
FEATURE [App::DocumentObjectGroupPython] N_element045  label="N_element : 0.762"  # scripted group (container) (typed FeaturePython)
  n = 0.035022
FEATURE [App::DocumentObjectGroupPython] O_element097  label="O_element : 0.293"  # scripted group (container) (typed FeaturePython)
  n = 0.293366
FEATURE [App::DocumentObjectGroupPython] G4_TISSUE_PROPANE  label="G4_TISSUE-PROPANE"  # scripted group (container) (typed FeaturePython)
  Dunit = g/cm3
  Dvalue = 0.00182628
  Group = -> [H_element103,C_element113,N_element045,O_element097]
  conduct = 2
  density = 1
  expand = 3
  formula = G4_TISSUE-PROPANE
  name = G4_TISSUE-PROPANE
  specific = 4
FEATURE [App::DocumentObjectGroupPython] Ti_element003  label="Ti_element : 1"  # scripted group (container) (typed FeaturePython)
  n = 1
  ref = Ti_element
FEATURE [App::DocumentObjectGroupPython] O_element098  label="O_element : 052"  # scripted group (container) (typed FeaturePython)
  n = 2
  ref = O_element
FEATURE [App::DocumentObjectGroupPython] G4_TITANIUM_DIOXIDE  # scripted group (container) (typed FeaturePython)
  Dunit = g/cm3
  Dvalue = 4.26
  Group = -> [Ti_element003,O_element098]
  conduct = 2
  density = 1
  expand = 3
  formula = G4_TITANIUM_DIOXIDE
  name = G4_TITANIUM_DIOXIDE
  specific = 4
FEATURE [App::DocumentObjectGroupPython] C_element114  label="C_element : 061"  # scripted group (container) (typed FeaturePython)
  n = 7
  ref = C_element
FEATURE [App::DocumentObjectGroupPython] H_element104  label="H_element : 055"  # scripted group (container) (typed FeaturePython)
  n = 8
  ref = H_element
FEATURE [App::DocumentObjectGroupPython] G4_TOLUENE  # scripted group (container) (typed FeaturePython)
  Dunit = g/cm3
  Dvalue = 0.8669
  Group = -> [C_element114,H_element104]
  conduct = 2
  density = 1
  expand = 3
  formula = G4_TOLUENE
  name = G4_TOLUENE
  specific = 4
FEATURE [App::DocumentObjectGroupPython] C_element115  label="C_element : 062"  # scripted group (container) (typed FeaturePython)
  n = 2
  ref = C_element
FEATURE [App::DocumentObjectGroupPython] H_element105  label="H_element : 056"  # scripted group (container) (typed FeaturePython)
  n = 1
  ref = H_element
FEATURE [App::DocumentObjectGroupPython] Cl_element028  label="Cl_element : 014"  # scripted group (container) (typed FeaturePython)
  n = 3
  ref = Cl_element
FEATURE [App::DocumentObjectGroupPython] G4_TRICHLOROETHYLENE  # scripted group (container) (typed FeaturePython)
  Dunit = g/cm3
  Dvalue = 1.46
  Group = -> [C_element115,H_element105,Cl_element028]
  conduct = 2
  density = 1
  expand = 3
  formula = G4_TRICHLOROETHYLENE
  name = G4_TRICHLOROETHYLENE
  specific = 4
FEATURE [App::DocumentObjectGroupPython] C_element116  label="C_element : 063"  # scripted group (container) (typed FeaturePython)
  n = 6
  ref = C_element
FEATURE [App::DocumentObjectGroupPython] H_element106  label="H_element : 15"  # scripted group (container) (typed FeaturePython)
  n = 15
  ref = H_element
FEATURE [App::DocumentObjectGroupPython] O_element099  label="O_element : 053"  # scripted group (container) (typed FeaturePython)
  n = 4
  ref = O_element
FEATURE [App::DocumentObjectGroupPython] P_element012  label="P_element : 1"  # scripted group (container) (typed FeaturePython)
  n = 1
  ref = P_element
FEATURE [App::DocumentObjectGroupPython] G4_TRIETHYL_PHOSPHATE  # scripted group (container) (typed FeaturePython)
  Dunit = g/cm3
  Dvalue = 1.07
  Group = -> [C_element116,H_element106,O_element099,P_element012]
  conduct = 2
  density = 1
  expand = 3
  formula = G4_TRIETHYL_PHOSPHATE
  name = G4_TRIETHYL_PHOSPHATE
  specific = 4
FEATURE [App::DocumentObjectGroupPython] W_element003  label="W_element : 003"  # scripted group (container) (typed FeaturePython)
  n = 1
  ref = W_element
FEATURE [App::DocumentObjectGroupPython] F_element017  label="F_element : 6"  # scripted group (container) (typed FeaturePython)
  n = 6
  ref = F_element
FEATURE [App::DocumentObjectGroupPython] G4_TUNGSTEN_HEXAFLUORIDE  # scripted group (container) (typed FeaturePython)
  Dunit = g/cm3
  Dvalue = 2.4
  Group = -> [W_element003,F_element017]
  conduct = 2
  density = 1
  expand = 3
  formula = G4_TUNGSTEN_HEXAFLUORIDE
  name = G4_TUNGSTEN_HEXAFLUORIDE
  specific = 4
FEATURE [App::DocumentObjectGroupPython] U_element001  label="U_element : 1"  # scripted group (container) (typed FeaturePython)
  n = 1
  ref = U_element
FEATURE [App::DocumentObjectGroupPython] C_element117  label="C_element : 064"  # scripted group (container) (typed FeaturePython)
  n = 2
  ref = C_element
FEATURE [App::DocumentObjectGroupPython] G4_URANIUM_DICARBIDE  # scripted group (container) (typed FeaturePython)
  Dunit = g/cm3
  Dvalue = 11.28
  Group = -> [U_element001,C_element117]
  conduct = 2
  density = 1
  expand = 3
  formula = G4_URANIUM_DICARBIDE
  name = G4_URANIUM_DICARBIDE
  specific = 4
FEATURE [App::DocumentObjectGroupPython] U_element002  label="U_element : 002"  # scripted group (container) (typed FeaturePython)
  n = 1
  ref = U_element
FEATURE [App::DocumentObjectGroupPython] C_element118  label="C_element : 065"  # scripted group (container) (typed FeaturePython)
  n = 1
  ref = C_element
FEATURE [App::DocumentObjectGroupPython] G4_URANIUM_MONOCARBIDE  # scripted group (container) (typed FeaturePython)
  Dunit = g/cm3
  Dvalue = 13.63
  Group = -> [U_element002,C_element118]
  conduct = 2
  density = 1
  expand = 3
  formula = G4_URANIUM_MONOCARBIDE
  name = G4_URANIUM_MONOCARBIDE
  specific = 4
FEATURE [App::DocumentObjectGroupPython] U_element003  label="U_element : 003"  # scripted group (container) (typed FeaturePython)
  n = 1
  ref = U_element
FEATURE [App::DocumentObjectGroupPython] O_element100  label="O_element : 054"  # scripted group (container) (typed FeaturePython)
  n = 2
  ref = O_element
FEATURE [App::DocumentObjectGroupPython] G4_URANIUM_OXIDE  # scripted group (container) (typed FeaturePython)
  Dunit = g/cm3
  Dvalue = 10.96
  Group = -> [U_element003,O_element100]
  conduct = 2
  density = 1
  expand = 3
  formula = G4_URANIUM_OXIDE
  name = G4_URANIUM_OXIDE
  specific = 4
FEATURE [App::DocumentObjectGroupPython] C_element119  label="C_element : 066"  # scripted group (container) (typed FeaturePython)
  n = 1
  ref = C_element
FEATURE [App::DocumentObjectGroupPython] H_element107  label="H_element : 057"  # scripted group (container) (typed FeaturePython)
  n = 4
  ref = H_element
FEATURE [App::DocumentObjectGroupPython] N_element046  label="N_element : 019"  # scripted group (container) (typed FeaturePython)
  n = 2
  ref = N_element
FEATURE [App::DocumentObjectGroupPython] O_element101  label="O_element : 055"  # scripted group (container) (typed FeaturePython)
  n = 1
  ref = O_element
FEATURE [App::DocumentObjectGroupPython] G4_UREA  # scripted group (container) (typed FeaturePython)
  Dunit = g/cm3
  Dvalue = 1.323
  Group = -> [C_element119,H_element107,N_element046,O_element101]
  conduct = 2
  density = 1
  expand = 3
  formula = G4_UREA
  name = G4_UREA
  specific = 4
FEATURE [App::DocumentObjectGroupPython] C_element120  label="C_element : 067"  # scripted group (container) (typed FeaturePython)
  n = 5
  ref = C_element
FEATURE [App::DocumentObjectGroupPython] H_element108  label="H_element : 058"  # scripted group (container) (typed FeaturePython)
  n = 11
  ref = H_element
FEATURE [App::DocumentObjectGroupPython] N_element047  label="N_element : 020"  # scripted group (container) (typed FeaturePython)
  n = 1
  ref = N_element
FEATURE [App::DocumentObjectGroupPython] O_element102  label="O_element : 056"  # scripted group (container) (typed FeaturePython)
  n = 2
  ref = O_element
FEATURE [App::DocumentObjectGroupPython] G4_VALINE  # scripted group (container) (typed FeaturePython)
  Dunit = g/cm3
  Dvalue = 1.23
  Group = -> [C_element120,H_element108,N_element047,O_element102]
  conduct = 2
  density = 1
  expand = 3
  formula = G4_VALINE
  name = G4_VALINE
  specific = 4
FEATURE [App::DocumentObjectGroupPython] H_element109  label="H_element : 0.009"  # scripted group (container) (typed FeaturePython)
  n = 0.009417
FEATURE [App::DocumentObjectGroupPython] C_element121  label="C_element : 0.281"  # scripted group (container) (typed FeaturePython)
  n = 0.280555
FEATURE [App::DocumentObjectGroupPython] F_element018  label="F_element : 0.710"  # scripted group (container) (typed FeaturePython)
  n = 0.710028
FEATURE [App::DocumentObjectGroupPython] G4_VITON  # scripted group (container) (typed FeaturePython)
  Dunit = g/cm3
  Dvalue = 1.8
  Group = -> [H_element109,C_element121,F_element018]
  conduct = 2
  density = 1
  expand = 3
  formula = G4_VITON
  name = G4_VITON
  specific = 4
FEATURE [App::DocumentObjectGroupPython] H_element110  label="H_element : 059"  # scripted group (container) (typed FeaturePython)
  n = 2
  ref = H_element
FEATURE [App::DocumentObjectGroupPython] O_element103  label="O_element : 057"  # scripted group (container) (typed FeaturePython)
  n = 1
  ref = O_element
FEATURE [App::DocumentObjectGroupPython] G4_WATER  # scripted group (container) (typed FeaturePython)
  Dunit = g/cm3
  Dvalue = 1
  Group = -> [H_element110,O_element103]
  conduct = 2
  density = 1
  expand = 3
  formula = G4_WATER
  name = G4_WATER
  specific = 4
FEATURE [App::DocumentObjectGroupPython] H_element111  label="H_element : 060"  # scripted group (container) (typed FeaturePython)
  n = 2
  ref = H_element
FEATURE [App::DocumentObjectGroupPython] O_element104  label="O_element : 058"  # scripted group (container) (typed FeaturePython)
  n = 1
  ref = O_element
FEATURE [App::DocumentObjectGroupPython] G4_WATER_VAPOR  # scripted group (container) (typed FeaturePython)
  Dunit = g/cm3
  Dvalue = 0.000756182
  Group = -> [H_element111,O_element104]
  conduct = 2
  density = 1
  expand = 3
  formula = G4_WATER_VAPOR
  name = G4_WATER_VAPOR
  specific = 4
FEATURE [App::DocumentObjectGroupPython] C_element122  label="C_element : 068"  # scripted group (container) (typed FeaturePython)
  n = 8
  ref = C_element
FEATURE [App::DocumentObjectGroupPython] H_element112  label="H_element : 061"  # scripted group (container) (typed FeaturePython)
  n = 10
  ref = H_element
FEATURE [App::DocumentObjectGroupPython] G4_XYLENE  # scripted group (container) (typed FeaturePython)
  Dunit = g/cm3
  Dvalue = 0.87
  Group = -> [C_element122,H_element112]
  conduct = 2
  density = 1
  expand = 3
  formula = G4_XYLENE
  name = G4_XYLENE
  specific = 4
FEATURE [App::DocumentObjectGroupPython] C_element123  label="C_element : 069"  # scripted group (container) (typed FeaturePython)
  n = 1
  ref = C_element
FEATURE [App::DocumentObjectGroupPython] G4_GRAPHITE  # scripted group (container) (typed FeaturePython)
  Dunit = g/cm3
  Dvalue = 2.21
  Group = -> [C_element123]
  conduct = 2
  density = 1
  expand = 3
  formula = G4_GRAPHITE
  name = G4_GRAPHITE
  specific = 4
FEATURE [App::DocumentObjectGroupPython] NIST  # scripted group (container) (typed FeaturePython)
  Group = -> [G4_A_150_TISSUE,G4_ACETONE,G4_ACETYLENE,G4_ADENINE,G4_ADIPOSE_TISSUE_ICRP,G4_AIR,G4_ALANINE,G4_ALUMINUM_OXIDE,G4_AMBER,G4_AMMONIA,G4_ANILINE,G4_ANTHRACENE,G4_B_100_BONE,G4_BAKELITE,G4_BARIUM_FLUORIDE,G4_BARIUM_SULFATE,G4_BENZENE,G4_BERYLLIUM_OXIDE,G4_BGO,G4_BLOOD_ICRP,G4_BONE_COMPACT_ICRU,G4_BONE_CORTICAL_ICRP,G4_BORON_CARBIDE,G4_BORON_OXIDE,G4_BRAIN_ICRP,G4_BUTANE,G4_N_BUTYL_ALCOHOL,G4_C_552,+152 more]
FEATURE [App::DocumentObjectGroupPython] H_element113  label="H_element : 062"  # scripted group (container) (typed FeaturePython)
  n = 1
  ref = H_element
FEATURE [App::DocumentObjectGroupPython] G4_H  # scripted group (container) (typed FeaturePython)
  Dunit = g/cm3
  Dvalue = 8.3748e-05
  Group = -> [H_element113]
  conduct = 2
  density = 1
  expand = 3
  formula = H
  name = G4_H
  specific = 4
FEATURE [App::DocumentObjectGroupPython] He_element001  label="He_element : 1"  # scripted group (container) (typed FeaturePython)
  n = 1
  ref = He_element
FEATURE [App::DocumentObjectGroupPython] G4_He  # scripted group (container) (typed FeaturePython)
  Dunit = g/cm3
  Dvalue = 0.000166322
  Group = -> [He_element001]
  conduct = 2
  density = 1
  expand = 3
  formula = He
  name = G4_He
  specific = 4
FEATURE [App::DocumentObjectGroupPython] Li_element008  label="Li_element : 008"  # scripted group (container) (typed FeaturePython)
  n = 1
  ref = Li_element
FEATURE [App::DocumentObjectGroupPython] G4_Li  # scripted group (container) (typed FeaturePython)
  Dunit = g/cm3
  Dvalue = 0.534
  Group = -> [Li_element008]
  conduct = 2
  density = 1
  expand = 3
  formula = Li
  name = G4_Li
  specific = 4
FEATURE [App::DocumentObjectGroupPython] Be_element002  label="Be_element : 002"  # scripted group (container) (typed FeaturePython)
  n = 1
  ref = Be_element
FEATURE [App::DocumentObjectGroupPython] G4_Be  # scripted group (container) (typed FeaturePython)
  Dunit = g/cm3
  Dvalue = 1.848
  Group = -> [Be_element002]
  conduct = 2
  density = 1
  expand = 3
  formula = Be
  name = G4_Be
  specific = 4
FEATURE [App::DocumentObjectGroupPython] B_element007  label="B_element : 007"  # scripted group (container) (typed FeaturePython)
  n = 1
  ref = B_element
FEATURE [App::DocumentObjectGroupPython] G4_B  # scripted group (container) (typed FeaturePython)
  Dunit = g/cm3
  Dvalue = 2.37
  Group = -> [B_element007]
  conduct = 2
  density = 1
  expand = 3
  formula = B
  name = G4_B
  specific = 4
FEATURE [App::DocumentObjectGroupPython] C_element124  label="C_element : 070"  # scripted group (container) (typed FeaturePython)
  n = 1
  ref = C_element
FEATURE [App::DocumentObjectGroupPython] G4_C  # scripted group (container) (typed FeaturePython)
  Dunit = g/cm3
  Dvalue = 2
  Group = -> [C_element124]
  conduct = 2
  density = 1
  expand = 3
  formula = C
  name = G4_C
  specific = 4
FEATURE [App::DocumentObjectGroupPython] N_element048  label="N_element : 021"  # scripted group (container) (typed FeaturePython)
  n = 1
  ref = N_element
FEATURE [App::DocumentObjectGroupPython] G4_N  # scripted group (container) (typed FeaturePython)
  Dunit = g/cm3
  Dvalue = 0.0011652
  Group = -> [N_element048]
  conduct = 2
  density = 1
  expand = 3
  formula = N
  name = G4_N
  specific = 4
FEATURE [App::DocumentObjectGroupPython] O_element105  label="O_element : 059"  # scripted group (container) (typed FeaturePython)
  n = 1
  ref = O_element
FEATURE [App::DocumentObjectGroupPython] G4_O  # scripted group (container) (typed FeaturePython)
  Dunit = g/cm3
  Dvalue = 0.00133151
  Group = -> [O_element105]
  conduct = 2
  density = 1
  expand = 3
  formula = O
  name = G4_O
  specific = 4
FEATURE [App::DocumentObjectGroupPython] F_element019  label="F_element : 008"  # scripted group (container) (typed FeaturePython)
  n = 1
  ref = F_element
FEATURE [App::DocumentObjectGroupPython] G4_F  # scripted group (container) (typed FeaturePython)
  Dunit = g/cm3
  Dvalue = 0.00158029
  Group = -> [F_element019]
  conduct = 2
  density = 1
  expand = 3
  formula = F
  name = G4_F
  specific = 4
FEATURE [App::DocumentObjectGroupPython] Ne_element001  label="Ne_element : 1"  # scripted group (container) (typed FeaturePython)
  n = 1
  ref = Ne_element
FEATURE [App::DocumentObjectGroupPython] G4_Ne  # scripted group (container) (typed FeaturePython)
  Dunit = g/cm3
  Dvalue = 0.000838505
  Group = -> [Ne_element001]
  conduct = 2
  density = 1
  expand = 3
  formula = Ne
  name = G4_Ne
  specific = 4
FEATURE [App::DocumentObjectGroupPython] Na_element020  label="Na_element : 005"  # scripted group (container) (typed FeaturePython)
  n = 1
  ref = Na_element
FEATURE [App::DocumentObjectGroupPython] G4_Na  # scripted group (container) (typed FeaturePython)
  Dunit = g/cm3
  Dvalue = 0.971
  Group = -> [Na_element020]
  conduct = 2
  density = 1
  expand = 3
  formula = Na
  name = G4_Na
  specific = 4
FEATURE [App::DocumentObjectGroupPython] Mg_element011  label="Mg_element : 005"  # scripted group (container) (typed FeaturePython)
  n = 1
  ref = Mg_element
FEATURE [App::DocumentObjectGroupPython] G4_Mg  # scripted group (container) (typed FeaturePython)
  Dunit = g/cm3
  Dvalue = 1.74
  Group = -> [Mg_element011]
  conduct = 2
  density = 1
  expand = 3
  formula = Mg
  name = G4_Mg
  specific = 4
FEATURE [App::DocumentObjectGroupPython] Al_element004  label="Al_element : 1"  # scripted group (container) (typed FeaturePython)
  n = 1
  ref = Al_element
FEATURE [App::DocumentObjectGroupPython] G4_Al  # scripted group (container) (typed FeaturePython)
  Dunit = g/cm3
  Dvalue = 2.699
  Group = -> [Al_element004]
  conduct = 2
  density = 1
  expand = 3
  formula = Al
  name = G4_Al
  specific = 4
FEATURE [App::DocumentObjectGroupPython] Si_element007  label="Si_element : 002"  # scripted group (container) (typed FeaturePython)
  n = 1
  ref = Si_element
FEATURE [App::DocumentObjectGroupPython] G4_Si  # scripted group (container) (typed FeaturePython)
  Dunit = g/cm3
  Dvalue = 2.33
  Group = -> [Si_element007]
  conduct = 2
  density = 1
  expand = 3
  formula = Si
  name = G4_Si
  specific = 4
FEATURE [App::DocumentObjectGroupPython] P_element013  label="P_element : 002"  # scripted group (container) (typed FeaturePython)
  n = 1
  ref = P_element
FEATURE [App::DocumentObjectGroupPython] G4_P  # scripted group (container) (typed FeaturePython)
  Dunit = g/cm3
  Dvalue = 2.2
  Group = -> [P_element013]
  conduct = 2
  density = 1
  expand = 3
  formula = P
  name = G4_P
  specific = 4
FEATURE [App::DocumentObjectGroupPython] S_element023  label="S_element : 007"  # scripted group (container) (typed FeaturePython)
  n = 1
  ref = S_element
FEATURE [App::DocumentObjectGroupPython] G4_S  # scripted group (container) (typed FeaturePython)
  Dunit = g/cm3
  Dvalue = 2
  Group = -> [S_element023]
  conduct = 2
  density = 1
  expand = 3
  formula = S
  name = G4_S
  specific = 4
FEATURE [App::DocumentObjectGroupPython] Cl_element029  label="Cl_element : 015"  # scripted group (container) (typed FeaturePython)
  n = 1
  ref = Cl_element
FEATURE [App::DocumentObjectGroupPython] G4_Cl  # scripted group (container) (typed FeaturePython)
  Dunit = g/cm3
  Dvalue = 0.00299473
  Group = -> [Cl_element029]
  conduct = 2
  density = 1
  expand = 3
  formula = Cl
  name = G4_Cl
  specific = 4
FEATURE [App::DocumentObjectGroupPython] Ar_element002  label="Ar_element : 1"  # scripted group (container) (typed FeaturePython)
  n = 1
  ref = Ar_element
FEATURE [App::DocumentObjectGroupPython] G4_Ar  # scripted group (container) (typed FeaturePython)
  Dunit = g/cm3
  Dvalue = 0.00166201
  Group = -> [Ar_element002]
  conduct = 2
  density = 1
  expand = 3
  formula = Ar
  name = G4_Ar
  specific = 4
FEATURE [App::DocumentObjectGroupPython] K_element013  label="K_element : 003"  # scripted group (container) (typed FeaturePython)
  n = 1
  ref = K_element
FEATURE [App::DocumentObjectGroupPython] G4_K  # scripted group (container) (typed FeaturePython)
  Dunit = g/cm3
  Dvalue = 0.862
  Group = -> [K_element013]
  conduct = 2
  density = 1
  expand = 3
  formula = K
  name = G4_K
  specific = 4
FEATURE [App::DocumentObjectGroupPython] Ca_element014  label="Ca_element : 007"  # scripted group (container) (typed FeaturePython)
  n = 1
  ref = Ca_element
FEATURE [App::DocumentObjectGroupPython] G4_Ca  # scripted group (container) (typed FeaturePython)
  Dunit = g/cm3
  Dvalue = 1.55
  Group = -> [Ca_element014]
  conduct = 2
  density = 1
  expand = 3
  formula = Ca
  name = G4_Ca
  specific = 4
FEATURE [App::DocumentObjectGroupPython] Sc_element001  label="Sc_element : 1"  # scripted group (container) (typed FeaturePython)
  n = 1
  ref = Sc_element
FEATURE [App::DocumentObjectGroupPython] G4_Sc  # scripted group (container) (typed FeaturePython)
  Dunit = g/cm3
  Dvalue = 2.989
  Group = -> [Sc_element001]
  conduct = 2
  density = 1
  expand = 3
  formula = Sc
  name = G4_Sc
  specific = 4
FEATURE [App::DocumentObjectGroupPython] Ti_element004  label="Ti_element : 002"  # scripted group (container) (typed FeaturePython)
  n = 1
  ref = Ti_element
FEATURE [App::DocumentObjectGroupPython] G4_Ti  # scripted group (container) (typed FeaturePython)
  Dunit = g/cm3
  Dvalue = 4.54
  Group = -> [Ti_element004]
  conduct = 2
  density = 1
  expand = 3
  formula = Ti
  name = G4_Ti
  specific = 4
FEATURE [App::DocumentObjectGroupPython] V_element001  label="V_element : 1"  # scripted group (container) (typed FeaturePython)
  n = 1
  ref = V_element
FEATURE [App::DocumentObjectGroupPython] G4_V  # scripted group (container) (typed FeaturePython)
  Dunit = g/cm3
  Dvalue = 6.11
  Group = -> [V_element001]
  conduct = 2
  density = 1
  expand = 3
  formula = V
  name = G4_V
  specific = 4
FEATURE [App::DocumentObjectGroupPython] Cr_element001  label="Cr_element : 1"  # scripted group (container) (typed FeaturePython)
  n = 1
  ref = Cr_element
FEATURE [App::DocumentObjectGroupPython] G4_Cr  # scripted group (container) (typed FeaturePython)
  Dunit = g/cm3
  Dvalue = 7.18
  Group = -> [Cr_element001]
  conduct = 2
  density = 1
  expand = 3
  formula = Cr
  name = G4_Cr
  specific = 4
FEATURE [App::DocumentObjectGroupPython] Mn_element001  label="Mn_element : 1"  # scripted group (container) (typed FeaturePython)
  n = 1
  ref = Mn_element
FEATURE [App::DocumentObjectGroupPython] G4_Mn  # scripted group (container) (typed FeaturePython)
  Dunit = g/cm3
  Dvalue = 7.44
  Group = -> [Mn_element001]
  conduct = 2
  density = 1
  expand = 3
  formula = Mn
  name = G4_Mn
  specific = 4
FEATURE [App::DocumentObjectGroupPython] Fe_element007  label="Fe_element : 004"  # scripted group (container) (typed FeaturePython)
  n = 1
  ref = Fe_element
FEATURE [App::DocumentObjectGroupPython] G4_Fe  # scripted group (container) (typed FeaturePython)
  Dunit = g/cm3
  Dvalue = 7.874
  Group = -> [Fe_element007]
  conduct = 2
  density = 1
  expand = 3
  formula = Fe
  name = G4_Fe
  specific = 4
FEATURE [App::DocumentObjectGroupPython] Co_element001  label="Co_element : 1"  # scripted group (container) (typed FeaturePython)
  n = 1
  ref = Co_element
FEATURE [App::DocumentObjectGroupPython] G4_Co  # scripted group (container) (typed FeaturePython)
  Dunit = g/cm3
  Dvalue = 8.9
  Group = -> [Co_element001]
  conduct = 2
  density = 1
  expand = 3
  formula = Co
  name = G4_Co
  specific = 4
FEATURE [App::DocumentObjectGroupPython] Ni_element001  label="Ni_element : 1"  # scripted group (container) (typed FeaturePython)
  n = 1
  ref = Ni_element
FEATURE [App::DocumentObjectGroupPython] G4_Ni  # scripted group (container) (typed FeaturePython)
  Dunit = g/cm3
  Dvalue = 8.902
  Group = -> [Ni_element001]
  conduct = 2
  density = 1
  expand = 3
  formula = Ni
  name = G4_Ni
  specific = 4
FEATURE [App::DocumentObjectGroupPython] Cu_element001  label="Cu_element : 1"  # scripted group (container) (typed FeaturePython)
  n = 1
  ref = Cu_element
FEATURE [App::DocumentObjectGroupPython] G4_Cu  # scripted group (container) (typed FeaturePython)
  Dunit = g/cm3
  Dvalue = 8.96
  Group = -> [Cu_element001]
  conduct = 2
  density = 1
  expand = 3
  formula = Cu
  name = G4_Cu
  specific = 4
FEATURE [App::DocumentObjectGroupPython] Zn_element001  label="Zn_element : 1"  # scripted group (container) (typed FeaturePython)
  n = 1
  ref = Zn_element
FEATURE [App::DocumentObjectGroupPython] G4_Zn  # scripted group (container) (typed FeaturePython)
  Dunit = g/cm3
  Dvalue = 7.133
  Group = -> [Zn_element001]
  conduct = 2
  density = 1
  expand = 3
  formula = Zn
  name = G4_Zn
  specific = 4
FEATURE [App::DocumentObjectGroupPython] Ga_element002  label="Ga_element : 002"  # scripted group (container) (typed FeaturePython)
  n = 1
  ref = Ga_element
FEATURE [App::DocumentObjectGroupPython] G4_Ga  # scripted group (container) (typed FeaturePython)
  Dunit = g/cm3
  Dvalue = 5.904
  Group = -> [Ga_element002]
  conduct = 2
  density = 1
  expand = 3
  formula = Ga
  name = G4_Ga
  specific = 4
FEATURE [App::DocumentObjectGroupPython] Ge_element002  label="Ge_element : 1"  # scripted group (container) (typed FeaturePython)
  n = 1
  ref = Ge_element
FEATURE [App::DocumentObjectGroupPython] G4_Ge  # scripted group (container) (typed FeaturePython)
  Dunit = g/cm3
  Dvalue = 5.323
  Group = -> [Ge_element002]
  conduct = 2
  density = 1
  expand = 3
  formula = Ge
  name = G4_Ge
  specific = 4
FEATURE [App::DocumentObjectGroupPython] As_element003  label="As_element : 002"  # scripted group (container) (typed FeaturePython)
  n = 1
  ref = As_element
FEATURE [App::DocumentObjectGroupPython] G4_As  # scripted group (container) (typed FeaturePython)
  Dunit = g/cm3
  Dvalue = 5.73
  Group = -> [As_element003]
  conduct = 2
  density = 1
  expand = 3
  formula = As
  name = G4_As
  specific = 4
FEATURE [App::DocumentObjectGroupPython] Se_element001  label="Se_element : 1"  # scripted group (container) (typed FeaturePython)
  n = 1
  ref = Se_element
FEATURE [App::DocumentObjectGroupPython] G4_Se  # scripted group (container) (typed FeaturePython)
  Dunit = g/cm3
  Dvalue = 4.5
  Group = -> [Se_element001]
  conduct = 2
  density = 1
  expand = 3
  formula = Se
  name = G4_Se
  specific = 4
FEATURE [App::DocumentObjectGroupPython] Br_element007  label="Br_element : 004"  # scripted group (container) (typed FeaturePython)
  n = 1
  ref = Br_element
FEATURE [App::DocumentObjectGroupPython] G4_Br  # scripted group (container) (typed FeaturePython)
  Dunit = g/cm3
  Dvalue = 0.0070721
  Group = -> [Br_element007]
  conduct = 2
  density = 1
  expand = 3
  formula = Br
  name = G4_Br
  specific = 4
FEATURE [App::DocumentObjectGroupPython] Kr_element001  label="Kr_element : 1"  # scripted group (container) (typed FeaturePython)
  n = 1
  ref = Kr_element
FEATURE [App::DocumentObjectGroupPython] G4_Kr  # scripted group (container) (typed FeaturePython)
  Dunit = g/cm3
  Dvalue = 0.00347832
  Group = -> [Kr_element001]
  conduct = 2
  density = 1
  expand = 3
  formula = Kr
  name = G4_Kr
  specific = 4
FEATURE [App::DocumentObjectGroupPython] Rb_element001  label="Rb_element : 1"  # scripted group (container) (typed FeaturePython)
  n = 1
  ref = Rb_element
FEATURE [App::DocumentObjectGroupPython] G4_Rb  # scripted group (container) (typed FeaturePython)
  Dunit = g/cm3
  Dvalue = 1.532
  Group = -> [Rb_element001]
  conduct = 2
  density = 1
  expand = 3
  formula = Rb
  name = G4_Rb
  specific = 4
FEATURE [App::DocumentObjectGroupPython] Sr_element001  label="Sr_element : 1"  # scripted group (container) (typed FeaturePython)
  n = 1
  ref = Sr_element
FEATURE [App::DocumentObjectGroupPython] G4_Sr  # scripted group (container) (typed FeaturePython)
  Dunit = g/cm3
  Dvalue = 2.54
  Group = -> [Sr_element001]
  conduct = 2
  density = 1
  expand = 3
  formula = Sr
  name = G4_Sr
  specific = 4
FEATURE [App::DocumentObjectGroupPython] Y_element001  label="Y_element : 1"  # scripted group (container) (typed FeaturePython)
  n = 1
  ref = Y_element
FEATURE [App::DocumentObjectGroupPython] G4_Y  # scripted group (container) (typed FeaturePython)
  Dunit = g/cm3
  Dvalue = 4.469
  Group = -> [Y_element001]
  conduct = 2
  density = 1
  expand = 3
  formula = Y
  name = G4_Y
  specific = 4
FEATURE [App::DocumentObjectGroupPython] Zr_element001  label="Zr_element : 1"  # scripted group (container) (typed FeaturePython)
  n = 1
  ref = Zr_element
FEATURE [App::DocumentObjectGroupPython] G4_Zr  # scripted group (container) (typed FeaturePython)
  Dunit = g/cm3
  Dvalue = 6.506
  Group = -> [Zr_element001]
  conduct = 2
  density = 1
  expand = 3
  formula = Zr
  name = G4_Zr
  specific = 4
FEATURE [App::DocumentObjectGroupPython] Nb_element001  label="Nb_element : 1"  # scripted group (container) (typed FeaturePython)
  n = 1
  ref = Nb_element
FEATURE [App::DocumentObjectGroupPython] G4_Nb  # scripted group (container) (typed FeaturePython)
  Dunit = g/cm3
  Dvalue = 8.57
  Group = -> [Nb_element001]
  conduct = 2
  density = 1
  expand = 3
  formula = Nb
  name = G4_Nb
  specific = 4
FEATURE [App::DocumentObjectGroupPython] Mo_element001  label="Mo_element : 1"  # scripted group (container) (typed FeaturePython)
  n = 1
  ref = Mo_element
FEATURE [App::DocumentObjectGroupPython] G4_Mo  # scripted group (container) (typed FeaturePython)
  Dunit = g/cm3
  Dvalue = 10.22
  Group = -> [Mo_element001]
  conduct = 2
  density = 1
  expand = 3
  formula = Mo
  name = G4_Mo
  specific = 4
FEATURE [App::DocumentObjectGroupPython] Tc_element001  label="Tc_element : 1"  # scripted group (container) (typed FeaturePython)
  n = 1
  ref = Tc_element
FEATURE [App::DocumentObjectGroupPython] G4_Tc  # scripted group (container) (typed FeaturePython)
  Dunit = g/cm3
  Dvalue = 11.5
  Group = -> [Tc_element001]
  conduct = 2
  density = 1
  expand = 3
  formula = Tc
  name = G4_Tc
  specific = 4
FEATURE [App::DocumentObjectGroupPython] Ru_element001  label="Ru_element : 1"  # scripted group (container) (typed FeaturePython)
  n = 1
  ref = Ru_element
FEATURE [App::DocumentObjectGroupPython] G4_Ru  # scripted group (container) (typed FeaturePython)
  Dunit = g/cm3
  Dvalue = 12.41
  Group = -> [Ru_element001]
  conduct = 2
  density = 1
  expand = 3
  formula = Ru
  name = G4_Ru
  specific = 4
FEATURE [App::DocumentObjectGroupPython] Rh_element001  label="Rh_element : 1"  # scripted group (container) (typed FeaturePython)
  n = 1
  ref = Rh_element
FEATURE [App::DocumentObjectGroupPython] G4_Rh  # scripted group (container) (typed FeaturePython)
  Dunit = g/cm3
  Dvalue = 12.41
  Group = -> [Rh_element001]
  conduct = 2
  density = 1
  expand = 3
  formula = Rh
  name = G4_Rh
  specific = 4
FEATURE [App::DocumentObjectGroupPython] Pd_element001  label="Pd_element : 1"  # scripted group (container) (typed FeaturePython)
  n = 1
  ref = Pd_element
FEATURE [App::DocumentObjectGroupPython] G4_Pd  # scripted group (container) (typed FeaturePython)
  Dunit = g/cm3
  Dvalue = 12.02
  Group = -> [Pd_element001]
  conduct = 2
  density = 1
  expand = 3
  formula = Pd
  name = G4_Pd
  specific = 4
FEATURE [App::DocumentObjectGroupPython] Ag_element006  label="Ag_element : 004"  # scripted group (container) (typed FeaturePython)
  n = 1
  ref = Ag_element
FEATURE [App::DocumentObjectGroupPython] G4_Ag  # scripted group (container) (typed FeaturePython)
  Dunit = g/cm3
  Dvalue = 10.5
  Group = -> [Ag_element006]
  conduct = 2
  density = 1
  expand = 3
  formula = Ag
  name = G4_Ag
  specific = 4
FEATURE [App::DocumentObjectGroupPython] Cd_element003  label="Cd_element : 003"  # scripted group (container) (typed FeaturePython)
  n = 1
  ref = Cd_element
FEATURE [App::DocumentObjectGroupPython] G4_Cd  # scripted group (container) (typed FeaturePython)
  Dunit = g/cm3
  Dvalue = 8.65
  Group = -> [Cd_element003]
  conduct = 2
  density = 1
  expand = 3
  formula = Cd
  name = G4_Cd
  specific = 4
FEATURE [App::DocumentObjectGroupPython] In_element001  label="In_element : 1"  # scripted group (container) (typed FeaturePython)
  n = 1
  ref = In_element
FEATURE [App::DocumentObjectGroupPython] G4_In  # scripted group (container) (typed FeaturePython)
  Dunit = g/cm3
  Dvalue = 7.31
  Group = -> [In_element001]
  conduct = 2
  density = 1
  expand = 3
  formula = In
  name = G4_In
  specific = 4
FEATURE [App::DocumentObjectGroupPython] Sn_element001  label="Sn_element : 1"  # scripted group (container) (typed FeaturePython)
  n = 1
  ref = Sn_element
FEATURE [App::DocumentObjectGroupPython] G4_Sn  # scripted group (container) (typed FeaturePython)
  Dunit = g/cm3
  Dvalue = 7.31
  Group = -> [Sn_element001]
  conduct = 2
  density = 1
  expand = 3
  formula = Sn
  name = G4_Sn
  specific = 4
FEATURE [App::DocumentObjectGroupPython] Sb_element001  label="Sb_element : 1"  # scripted group (container) (typed FeaturePython)
  n = 1
  ref = Sb_element
FEATURE [App::DocumentObjectGroupPython] G4_Sb  # scripted group (container) (typed FeaturePython)
  Dunit = g/cm3
  Dvalue = 6.691
  Group = -> [Sb_element001]
  conduct = 2
  density = 1
  expand = 3
  formula = Sb
  name = G4_Sb
  specific = 4
FEATURE [App::DocumentObjectGroupPython] Te_element002  label="Te_element : 002"  # scripted group (container) (typed FeaturePython)
  n = 1
  ref = Te_element
FEATURE [App::DocumentObjectGroupPython] G4_Te  # scripted group (container) (typed FeaturePython)
  Dunit = g/cm3
  Dvalue = 6.24
  Group = -> [Te_element002]
  conduct = 2
  density = 1
  expand = 3
  formula = Te
  name = G4_Te
  specific = 4
FEATURE [App::DocumentObjectGroupPython] I_element010  label="I_element : 006"  # scripted group (container) (typed FeaturePython)
  n = 1
  ref = I_element
FEATURE [App::DocumentObjectGroupPython] G4_I  # scripted group (container) (typed FeaturePython)
  Dunit = g/cm3
  Dvalue = 4.93
  Group = -> [I_element010]
  conduct = 2
  density = 1
  expand = 3
  formula = I
  name = G4_I
  specific = 4
FEATURE [App::DocumentObjectGroupPython] Xe_element001  label="Xe_element : 1"  # scripted group (container) (typed FeaturePython)
  n = 1
  ref = Xe_element
FEATURE [App::DocumentObjectGroupPython] G4_Xe  # scripted group (container) (typed FeaturePython)
  Dunit = g/cm3
  Dvalue = 0.00548536
  Group = -> [Xe_element001]
  conduct = 2
  density = 1
  expand = 3
  formula = Xe
  name = G4_Xe
  specific = 4
FEATURE [App::DocumentObjectGroupPython] Cs_element003  label="Cs_element : 003"  # scripted group (container) (typed FeaturePython)
  n = 1
  ref = Cs_element
FEATURE [App::DocumentObjectGroupPython] G4_Cs  # scripted group (container) (typed FeaturePython)
  Dunit = g/cm3
  Dvalue = 1.873
  Group = -> [Cs_element003]
  conduct = 2
  density = 1
  expand = 3
  formula = Cs
  name = G4_Cs
  specific = 4
FEATURE [App::DocumentObjectGroupPython] Ba_element003  label="Ba_element : 003"  # scripted group (container) (typed FeaturePython)
  n = 1
  ref = Ba_element
FEATURE [App::DocumentObjectGroupPython] G4_Ba  # scripted group (container) (typed FeaturePython)
  Dunit = g/cm3
  Dvalue = 3.5
  Group = -> [Ba_element003]
  conduct = 2
  density = 1
  expand = 3
  formula = Ba
  name = G4_Ba
  specific = 4
FEATURE [App::DocumentObjectGroupPython] La_element003  label="La_element : 003"  # scripted group (container) (typed FeaturePython)
  n = 1
  ref = La_element
FEATURE [App::DocumentObjectGroupPython] G4_La  # scripted group (container) (typed FeaturePython)
  Dunit = g/cm3
  Dvalue = 6.154
  Group = -> [La_element003]
  conduct = 2
  density = 1
  expand = 3
  formula = La
  name = G4_La
  specific = 4
FEATURE [App::DocumentObjectGroupPython] Ce_element002  label="Ce_element : 1"  # scripted group (container) (typed FeaturePython)
  n = 1
  ref = Ce_element
FEATURE [App::DocumentObjectGroupPython] G4_Ce  # scripted group (container) (typed FeaturePython)
  Dunit = g/cm3
  Dvalue = 6.657
  Group = -> [Ce_element002]
  conduct = 2
  density = 1
  expand = 3
  formula = Ce
  name = G4_Ce
  specific = 4
FEATURE [App::DocumentObjectGroupPython] Pr_element001  label="Pr_element : 1"  # scripted group (container) (typed FeaturePython)
  n = 1
  ref = Pr_element
FEATURE [App::DocumentObjectGroupPython] G4_Pr  # scripted group (container) (typed FeaturePython)
  Dunit = g/cm3
  Dvalue = 6.71
  Group = -> [Pr_element001]
  conduct = 2
  density = 1
  expand = 3
  formula = Pr
  name = G4_Pr
  specific = 4
FEATURE [App::DocumentObjectGroupPython] Nd_element001  label="Nd_element : 1"  # scripted group (container) (typed FeaturePython)
  n = 1
  ref = Nd_element
FEATURE [App::DocumentObjectGroupPython] G4_Nd  # scripted group (container) (typed FeaturePython)
  Dunit = g/cm3
  Dvalue = 6.9
  Group = -> [Nd_element001]
  conduct = 2
  density = 1
  expand = 3
  formula = Nd
  name = G4_Nd
  specific = 4
FEATURE [App::DocumentObjectGroupPython] Pm_element001  label="Pm_element : 1"  # scripted group (container) (typed FeaturePython)
  n = 1
  ref = Pm_element
FEATURE [App::DocumentObjectGroupPython] G4_Pm  # scripted group (container) (typed FeaturePython)
  Dunit = g/cm3
  Dvalue = 7.22
  Group = -> [Pm_element001]
  conduct = 2
  density = 1
  expand = 3
  formula = Pm
  name = G4_Pm
  specific = 4
FEATURE [App::DocumentObjectGroupPython] Sm_element001  label="Sm_element : 1"  # scripted group (container) (typed FeaturePython)
  n = 1
  ref = Sm_element
FEATURE [App::DocumentObjectGroupPython] G4_Sm  # scripted group (container) (typed FeaturePython)
  Dunit = g/cm3
  Dvalue = 7.46
  Group = -> [Sm_element001]
  conduct = 2
  density = 1
  expand = 3
  formula = Sm
  name = G4_Sm
  specific = 4
FEATURE [App::DocumentObjectGroupPython] Eu_element001  label="Eu_element : 1"  # scripted group (container) (typed FeaturePython)
  n = 1
  ref = Eu_element
FEATURE [App::DocumentObjectGroupPython] G4_Eu  # scripted group (container) (typed FeaturePython)
  Dunit = g/cm3
  Dvalue = 5.243
  Group = -> [Eu_element001]
  conduct = 2
  density = 1
  expand = 3
  formula = Eu
  name = G4_Eu
  specific = 4
FEATURE [App::DocumentObjectGroupPython] Gd_element002  label="Gd_element : 1"  # scripted group (container) (typed FeaturePython)
  n = 1
  ref = Gd_element
FEATURE [App::DocumentObjectGroupPython] G4_Gd  # scripted group (container) (typed FeaturePython)
  Dunit = g/cm3
  Dvalue = 7.9004
  Group = -> [Gd_element002]
  conduct = 2
  density = 1
  expand = 3
  formula = Gd
  name = G4_Gd
  specific = 4
FEATURE [App::DocumentObjectGroupPython] Tb_element001  label="Tb_element : 1"  # scripted group (container) (typed FeaturePython)
  n = 1
  ref = Tb_element
FEATURE [App::DocumentObjectGroupPython] G4_Tb  # scripted group (container) (typed FeaturePython)
  Dunit = g/cm3
  Dvalue = 8.229
  Group = -> [Tb_element001]
  conduct = 2
  density = 1
  expand = 3
  formula = Tb
  name = G4_Tb
  specific = 4
FEATURE [App::DocumentObjectGroupPython] Dy_element001  label="Dy_element : 1"  # scripted group (container) (typed FeaturePython)
  n = 1
  ref = Dy_element
FEATURE [App::DocumentObjectGroupPython] G4_Dy  # scripted group (container) (typed FeaturePython)
  Dunit = g/cm3
  Dvalue = 8.55
  Group = -> [Dy_element001]
  conduct = 2
  density = 1
  expand = 3
  formula = Dy
  name = G4_Dy
  specific = 4
FEATURE [App::DocumentObjectGroupPython] Ho_element001  label="Ho_element : 1"  # scripted group (container) (typed FeaturePython)
  n = 1
  ref = Ho_element
FEATURE [App::DocumentObjectGroupPython] G4_Ho  # scripted group (container) (typed FeaturePython)
  Dunit = g/cm3
  Dvalue = 8.795
  Group = -> [Ho_element001]
  conduct = 2
  density = 1
  expand = 3
  formula = Ho
  name = G4_Ho
  specific = 4
FEATURE [App::DocumentObjectGroupPython] Er_element001  label="Er_element : 1"  # scripted group (container) (typed FeaturePython)
  n = 1
  ref = Er_element
FEATURE [App::DocumentObjectGroupPython] G4_Er  # scripted group (container) (typed FeaturePython)
  Dunit = g/cm3
  Dvalue = 9.066
  Group = -> [Er_element001]
  conduct = 2
  density = 1
  expand = 3
  formula = Er
  name = G4_Er
  specific = 4
FEATURE [App::DocumentObjectGroupPython] Tm_element001  label="Tm_element : 1"  # scripted group (container) (typed FeaturePython)
  n = 1
  ref = Tm_element
FEATURE [App::DocumentObjectGroupPython] G4_Tm  # scripted group (container) (typed FeaturePython)
  Dunit = g/cm3
  Dvalue = 9.321
  Group = -> [Tm_element001]
  conduct = 2
  density = 1
  expand = 3
  formula = Tm
  name = G4_Tm
  specific = 4
FEATURE [App::DocumentObjectGroupPython] Yb_element001  label="Yb_element : 1"  # scripted group (container) (typed FeaturePython)
  n = 1
  ref = Yb_element
FEATURE [App::DocumentObjectGroupPython] G4_Yb  # scripted group (container) (typed FeaturePython)
  Dunit = g/cm3
  Dvalue = 6.73
  Group = -> [Yb_element001]
  conduct = 2
  density = 1
  expand = 3
  formula = Yb
  name = G4_Yb
  specific = 4
FEATURE [App::DocumentObjectGroupPython] Lu_element001  label="Lu_element : 1"  # scripted group (container) (typed FeaturePython)
  n = 1
  ref = Lu_element
FEATURE [App::DocumentObjectGroupPython] G4_Lu  # scripted group (container) (typed FeaturePython)
  Dunit = g/cm3
  Dvalue = 9.84
  Group = -> [Lu_element001]
  conduct = 2
  density = 1
  expand = 3
  formula = Lu
  name = G4_Lu
  specific = 4
FEATURE [App::DocumentObjectGroupPython] Hf_element001  label="Hf_element : 1"  # scripted group (container) (typed FeaturePython)
  n = 1
  ref = Hf_element
FEATURE [App::DocumentObjectGroupPython] G4_Hf  # scripted group (container) (typed FeaturePython)
  Dunit = g/cm3
  Dvalue = 13.31
  Group = -> [Hf_element001]
  conduct = 2
  density = 1
  expand = 3
  formula = Hf
  name = G4_Hf
  specific = 4
FEATURE [App::DocumentObjectGroupPython] Ta_element001  label="Ta_element : 1"  # scripted group (container) (typed FeaturePython)
  n = 1
  ref = Ta_element
FEATURE [App::DocumentObjectGroupPython] G4_Ta  # scripted group (container) (typed FeaturePython)
  Dunit = g/cm3
  Dvalue = 16.654
  Group = -> [Ta_element001]
  conduct = 2
  density = 1
  expand = 3
  formula = Ta
  name = G4_Ta
  specific = 4
FEATURE [App::DocumentObjectGroupPython] W_element004  label="W_element : 004"  # scripted group (container) (typed FeaturePython)
  n = 1
  ref = W_element
FEATURE [App::DocumentObjectGroupPython] G4_W  # scripted group (container) (typed FeaturePython)
  Dunit = g/cm3
  Dvalue = 19.3
  Group = -> [W_element004]
  conduct = 2
  density = 1
  expand = 3
  formula = W
  name = G4_W
  specific = 4
FEATURE [App::DocumentObjectGroupPython] Re_element001  label="Re_element : 1"  # scripted group (container) (typed FeaturePython)
  n = 1
  ref = Re_element
FEATURE [App::DocumentObjectGroupPython] G4_Re  # scripted group (container) (typed FeaturePython)
  Dunit = g/cm3
  Dvalue = 21.02
  Group = -> [Re_element001]
  conduct = 2
  density = 1
  expand = 3
  formula = Re
  name = G4_Re
  specific = 4
FEATURE [App::DocumentObjectGroupPython] Os_element001  label="Os_element : 1"  # scripted group (container) (typed FeaturePython)
  n = 1
  ref = Os_element
FEATURE [App::DocumentObjectGroupPython] G4_Os  # scripted group (container) (typed FeaturePython)
  Dunit = g/cm3
  Dvalue = 22.57
  Group = -> [Os_element001]
  conduct = 2
  density = 1
  expand = 3
  formula = Os
  name = G4_Os
  specific = 4
FEATURE [App::DocumentObjectGroupPython] Ir_element001  label="Ir_element : 1"  # scripted group (container) (typed FeaturePython)
  n = 1
  ref = Ir_element
FEATURE [App::DocumentObjectGroupPython] G4_Ir  # scripted group (container) (typed FeaturePython)
  Dunit = g/cm3
  Dvalue = 22.42
  Group = -> [Ir_element001]
  conduct = 2
  density = 1
  expand = 3
  formula = Ir
  name = G4_Ir
  specific = 4
FEATURE [App::DocumentObjectGroupPython] Pt_element001  label="Pt_element : 1"  # scripted group (container) (typed FeaturePython)
  n = 1
  ref = Pt_element
FEATURE [App::DocumentObjectGroupPython] G4_Pt  # scripted group (container) (typed FeaturePython)
  Dunit = g/cm3
  Dvalue = 21.45
  Group = -> [Pt_element001]
  conduct = 2
  density = 1
  expand = 3
  formula = Pt
  name = G4_Pt
  specific = 4
FEATURE [App::DocumentObjectGroupPython] Au_element001  label="Au_element : 1"  # scripted group (container) (typed FeaturePython)
  n = 1
  ref = Au_element
FEATURE [App::DocumentObjectGroupPython] G4_Au  # scripted group (container) (typed FeaturePython)
  Dunit = g/cm3
  Dvalue = 19.32
  Group = -> [Au_element001]
  conduct = 2
  density = 1
  expand = 3
  formula = Au
  name = G4_Au
  specific = 4
FEATURE [App::DocumentObjectGroupPython] Hg_element002  label="Hg_element : 002"  # scripted group (container) (typed FeaturePython)
  n = 1
  ref = Hg_element
FEATURE [App::DocumentObjectGroupPython] G4_Hg  # scripted group (container) (typed FeaturePython)
  Dunit = g/cm3
  Dvalue = 13.546
  Group = -> [Hg_element002]
  conduct = 2
  density = 1
  expand = 3
  formula = Hg
  name = G4_Hg
  specific = 4
FEATURE [App::DocumentObjectGroupPython] Tl_element002  label="Tl_element : 002"  # scripted group (container) (typed FeaturePython)
  n = 1
  ref = Tl_element
FEATURE [App::DocumentObjectGroupPython] G4_Tl  # scripted group (container) (typed FeaturePython)
  Dunit = g/cm3
  Dvalue = 11.72
  Group = -> [Tl_element002]
  conduct = 2
  density = 1
  expand = 3
  formula = Tl
  name = G4_Tl
  specific = 4
FEATURE [App::DocumentObjectGroupPython] Pb_element003  label="Pb_element : 1"  # scripted group (container) (typed FeaturePython)
  n = 1
  ref = Pb_element
FEATURE [App::DocumentObjectGroupPython] G4_Pb  # scripted group (container) (typed FeaturePython)
  Dunit = g/cm3
  Dvalue = 11.35
  Group = -> [Pb_element003]
  conduct = 2
  density = 1
  expand = 3
  formula = Pb
  name = G4_Pb
  specific = 4
FEATURE [App::DocumentObjectGroupPython] Bi_element002  label="Bi_element : 1"  # scripted group (container) (typed FeaturePython)
  n = 1
  ref = Bi_element
FEATURE [App::DocumentObjectGroupPython] G4_Bi  # scripted group (container) (typed FeaturePython)
  Dunit = g/cm3
  Dvalue = 9.747
  Group = -> [Bi_element002]
  conduct = 2
  density = 1
  expand = 3
  formula = Bi
  name = G4_Bi
  specific = 4
FEATURE [App::DocumentObjectGroupPython] Po_element001  label="Po_element : 1"  # scripted group (container) (typed FeaturePython)
  n = 1
  ref = Po_element
FEATURE [App::DocumentObjectGroupPython] G4_Po  # scripted group (container) (typed FeaturePython)
  Dunit = g/cm3
  Dvalue = 9.32
  Group = -> [Po_element001]
  conduct = 2
  density = 1
  expand = 3
  formula = Po
  name = G4_Po
  specific = 4
FEATURE [App::DocumentObjectGroupPython] At_element001  label="At_element : 1"  # scripted group (container) (typed FeaturePython)
  n = 1
  ref = At_element
FEATURE [App::DocumentObjectGroupPython] G4_At  # scripted group (container) (typed FeaturePython)
  Dunit = g/cm3
  Dvalue = 9.32
  Group = -> [At_element001]
  conduct = 2
  density = 1
  expand = 3
  formula = At
  name = G4_At
  specific = 4
FEATURE [App::DocumentObjectGroupPython] Rn_element001  label="Rn_element : 1"  # scripted group (container) (typed FeaturePython)
  n = 1
  ref = Rn_element
FEATURE [App::DocumentObjectGroupPython] G4_Rn  # scripted group (container) (typed FeaturePython)
  Dunit = g/cm3
  Dvalue = 0.00900662
  Group = -> [Rn_element001]
  conduct = 2
  density = 1
  expand = 3
  formula = Rn
  name = G4_Rn
  specific = 4
FEATURE [App::DocumentObjectGroupPython] Fr_element001  label="Fr_element : 1"  # scripted group (container) (typed FeaturePython)
  n = 1
  ref = Fr_element
FEATURE [App::DocumentObjectGroupPython] G4_Fr  # scripted group (container) (typed FeaturePython)
  Dunit = g/cm3
  Dvalue = 1
  Group = -> [Fr_element001]
  conduct = 2
  density = 1
  expand = 3
  formula = Fr
  name = G4_Fr
  specific = 4
FEATURE [App::DocumentObjectGroupPython] Ra_element001  label="Ra_element : 1"  # scripted group (container) (typed FeaturePython)
  n = 1
  ref = Ra_element
FEATURE [App::DocumentObjectGroupPython] G4_Ra  # scripted group (container) (typed FeaturePython)
  Dunit = g/cm3
  Dvalue = 5
  Group = -> [Ra_element001]
  conduct = 2
  density = 1
  expand = 3
  formula = Ra
  name = G4_Ra
  specific = 4
FEATURE [App::DocumentObjectGroupPython] Ac_element001  label="Ac_element : 1"  # scripted group (container) (typed FeaturePython)
  n = 1
  ref = Ac_element
FEATURE [App::DocumentObjectGroupPython] G4_Ac  # scripted group (container) (typed FeaturePython)
  Dunit = g/cm3
  Dvalue = 10.07
  Group = -> [Ac_element001]
  conduct = 2
  density = 1
  expand = 3
  formula = Ac
  name = G4_Ac
  specific = 4
FEATURE [App::DocumentObjectGroupPython] Th_element001  label="Th_element : 1"  # scripted group (container) (typed FeaturePython)
  n = 1
  ref = Th_element
FEATURE [App::DocumentObjectGroupPython] G4_Th  # scripted group (container) (typed FeaturePython)
  Dunit = g/cm3
  Dvalue = 11.72
  Group = -> [Th_element001]
  conduct = 2
  density = 1
  expand = 3
  formula = Th
  name = G4_Th
  specific = 4
FEATURE [App::DocumentObjectGroupPython] Pa_element001  label="Pa_element : 1"  # scripted group (container) (typed FeaturePython)
  n = 1
  ref = Pa_element
FEATURE [App::DocumentObjectGroupPython] G4_Pa  # scripted group (container) (typed FeaturePython)
  Dunit = g/cm3
  Dvalue = 15.37
  Group = -> [Pa_element001]
  conduct = 2
  density = 1
  expand = 3
  formula = Pa
  name = G4_Pa
  specific = 4
FEATURE [App::DocumentObjectGroupPython] U_element004  label="U_element : 004"  # scripted group (container) (typed FeaturePython)
  n = 1
  ref = U_element
FEATURE [App::DocumentObjectGroupPython] G4_U  # scripted group (container) (typed FeaturePython)
  Dunit = g/cm3
  Dvalue = 18.95
  Group = -> [U_element004]
  conduct = 2
  density = 1
  expand = 3
  formula = U
  name = G4_U
  specific = 4
FEATURE [App::DocumentObjectGroupPython] Np_element001  label="Np_element : 1"  # scripted group (container) (typed FeaturePython)
  n = 1
  ref = Np_element
FEATURE [App::DocumentObjectGroupPython] G4_Np  # scripted group (container) (typed FeaturePython)
  Dunit = g/cm3
  Dvalue = 20.25
  Group = -> [Np_element001]
  conduct = 2
  density = 1
  expand = 3
  formula = Np
  name = G4_Np
  specific = 4
FEATURE [App::DocumentObjectGroupPython] Pu_element002  label="Pu_element : 002"  # scripted group (container) (typed FeaturePython)
  n = 1
  ref = Pu_element
FEATURE [App::DocumentObjectGroupPython] G4_Pu  # scripted group (container) (typed FeaturePython)
  Dunit = g/cm3
  Dvalue = 19.84
  Group = -> [Pu_element002]
  conduct = 2
  density = 1
  expand = 3
  formula = Pu
  name = G4_Pu
  specific = 4
FEATURE [App::DocumentObjectGroupPython] Am_element001  label="Am_element : 1"  # scripted group (container) (typed FeaturePython)
  n = 1
  ref = Am_element
FEATURE [App::DocumentObjectGroupPython] G4_Am  # scripted group (container) (typed FeaturePython)
  Dunit = g/cm3
  Dvalue = 13.67
  Group = -> [Am_element001]
  conduct = 2
  density = 1
  expand = 3
  formula = Am
  name = G4_Am
  specific = 4
FEATURE [App::DocumentObjectGroupPython] Cm_element001  label="Cm_element : 1"  # scripted group (container) (typed FeaturePython)
  n = 1
  ref = Cm_element
FEATURE [App::DocumentObjectGroupPython] G4_Cm  # scripted group (container) (typed FeaturePython)
  Dunit = g/cm3
  Dvalue = 13.51
  Group = -> [Cm_element001]
  conduct = 2
  density = 1
  expand = 3
  formula = Cm
  name = G4_Cm
  specific = 4
FEATURE [App::DocumentObjectGroupPython] Bk_element001  label="Bk_element : 1"  # scripted group (container) (typed FeaturePython)
  n = 1
  ref = Bk_element
FEATURE [App::DocumentObjectGroupPython] G4_Bk  # scripted group (container) (typed FeaturePython)
  Dunit = g/cm3
  Dvalue = 14
  Group = -> [Bk_element001]
  conduct = 2
  density = 1
  expand = 3
  formula = Bk
  name = G4_Bk
  specific = 4
FEATURE [App::DocumentObjectGroupPython] Cf_element001  label="Cf_element : 1"  # scripted group (container) (typed FeaturePython)
  n = 1
  ref = Cf_element
FEATURE [App::DocumentObjectGroupPython] G4_Cf  # scripted group (container) (typed FeaturePython)
  Dunit = g/cm3
  Dvalue = 10
  Group = -> [Cf_element001]
  conduct = 2
  density = 1
  expand = 3
  formula = Cf
  name = G4_Cf
  specific = 4
FEATURE [App::DocumentObjectGroupPython] Element  # scripted group (container) (typed FeaturePython)
  Group = -> [G4_H,G4_He,G4_Li,G4_Be,G4_B,G4_C,G4_N,G4_O,G4_F,G4_Ne,G4_Na,G4_Mg,G4_Al,G4_Si,G4_P,G4_S,G4_Cl,G4_Ar,G4_K,G4_Ca,G4_Sc,G4_Ti,G4_V,G4_Cr,G4_Mn,G4_Fe,G4_Co,G4_Ni,G4_Cu,G4_Zn,G4_Ga,G4_Ge,G4_As,G4_Se,G4_Br,G4_Kr,G4_Rb,G4_Sr,G4_Y,G4_Zr,G4_Nb,G4_Mo,G4_Tc,G4_Ru,G4_Rh,G4_Pd,G4_Ag,G4_Cd,G4_In,G4_Sn,G4_Sb,G4_Te,G4_I,G4_Xe,G4_Cs,G4_Ba,G4_La,G4_Ce,G4_Pr,G4_Nd,G4_Pm,G4_Sm,G4_Eu,G4_Gd,G4_Tb,G4_Dy,G4_Ho,G4_Er,+30 more]
FEATURE [App::DocumentObjectGroupPython] H_element114  label="H_element : 063"  # scripted group (container) (typed FeaturePython)
  n = 2
  ref = H_element
FEATURE [App::DocumentObjectGroupPython] G4_lH2  # scripted group (container) (typed FeaturePython)
  Dunit = g/cm3
  Dvalue = 0.0708
  Group = -> [H_element114]
  conduct = 2
  density = 1
  expand = 3
  formula = G4_lH2
  name = G4_lH2
  specific = 4
FEATURE [App::DocumentObjectGroupPython] N_element049  label="N_element : 022"  # scripted group (container) (typed FeaturePython)
  n = 2
  ref = N_element
FEATURE [App::DocumentObjectGroupPython] G4_lN2  # scripted group (container) (typed FeaturePython)
  Dunit = g/cm3
  Dvalue = 0.807
  Group = -> [N_element049]
  conduct = 2
  density = 1
  expand = 3
  formula = G4_lN2
  name = G4_lN2
  specific = 4
FEATURE [App::DocumentObjectGroupPython] O_element106  label="O_element : 060"  # scripted group (container) (typed FeaturePython)
  n = 2
  ref = O_element
FEATURE [App::DocumentObjectGroupPython] G4_lO2  # scripted group (container) (typed FeaturePython)
  Dunit = g/cm3
  Dvalue = 1.141
  Group = -> [O_element106]
  conduct = 2
  density = 1
  expand = 3
  formula = G4_lO2
  name = G4_lO2
  specific = 4
FEATURE [App::DocumentObjectGroupPython] Ar  label="Ar : 1"  # scripted group (container) (typed FeaturePython)
  n = 1
  ref = Ar
FEATURE [App::DocumentObjectGroupPython] G4_lAr  # scripted group (container) (typed FeaturePython)
  Dunit = g/cm3
  Dvalue = 1.396
  Group = -> [Ar]
  conduct = 2
  density = 1
  expand = 3
  formula = G4_lAr
  name = G4_lAr
  specific = 4
FEATURE [App::DocumentObjectGroupPython] Br  label="Br : 1"  # scripted group (container) (typed FeaturePython)
  n = 1
  ref = Br
FEATURE [App::DocumentObjectGroupPython] G4_lBr  # scripted group (container) (typed FeaturePython)
  Dunit = g/cm3
  Dvalue = 3.1028
  Group = -> [Br]
  conduct = 2
  density = 1
  expand = 3
  formula = G4_lBr
  name = G4_lBr
  specific = 4
FEATURE [App::DocumentObjectGroupPython] Kr  label="Kr : 1"  # scripted group (container) (typed FeaturePython)
  n = 1
  ref = Kr
FEATURE [App::DocumentObjectGroupPython] G4_lKr  # scripted group (container) (typed FeaturePython)
  Dunit = g/cm3
  Dvalue = 2.418
  Group = -> [Kr]
  conduct = 2
  density = 1
  expand = 3
  formula = G4_lKr
  name = G4_lKr
  specific = 4
FEATURE [App::DocumentObjectGroupPython] Xe  label="Xe : 1"  # scripted group (container) (typed FeaturePython)
  n = 1
  ref = Xe
FEATURE [App::DocumentObjectGroupPython] G4_lXe  # scripted group (container) (typed FeaturePython)
  Dunit = g/cm3
  Dvalue = 2.953
  Group = -> [Xe]
  conduct = 2
  density = 1
  expand = 3
  formula = G4_lXe
  name = G4_lXe
  specific = 4
FEATURE [App::DocumentObjectGroupPython] O_element107  label="O_element : 061"  # scripted group (container) (typed FeaturePython)
  n = 4
  ref = O_element
FEATURE [App::DocumentObjectGroupPython] Pb_element004  label="Pb_element : 002"  # scripted group (container) (typed FeaturePython)
  n = 1
  ref = Pb_element
FEATURE [App::DocumentObjectGroupPython] W_element005  label="W_element : 005"  # scripted group (container) (typed FeaturePython)
  n = 1
  ref = W_element
FEATURE [App::DocumentObjectGroupPython] G4_PbWO4  # scripted group (container) (typed FeaturePython)
  Dunit = g/cm3
  Dvalue = 8.28
  Group = -> [O_element107,Pb_element004,W_element005]
  conduct = 2
  density = 1
  expand = 3
  formula = G4_PbWO4
  name = G4_PbWO4
  specific = 4
FEATURE [App::DocumentObjectGroupPython] alactic  label="alactic : 1"  # scripted group (container) (typed FeaturePython)
  n = 1
  ref = alactic
FEATURE [App::DocumentObjectGroupPython] G4_Galactic  # scripted group (container) (typed FeaturePython)
  Dunit = g/cm3
  Dvalue = 0
  Group = -> [alactic]
  conduct = 2
  density = 1
  expand = 3
  formula = G4_Galactic
  name = G4_Galactic
  specific = 4
FEATURE [App::DocumentObjectGroupPython] RAPHITE_POROUS  label="RAPHITE_POROUS : 1"  # scripted group (container) (typed FeaturePython)
  n = 1
  ref = RAPHITE_POROUS
FEATURE [App::DocumentObjectGroupPython] G4_GRAPHITE_POROUS  # scripted group (container) (typed FeaturePython)
  Dunit = g/cm3
  Dvalue = 1.7
  Group = -> [RAPHITE_POROUS]
  conduct = 2
  density = 1
  expand = 3
  formula = G4_GRAPHITE_POROUS
  name = G4_GRAPHITE_POROUS
  specific = 4
FEATURE [App::DocumentObjectGroupPython] H_element115  label="H_element : 0.150"  # scripted group (container) (typed FeaturePython)
  n = 0.080538
FEATURE [App::DocumentObjectGroupPython] C_element125  label="C_element : 0.600"  # scripted group (container) (typed FeaturePython)
  n = 0.599848
FEATURE [App::DocumentObjectGroupPython] O_element108  label="O_element : 0.320"  # scripted group (container) (typed FeaturePython)
  n = 0.319614
FEATURE [App::DocumentObjectGroupPython] G4_LUCITE  # scripted group (container) (typed FeaturePython)
  Dunit = g/cm3
  Dvalue = 1.19
  Group = -> [H_element115,C_element125,O_element108]
  conduct = 2
  density = 1
  expand = 3
  formula = G4_LUCITE
  name = G4_LUCITE
  specific = 4
FEATURE [App::DocumentObjectGroupPython] Cu_element002  label="Cu_element : 62"  # scripted group (container) (typed FeaturePython)
  n = 62
  ref = Cu_element
FEATURE [App::DocumentObjectGroupPython] Zn_element002  label="Zn_element : 35"  # scripted group (container) (typed FeaturePython)
  n = 35
  ref = Zn_element
FEATURE [App::DocumentObjectGroupPython] Pb_element005  label="Pb_element : 3"  # scripted group (container) (typed FeaturePython)
  n = 3
  ref = Pb_element
FEATURE [App::DocumentObjectGroupPython] G4_BRASS  # scripted group (container) (typed FeaturePython)
  Dunit = g/cm3
  Dvalue = 8.52
  Group = -> [Cu_element002,Zn_element002,Pb_element005]
  conduct = 2
  density = 1
  expand = 3
  formula = G4_BRASS
  name = G4_BRASS
  specific = 4
FEATURE [App::DocumentObjectGroupPython] Cu_element003  label="Cu_element : 89"  # scripted group (container) (typed FeaturePython)
  n = 89
  ref = Cu_element
FEATURE [App::DocumentObjectGroupPython] Zn_element003  label="Zn_element : 9"  # scripted group (container) (typed FeaturePython)
  n = 9
  ref = Zn_element
FEATURE [App::DocumentObjectGroupPython] Pb_element006  label="Pb_element : 2"  # scripted group (container) (typed FeaturePython)
  n = 2
  ref = Pb_element
FEATURE [App::DocumentObjectGroupPython] G4_BRONZE  # scripted group (container) (typed FeaturePython)
  Dunit = g/cm3
  Dvalue = 8.82
  Group = -> [Cu_element003,Zn_element003,Pb_element006]
  conduct = 2
  density = 1
  expand = 3
  formula = G4_BRONZE
  name = G4_BRONZE
  specific = 4
FEATURE [App::DocumentObjectGroupPython] Fe_element008  label="Fe_element : 74"  # scripted group (container) (typed FeaturePython)
  n = 74
  ref = Fe_element
FEATURE [App::DocumentObjectGroupPython] Cr_element002  label="Cr_element : 18"  # scripted group (container) (typed FeaturePython)
  n = 18
  ref = Cr_element
FEATURE [App::DocumentObjectGroupPython] Ni_element002  label="Ni_element : 8"  # scripted group (container) (typed FeaturePython)
  n = 8
  ref = Ni_element
FEATURE [App::DocumentObjectGroupPython] G4_STAINLESS_STEEL  label="G4_STAINLESS-STEEL"  # scripted group (container) (typed FeaturePython)
  Dunit = g/cm3
  Dvalue = 8
  Group = -> [Fe_element008,Cr_element002,Ni_element002]
  conduct = 2
  density = 1
  expand = 3
  formula = G4_STAINLESS-STEEL
  name = G4_STAINLESS-STEEL
  specific = 4
FEATURE [App::DocumentObjectGroupPython] H_element116  label="H_element : 064"  # scripted group (container) (typed FeaturePython)
  n = 18
  ref = H_element
FEATURE [App::DocumentObjectGroupPython] C_element126  label="C_element : 071"  # scripted group (container) (typed FeaturePython)
  n = 12
  ref = C_element
FEATURE [App::DocumentObjectGroupPython] O_element109  label="O_element : 062"  # scripted group (container) (typed FeaturePython)
  n = 7
  ref = O_element
FEATURE [App::DocumentObjectGroupPython] G4_CR39  # scripted group (container) (typed FeaturePython)
  Dunit = g/cm3
  Dvalue = 1.32
  Group = -> [H_element116,C_element126,O_element109]
  conduct = 2
  density = 1
  expand = 3
  formula = G4_CR39
  name = G4_CR39
  specific = 4
FEATURE [App::DocumentObjectGroupPython] H_element117  label="H_element : 38"  # scripted group (container) (typed FeaturePython)
  n = 38
  ref = H_element
FEATURE [App::DocumentObjectGroupPython] C_element127  label="C_element : 072"  # scripted group (container) (typed FeaturePython)
  n = 18
  ref = C_element
FEATURE [App::DocumentObjectGroupPython] O_element110  label="O_element : 063"  # scripted group (container) (typed FeaturePython)
  n = 1
  ref = O_element
FEATURE [App::DocumentObjectGroupPython] G4_OCTADECANOL  # scripted group (container) (typed FeaturePython)
  Dunit = g/cm3
  Dvalue = 0.812
  Group = -> [H_element117,C_element127,O_element110]
  conduct = 2
  density = 1
  expand = 3
  formula = G4_OCTADECANOL
  name = G4_OCTADECANOL
  specific = 4
FEATURE [App::DocumentObjectGroupPython] HEP  # scripted group (container) (typed FeaturePython)
  Group = -> [G4_lH2,G4_lN2,G4_lO2,G4_lAr,G4_lBr,G4_lKr,G4_lXe,G4_PbWO4,G4_Galactic,G4_GRAPHITE_POROUS,G4_LUCITE,G4_BRASS,G4_BRONZE,G4_STAINLESS_STEEL,G4_CR39,G4_OCTADECANOL]
FEATURE [App::DocumentObjectGroupPython] C_element128  label="C_element : 073"  # scripted group (container) (typed FeaturePython)
  n = 14
  ref = C_element
FEATURE [App::DocumentObjectGroupPython] H_element118  label="H_element : 065"  # scripted group (container) (typed FeaturePython)
  n = 10
  ref = H_element
FEATURE [App::DocumentObjectGroupPython] O_element111  label="O_element : 064"  # scripted group (container) (typed FeaturePython)
  n = 2
  ref = O_element
FEATURE [App::DocumentObjectGroupPython] N_element050  label="N_element : 023"  # scripted group (container) (typed FeaturePython)
  n = 2
  ref = N_element
FEATURE [App::DocumentObjectGroupPython] G4_KEVLAR  # scripted group (container) (typed FeaturePython)
  Dunit = g/cm3
  Dvalue = 1.44
  Group = -> [C_element128,H_element118,O_element111,N_element050]
  conduct = 2
  density = 1
  expand = 3
  formula = G4_KEVLAR
  name = G4_KEVLAR
  specific = 4
FEATURE [App::DocumentObjectGroupPython] C_element129  label="C_element : 074"  # scripted group (container) (typed FeaturePython)
  n = 10
  ref = C_element
FEATURE [App::DocumentObjectGroupPython] H_element119  label="H_element : 066"  # scripted group (container) (typed FeaturePython)
  n = 8
  ref = H_element
FEATURE [App::DocumentObjectGroupPython] O_element112  label="O_element : 065"  # scripted group (container) (typed FeaturePython)
  n = 4
  ref = O_element
FEATURE [App::DocumentObjectGroupPython] G4_DACRON  # scripted group (container) (typed FeaturePython)
  Dunit = g/cm3
  Dvalue = 1.4
  Group = -> [C_element129,H_element119,O_element112]
  conduct = 2
  density = 1
  expand = 3
  formula = G4_DACRON
  name = G4_DACRON
  specific = 4
FEATURE [App::DocumentObjectGroupPython] C_element130  label="C_element : 075"  # scripted group (container) (typed FeaturePython)
  n = 4
  ref = C_element
FEATURE [App::DocumentObjectGroupPython] H_element120  label="H_element : 067"  # scripted group (container) (typed FeaturePython)
  n = 5
  ref = H_element
FEATURE [App::DocumentObjectGroupPython] Cl_element030  label="Cl_element : 016"  # scripted group (container) (typed FeaturePython)
  n = 1
  ref = Cl_element
FEATURE [App::DocumentObjectGroupPython] G4_NEOPRENE  # scripted group (container) (typed FeaturePython)
  Dunit = g/cm3
  Dvalue = 1.23
  Group = -> [C_element130,H_element120,Cl_element030]
  conduct = 2
  density = 1
  expand = 3
  formula = G4_NEOPRENE
  name = G4_NEOPRENE
  specific = 4
FEATURE [App::DocumentObjectGroupPython] Space  # scripted group (container) (typed FeaturePython)
  Group = -> [G4_KEVLAR,G4_DACRON,G4_NEOPRENE]
FEATURE [App::DocumentObjectGroupPython] H_element121  label="H_element : 068"  # scripted group (container) (typed FeaturePython)
  n = 5
  ref = H_element
FEATURE [App::DocumentObjectGroupPython] C_element131  label="C_element : 076"  # scripted group (container) (typed FeaturePython)
  n = 4
  ref = C_element
FEATURE [App::DocumentObjectGroupPython] N_element051  label="N_element : 3"  # scripted group (container) (typed FeaturePython)
  n = 3
  ref = N_element
FEATURE [App::DocumentObjectGroupPython] O_element113  label="O_element : 066"  # scripted group (container) (typed FeaturePython)
  n = 1
  ref = O_element
FEATURE [App::DocumentObjectGroupPython] G4_CYTOSINE  # scripted group (container) (typed FeaturePython)
  Dunit = g/cm3
  Dvalue = 1.55
  Group = -> [H_element121,C_element131,N_element051,O_element113]
  conduct = 2
  density = 1
  expand = 3
  formula = G4_CYTOSINE
  name = G4_CYTOSINE
  specific = 4
FEATURE [App::DocumentObjectGroupPython] H_element122  label="H_element : 069"  # scripted group (container) (typed FeaturePython)
  n = 6
  ref = H_element
FEATURE [App::DocumentObjectGroupPython] C_element132  label="C_element : 077"  # scripted group (container) (typed FeaturePython)
  n = 5
  ref = C_element
FEATURE [App::DocumentObjectGroupPython] N_element052  label="N_element : 024"  # scripted group (container) (typed FeaturePython)
  n = 2
  ref = N_element
FEATURE [App::DocumentObjectGroupPython] O_element114  label="O_element : 067"  # scripted group (container) (typed FeaturePython)
  n = 2
  ref = O_element
FEATURE [App::DocumentObjectGroupPython] G4_THYMINE  # scripted group (container) (typed FeaturePython)
  Dunit = g/cm3
  Dvalue = 1.23
  Group = -> [H_element122,C_element132,N_element052,O_element114]
  conduct = 2
  density = 1
  expand = 3
  formula = G4_THYMINE
  name = G4_THYMINE
  specific = 4
FEATURE [App::DocumentObjectGroupPython] H_element123  label="H_element : 070"  # scripted group (container) (typed FeaturePython)
  n = 4
  ref = H_element
FEATURE [App::DocumentObjectGroupPython] C_element133  label="C_element : 078"  # scripted group (container) (typed FeaturePython)
  n = 4
  ref = C_element
FEATURE [App::DocumentObjectGroupPython] N_element053  label="N_element : 025"  # scripted group (container) (typed FeaturePython)
  n = 2
  ref = N_element
FEATURE [App::DocumentObjectGroupPython] O_element115  label="O_element : 068"  # scripted group (container) (typed FeaturePython)
  n = 2
  ref = O_element
FEATURE [App::DocumentObjectGroupPython] G4_URACIL  # scripted group (container) (typed FeaturePython)
  Dunit = g/cm3
  Dvalue = 1.32
  Group = -> [H_element123,C_element133,N_element053,O_element115]
  conduct = 2
  density = 1
  expand = 3
  formula = G4_URACIL
  name = G4_URACIL
  specific = 4
FEATURE [App::DocumentObjectGroupPython] H_element124  label="H_element : 071"  # scripted group (container) (typed FeaturePython)
  n = 4
  ref = H_element
FEATURE [App::DocumentObjectGroupPython] C_element134  label="C_element : 079"  # scripted group (container) (typed FeaturePython)
  n = 5
  ref = C_element
FEATURE [App::DocumentObjectGroupPython] N_element054  label="N_element : 026"  # scripted group (container) (typed FeaturePython)
  n = 5
  ref = N_element
FEATURE [App::DocumentObjectGroupPython] G4_DNA_ADENINE  # scripted group (container) (typed FeaturePython)
  Dunit = g/cm3
  Dvalue = 1
  Group = -> [H_element124,C_element134,N_element054]
  conduct = 2
  density = 1
  expand = 3
  formula = G4_DNA_ADENINE
  name = G4_DNA_ADENINE
  specific = 4
FEATURE [App::DocumentObjectGroupPython] H_element125  label="H_element : 072"  # scripted group (container) (typed FeaturePython)
  n = 4
  ref = H_element
FEATURE [App::DocumentObjectGroupPython] C_element135  label="C_element : 080"  # scripted group (container) (typed FeaturePython)
  n = 5
  ref = C_element
FEATURE [App::DocumentObjectGroupPython] N_element055  label="N_element : 027"  # scripted group (container) (typed FeaturePython)
  n = 5
  ref = N_element
FEATURE [App::DocumentObjectGroupPython] O_element116  label="O_element : 069"  # scripted group (container) (typed FeaturePython)
  n = 1
  ref = O_element
FEATURE [App::DocumentObjectGroupPython] G4_DNA_GUANINE  # scripted group (container) (typed FeaturePython)
  Dunit = g/cm3
  Dvalue = 1
  Group = -> [H_element125,C_element135,N_element055,O_element116]
  conduct = 2
  density = 1
  expand = 3
  formula = G4_DNA_GUANINE
  name = G4_DNA_GUANINE
  specific = 4
FEATURE [App::DocumentObjectGroupPython] H_element126  label="H_element : 073"  # scripted group (container) (typed FeaturePython)
  n = 4
  ref = H_element
FEATURE [App::DocumentObjectGroupPython] C_element136  label="C_element : 081"  # scripted group (container) (typed FeaturePython)
  n = 4
  ref = C_element
FEATURE [App::DocumentObjectGroupPython] N_element056  label="N_element : 028"  # scripted group (container) (typed FeaturePython)
  n = 3
  ref = N_element
FEATURE [App::DocumentObjectGroupPython] O_element117  label="O_element : 070"  # scripted group (container) (typed FeaturePython)
  n = 1
  ref = O_element
FEATURE [App::DocumentObjectGroupPython] G4_DNA_CYTOSINE  # scripted group (container) (typed FeaturePython)
  Dunit = g/cm3
  Dvalue = 1
  Group = -> [H_element126,C_element136,N_element056,O_element117]
  conduct = 2
  density = 1
  expand = 3
  formula = G4_DNA_CYTOSINE
  name = G4_DNA_CYTOSINE
  specific = 4
FEATURE [App::DocumentObjectGroupPython] H_element127  label="H_element : 074"  # scripted group (container) (typed FeaturePython)
  n = 5
  ref = H_element
FEATURE [App::DocumentObjectGroupPython] C_element137  label="C_element : 082"  # scripted group (container) (typed FeaturePython)
  n = 5
  ref = C_element
FEATURE [App::DocumentObjectGroupPython] N_element057  label="N_element : 029"  # scripted group (container) (typed FeaturePython)
  n = 2
  ref = N_element
FEATURE [App::DocumentObjectGroupPython] O_element118  label="O_element : 071"  # scripted group (container) (typed FeaturePython)
  n = 2
  ref = O_element
FEATURE [App::DocumentObjectGroupPython] G4_DNA_THYMINE  # scripted group (container) (typed FeaturePython)
  Dunit = g/cm3
  Dvalue = 1
  Group = -> [H_element127,C_element137,N_element057,O_element118]
  conduct = 2
  density = 1
  expand = 3
  formula = G4_DNA_THYMINE
  name = G4_DNA_THYMINE
  specific = 4
FEATURE [App::DocumentObjectGroupPython] H_element128  label="H_element : 075"  # scripted group (container) (typed FeaturePython)
  n = 3
  ref = H_element
FEATURE [App::DocumentObjectGroupPython] C_element138  label="C_element : 083"  # scripted group (container) (typed FeaturePython)
  n = 4
  ref = C_element
FEATURE [App::DocumentObjectGroupPython] N_element058  label="N_element : 030"  # scripted group (container) (typed FeaturePython)
  n = 2
  ref = N_element
FEATURE [App::DocumentObjectGroupPython] O_element119  label="O_element : 072"  # scripted group (container) (typed FeaturePython)
  n = 2
  ref = O_element
FEATURE [App::DocumentObjectGroupPython] G4_DNA_URACIL  # scripted group (container) (typed FeaturePython)
  Dunit = g/cm3
  Dvalue = 1
  Group = -> [H_element128,C_element138,N_element058,O_element119]
  conduct = 2
  density = 1
  expand = 3
  formula = G4_DNA_URACIL
  name = G4_DNA_URACIL
  specific = 4
FEATURE [App::DocumentObjectGroupPython] H_element129  label="H_element : 076"  # scripted group (container) (typed FeaturePython)
  n = 10
  ref = H_element
FEATURE [App::DocumentObjectGroupPython] C_element139  label="C_element : 084"  # scripted group (container) (typed FeaturePython)
  n = 10
  ref = C_element
FEATURE [App::DocumentObjectGroupPython] N_element059  label="N_element : 031"  # scripted group (container) (typed FeaturePython)
  n = 5
  ref = N_element
FEATURE [App::DocumentObjectGroupPython] O_element120  label="O_element : 073"  # scripted group (container) (typed FeaturePython)
  n = 4
  ref = O_element
FEATURE [App::DocumentObjectGroupPython] G4_DNA_ADENOSINE  # scripted group (container) (typed FeaturePython)
  Dunit = g/cm3
  Dvalue = 1
  Group = -> [H_element129,C_element139,N_element059,O_element120]
  conduct = 2
  density = 1
  expand = 3
  formula = G4_DNA_ADENOSINE
  name = G4_DNA_ADENOSINE
  specific = 4
FEATURE [App::DocumentObjectGroupPython] H_element130  label="H_element : 077"  # scripted group (container) (typed FeaturePython)
  n = 10
  ref = H_element
FEATURE [App::DocumentObjectGroupPython] C_element140  label="C_element : 085"  # scripted group (container) (typed FeaturePython)
  n = 10
  ref = C_element
FEATURE [App::DocumentObjectGroupPython] N_element060  label="N_element : 032"  # scripted group (container) (typed FeaturePython)
  n = 5
  ref = N_element
FEATURE [App::DocumentObjectGroupPython] O_element121  label="O_element : 074"  # scripted group (container) (typed FeaturePython)
  n = 5
  ref = O_element
FEATURE [App::DocumentObjectGroupPython] G4_DNA_GUANOSINE  # scripted group (container) (typed FeaturePython)
  Dunit = g/cm3
  Dvalue = 1
  Group = -> [H_element130,C_element140,N_element060,O_element121]
  conduct = 2
  density = 1
  expand = 3
  formula = G4_DNA_GUANOSINE
  name = G4_DNA_GUANOSINE
  specific = 4
FEATURE [App::DocumentObjectGroupPython] H_element131  label="H_element : 078"  # scripted group (container) (typed FeaturePython)
  n = 10
  ref = H_element
FEATURE [App::DocumentObjectGroupPython] C_element141  label="C_element : 086"  # scripted group (container) (typed FeaturePython)
  n = 9
  ref = C_element
FEATURE [App::DocumentObjectGroupPython] N_element061  label="N_element : 033"  # scripted group (container) (typed FeaturePython)
  n = 3
  ref = N_element
FEATURE [App::DocumentObjectGroupPython] O_element122  label="O_element : 075"  # scripted group (container) (typed FeaturePython)
  n = 5
  ref = O_element
FEATURE [App::DocumentObjectGroupPython] G4_DNA_CYTIDINE  # scripted group (container) (typed FeaturePython)
  Dunit = g/cm3
  Dvalue = 1
  Group = -> [H_element131,C_element141,N_element061,O_element122]
  conduct = 2
  density = 1
  expand = 3
  formula = G4_DNA_CYTIDINE
  name = G4_DNA_CYTIDINE
  specific = 4
FEATURE [App::DocumentObjectGroupPython] H_element132  label="H_element : 079"  # scripted group (container) (typed FeaturePython)
  n = 9
  ref = H_element
FEATURE [App::DocumentObjectGroupPython] C_element142  label="C_element : 087"  # scripted group (container) (typed FeaturePython)
  n = 9
  ref = C_element
FEATURE [App::DocumentObjectGroupPython] N_element062  label="N_element : 034"  # scripted group (container) (typed FeaturePython)
  n = 2
  ref = N_element
FEATURE [App::DocumentObjectGroupPython] O_element123  label="O_element : 076"  # scripted group (container) (typed FeaturePython)
  n = 6
  ref = O_element
FEATURE [App::DocumentObjectGroupPython] G4_DNA_URIDINE  # scripted group (container) (typed FeaturePython)
  Dunit = g/cm3
  Dvalue = 1
  Group = -> [H_element132,C_element142,N_element062,O_element123]
  conduct = 2
  density = 1
  expand = 3
  formula = G4_DNA_URIDINE
  name = G4_DNA_URIDINE
  specific = 4
FEATURE [App::DocumentObjectGroupPython] H_element133  label="H_element : 080"  # scripted group (container) (typed FeaturePython)
  n = 11
  ref = H_element
FEATURE [App::DocumentObjectGroupPython] C_element143  label="C_element : 088"  # scripted group (container) (typed FeaturePython)
  n = 10
  ref = C_element
FEATURE [App::DocumentObjectGroupPython] N_element063  label="N_element : 035"  # scripted group (container) (typed FeaturePython)
  n = 2
  ref = N_element
FEATURE [App::DocumentObjectGroupPython] O_element124  label="O_element : 077"  # scripted group (container) (typed FeaturePython)
  n = 6
  ref = O_element
FEATURE [App::DocumentObjectGroupPython] G4_DNA_METHYLURIDINE  # scripted group (container) (typed FeaturePython)
  Dunit = g/cm3
  Dvalue = 1
  Group = -> [H_element133,C_element143,N_element063,O_element124]
  conduct = 2
  density = 1
  expand = 3
  formula = G4_DNA_METHYLURIDINE
  name = G4_DNA_METHYLURIDINE
  specific = 4
FEATURE [App::DocumentObjectGroupPython] P_element014  label="P_element : 003"  # scripted group (container) (typed FeaturePython)
  n = 1
  ref = P_element
FEATURE [App::DocumentObjectGroupPython] O_element125  label="O_element : 078"  # scripted group (container) (typed FeaturePython)
  n = 3
  ref = O_element
FEATURE [App::DocumentObjectGroupPython] G4_DNA_MONOPHOSPHATE  # scripted group (container) (typed FeaturePython)
  Dunit = g/cm3
  Dvalue = 1
  Group = -> [P_element014,O_element125]
  conduct = 2
  density = 1
  expand = 3
  formula = G4_DNA_MONOPHOSPHATE
  name = G4_DNA_MONOPHOSPHATE
  specific = 4
FEATURE [App::DocumentObjectGroupPython] H_element134  label="H_element : 081"  # scripted group (container) (typed FeaturePython)
  n = 10
  ref = H_element
FEATURE [App::DocumentObjectGroupPython] C_element144  label="C_element : 089"  # scripted group (container) (typed FeaturePython)
  n = 10
  ref = C_element
FEATURE [App::DocumentObjectGroupPython] N_element064  label="N_element : 036"  # scripted group (container) (typed FeaturePython)
  n = 5
  ref = N_element
FEATURE [App::DocumentObjectGroupPython] O_element126  label="O_element : 079"  # scripted group (container) (typed FeaturePython)
  n = 7
  ref = O_element
FEATURE [App::DocumentObjectGroupPython] P_element015  label="P_element : 004"  # scripted group (container) (typed FeaturePython)
  n = 1
  ref = P_element
FEATURE [App::DocumentObjectGroupPython] G4_DNA_A  # scripted group (container) (typed FeaturePython)
  Dunit = g/cm3
  Dvalue = 1
  Group = -> [H_element134,C_element144,N_element064,O_element126,P_element015]
  conduct = 2
  density = 1
  expand = 3
  formula = G4_DNA_A
  name = G4_DNA_A
  specific = 4
FEATURE [App::DocumentObjectGroupPython] H_element135  label="H_element : 082"  # scripted group (container) (typed FeaturePython)
  n = 10
  ref = H_element
FEATURE [App::DocumentObjectGroupPython] C_element145  label="C_element : 090"  # scripted group (container) (typed FeaturePython)
  n = 10
  ref = C_element
FEATURE [App::DocumentObjectGroupPython] N_element065  label="N_element : 037"  # scripted group (container) (typed FeaturePython)
  n = 5
  ref = N_element
FEATURE [App::DocumentObjectGroupPython] O_element127  label="O_element : 8"  # scripted group (container) (typed FeaturePython)
  n = 8
  ref = O_element
FEATURE [App::DocumentObjectGroupPython] P_element016  label="P_element : 005"  # scripted group (container) (typed FeaturePython)
  n = 1
  ref = P_element
FEATURE [App::DocumentObjectGroupPython] G4_DNA_G  # scripted group (container) (typed FeaturePython)
  Dunit = g/cm3
  Dvalue = 1
  Group = -> [H_element135,C_element145,N_element065,O_element127,P_element016]
  conduct = 2
  density = 1
  expand = 3
  formula = G4_DNA_G
  name = G4_DNA_G
  specific = 4
FEATURE [App::DocumentObjectGroupPython] H_element136  label="H_element : 083"  # scripted group (container) (typed FeaturePython)
  n = 10
  ref = H_element
FEATURE [App::DocumentObjectGroupPython] C_element146  label="C_element : 091"  # scripted group (container) (typed FeaturePython)
  n = 9
  ref = C_element
FEATURE [App::DocumentObjectGroupPython] N_element066  label="N_element : 038"  # scripted group (container) (typed FeaturePython)
  n = 3
  ref = N_element
FEATURE [App::DocumentObjectGroupPython] O_element128  label="O_element : 080"  # scripted group (container) (typed FeaturePython)
  n = 8
  ref = O_element
FEATURE [App::DocumentObjectGroupPython] P_element017  label="P_element : 006"  # scripted group (container) (typed FeaturePython)
  n = 1
  ref = P_element
FEATURE [App::DocumentObjectGroupPython] G4_DNA_C  # scripted group (container) (typed FeaturePython)
  Dunit = g/cm3
  Dvalue = 1
  Group = -> [H_element136,C_element146,N_element066,O_element128,P_element017]
  conduct = 2
  density = 1
  expand = 3
  formula = G4_DNA_C
  name = G4_DNA_C
  specific = 4
FEATURE [App::DocumentObjectGroupPython] H_element137  label="H_element : 084"  # scripted group (container) (typed FeaturePython)
  n = 9
  ref = H_element
FEATURE [App::DocumentObjectGroupPython] C_element147  label="C_element : 092"  # scripted group (container) (typed FeaturePython)
  n = 9
  ref = C_element
FEATURE [App::DocumentObjectGroupPython] N_element067  label="N_element : 039"  # scripted group (container) (typed FeaturePython)
  n = 2
  ref = N_element
FEATURE [App::DocumentObjectGroupPython] O_element129  label="O_element : 9"  # scripted group (container) (typed FeaturePython)
  n = 9
  ref = O_element
FEATURE [App::DocumentObjectGroupPython] P_element018  label="P_element : 007"  # scripted group (container) (typed FeaturePython)
  n = 1
  ref = P_element
FEATURE [App::DocumentObjectGroupPython] G4_DNA_U  # scripted group (container) (typed FeaturePython)
  Dunit = g/cm3
  Dvalue = 1
  Group = -> [H_element137,C_element147,N_element067,O_element129,P_element018]
  conduct = 2
  density = 1
  expand = 3
  formula = G4_DNA_U
  name = G4_DNA_U
  specific = 4
FEATURE [App::DocumentObjectGroupPython] H_element138  label="H_element : 085"  # scripted group (container) (typed FeaturePython)
  n = 11
  ref = H_element
FEATURE [App::DocumentObjectGroupPython] C_element148  label="C_element : 093"  # scripted group (container) (typed FeaturePython)
  n = 10
  ref = C_element
FEATURE [App::DocumentObjectGroupPython] N_element068  label="N_element : 040"  # scripted group (container) (typed FeaturePython)
  n = 2
  ref = N_element
FEATURE [App::DocumentObjectGroupPython] O_element130  label="O_element : 081"  # scripted group (container) (typed FeaturePython)
  n = 9
  ref = O_element
FEATURE [App::DocumentObjectGroupPython] P_element019  label="P_element : 008"  # scripted group (container) (typed FeaturePython)
  n = 1
  ref = P_element
FEATURE [App::DocumentObjectGroupPython] G4_DNA_MU  # scripted group (container) (typed FeaturePython)
  Dunit = g/cm3
  Dvalue = 1
  Group = -> [H_element138,C_element148,N_element068,O_element130,P_element019]
  conduct = 2
  density = 1
  expand = 3
  formula = G4_DNA_MU
  name = G4_DNA_MU
  specific = 4
FEATURE [App::DocumentObjectGroupPython] BioChemical  # scripted group (container) (typed FeaturePython)
  Group = -> [G4_CYTOSINE,G4_THYMINE,G4_URACIL,G4_DNA_ADENINE,G4_DNA_GUANINE,G4_DNA_CYTOSINE,G4_DNA_THYMINE,G4_DNA_URACIL,G4_DNA_ADENOSINE,G4_DNA_GUANOSINE,G4_DNA_CYTIDINE,G4_DNA_URIDINE,G4_DNA_METHYLURIDINE,G4_DNA_MONOPHOSPHATE,G4_DNA_A,G4_DNA_G,G4_DNA_C,G4_DNA_U,G4_DNA_MU]
FEATURE [App::DocumentObjectGroupPython] G4Materials  # scripted group (container) (typed FeaturePython)
  Group = -> [NIST,Element,HEP,Space,BioChemical]
  version = 1
FEATURE [App::DocumentObjectGroupPython] Geant4  # scripted group (container) (typed FeaturePython)
  Group = -> [G4Isotopes,G4Elements,G4Materials]
FEATURE [App::DocumentObjectGroupPython] Materials  # scripted group (container) (typed FeaturePython)
  Group = -> [Geant4]
FEATURE [Part::FeaturePython] GDMLBox_WorldBox  # WARN: FeaturePython — macro-defined, semantics opaque (R4)
  lunit = 2
  material = 5
  x = 272.933
  y = 260
  z = 260
FEATURE [Part::FeaturePython] GDMLSphere_Sphere  # WARN: FeaturePython — macro-defined, semantics opaque (R4)
  Placement = pos=(20,0,0) rot=(0,0,1;0rad)
  aunit = 0
  deltaphi = 2.02
  deltatheta = 2.02
  lunit = 2
  material = 18
  rmax = 20
  rmin = 10
  startphi = 0
  starttheta = 0
FEATURE [Part::FeaturePython] GDMLTorus_Torus  # WARN: FeaturePython — macro-defined, semantics opaque (R4)
  aunit = deg
  deltaphi = 360
  lunit = 2
  material = 5
  rmax = 5
  rmin = 0
  rtor = 10
  startphi = 10
FEATURE [Part::MultiFuse] Fusion
  Placement = pos=(30,0,0) rot=(0,0,1;0rad)
  Shapes = -> [GDMLSphere_Sphere,GDMLTorus_Torus]
  material = 18
FEATURE [Part::FeaturePython] Array  # Draft array (typed FeaturePython)
  Angle = 360
  ArrayType = 1
  Axis = (0,0,1)
  Base = -> Fusion
  Center = (0,0,0)
  Count = 5
  Fuse = false
  IntervalAxis = (0,0,0)
  IntervalX = (50,0,0)
  IntervalY = (0,50,0)
  IntervalZ = (0,0,50)
  NumberCircles = 3
  NumberPolar = 5
  NumberX = 2
  NumberY = 2
  NumberZ = 1
  RadialDistance = 50
  Symmetry = 1
  TangentialDistance = 25
FEATURE [Part::FeaturePython] Clone  label="Array001"  # Draft clone (typed FeaturePython)
  AttacherType = Attacher::AttachEngine3D
  Fuse = false
  Objects = -> [Array]
  Scale = (1.5,1,1)
FEATURE [App::Part] Part
  Group = -> [Clone]
  Origin = -> Origin001
FEATURE [App::Part] worldVOL
  Group = -> [GDMLBox_WorldBox,Part]
  Origin = -> Origin
